FCSTD DOCUMENT  (FreeCAD 0.19R)
Label: CNC
License: All rights reserved
LicenseURL: http://en.wikipedia.org/wiki/All_rights_reserved
objects: App::Link×56, App::DocumentObjectGroup×2, PartDesign::CoordinateSystem×1, App::FeaturePython×1, App::Part×1
note: 1 computed .brp shape members not serialized (recipe doc carries the construction recipe); baked Part::Feature solids carry a one-line shape summary decoded from their .brp
EXTERNAL_REF file=x_tube.FCStd obj=LCS_hole1
EXTERNAL_REF file=y_tube.FCStd obj=LCS_hole1
EXTERNAL_REF file=x_tube.FCStd obj=Body
EXTERNAL_REF file=y_tube.FCStd obj=LCS_hole2
EXTERNAL_REF file=x_rail.FCStd obj=LCS_mount
EXTERNAL_REF file=x_tube.FCStd obj=LCS_rail_mount
EXTERNAL_REF file=x_rail.FCStd obj=Body
EXTERNAL_REF file=TRH15A.FCStd obj=LCS_MOUNT
EXTERNAL_REF file=x_rail.FCStd obj=LCS_CARET_MOUNT
EXTERNAL_REF file=TRH15A.FCStd obj=Body
EXTERNAL_REF file=BF12_SUPPORT.FCStd obj=LCS_TUBE_MOUNT
EXTERNAL_REF file=x_tube.FCStd obj=LCS_BF_MOUNT
EXTERNAL_REF file=BF12_SUPPORT.FCStd obj=Body
EXTERNAL_REF file=BF12.FCStd obj=LCS_mount
EXTERNAL_REF file=BF12_SUPPORT.FCStd obj=LCS_BF_MOUNT
EXTERNAL_REF file=BF12.FCStd obj=Body
EXTERNAL_REF file=portal_tube.FCStd obj=LCS_1
EXTERNAL_REF file=spacer.FCStd obj=LCS_6
EXTERNAL_REF file=portal_tube.FCStd obj=Body
EXTERNAL_REF file=BF12.FCStd obj=LCS_BB1
EXTERNAL_REF file=sfu1605_500.FCStd obj=LCS_SLAVE_SIDE
EXTERNAL_REF file=sfu1605_500.FCStd obj=Body
EXTERNAL_REF file=x_tube.FCStd obj=LCS_hole2
EXTERNAL_REF file=y_tube.FCStd obj=Body
EXTERNAL_REF file=BK12.FCStd obj=LCS_mount
EXTERNAL_REF file=sfu1605_500.FCStd obj=LCS_BK_MOUNT
EXTERNAL_REF file=BK12.FCStd obj=Body
EXTERNAL_REF file=BK12.FCStd obj=LCS_H1
EXTERNAL_REF file=BK12_SUPPORT.FCStd obj=LCS_M1
EXTERNAL_REF file=BK12_SUPPORT.FCStd obj=Body
EXTERNAL_REF file=DSG16.FCStd obj=LCS_M2
EXTERNAL_REF file=portal_support_tube.FCStd obj=LCS_mh2
EXTERNAL_REF file=DSG16.FCStd obj=Body
EXTERNAL_REF file=portal_support_tube_left.FCStd obj=LCS_ch2
EXTERNAL_REF file=DSG16.FCStd obj=LCS_H1
EXTERNAL_REF file=1605.FCStd obj=LCS_N1
EXTERNAL_REF file=1605.FCStd obj=Body
EXTERNAL_REF file=DSG16.FCStd obj=LCS_H2
EXTERNAL_REF file=1605.FCStd obj=LCS_N2
EXTERNAL_REF file=coupling.FCStd obj=LCS_10MM
EXTERNAL_REF file=sfu1605_500.FCStd obj=LCS_COUPLING
EXTERNAL_REF file=coupling.FCStd obj=Body
EXTERNAL_REF file=coupling.FCStd obj=LCS_8MM
EXTERNAL_REF file=nema_23.FCStd obj=LCS_shaft
EXTERNAL_REF file=nema_23.FCStd obj=Body
EXTERNAL_REF file=nema_23.FCStd obj=LCS_m3
EXTERNAL_REF file=stpm_bracket.FCStd obj=LCS_h2
EXTERNAL_REF file=stpm_bracket.FCStd obj=Body
EXTERNAL_REF file=portal_tube.FCStd obj=LCS_top_rail
EXTERNAL_REF file=y_rail.FCStd obj=LCS_mount
EXTERNAL_REF file=y_rail.FCStd obj=Body
EXTERNAL_REF file=portal_tube.FCStd obj=LCS_bottom_RAIL
EXTERNAL_REF file=y_rail.FCStd obj=LCS_caret_mount
EXTERNAL_REF file=TRH15A.FCStd obj=LCS_h4
EXTERNAL_REF file=zbracket.FCStd obj=LCS_h1
EXTERNAL_REF file=zbracket.FCStd obj=Body
EXTERNAL_REF file=LINMOD200.FCStd obj=LCS_m2
EXTERNAL_REF file=zbracket.FCStd obj=LCS_1
EXTERNAL_REF file=LINMOD200.FCStd obj=Body
EXTERNAL_REF file=LINMOD200.FCStd obj=LCS_caret_mount
EXTERNAL_REF file=LINMOD_CARET.FCStd obj=LCS_m1
EXTERNAL_REF file=LINMOD_CARET.FCStd obj=Body
EXTERNAL_REF file=LINMOD_CARET.FCStd obj=LCS_2
EXTERNAL_REF file=adapter_plate.FCStd obj=LCS_7
EXTERNAL_REF file=adapter_plate.FCStd obj=Body
EXTERNAL_REF file=adapter_plate.FCStd obj=LCS_2
EXTERNAL_REF file=spindle_holder.FCStd obj=LCS_h2
EXTERNAL_REF file=spindle_holder.FCStd obj=Body
EXTERNAL_REF file=spindle.FCStd obj=LCS_mount
EXTERNAL_REF file=spindle_holder.FCStd obj=LCS_motor_mount1
EXTERNAL_REF file=spindle.FCStd obj=Body
EXTERNAL_REF file=BF12_PORTAL_SUPPORT.FCStd obj=LCS_TUBE_MOUNT
EXTERNAL_REF file=portal_tube.FCStd obj=LCS_BF
EXTERNAL_REF file=BF12_PORTAL_SUPPORT.FCStd obj=Body
EXTERNAL_REF file=BF12_PORTAL_SUPPORT.FCStd obj=LCS_BF_MOUNT
EXTERNAL_REF file=sfu1605_700.FCStd obj=LCS_m1
EXTERNAL_REF file=sfu1605_700.FCStd obj=Body
EXTERNAL_REF file=sfu1605_700.FCStd obj=LCS_m2
EXTERNAL_REF file=BK12_PORTAL_SUPPORT.FCStd obj=LCS_M1
EXTERNAL_REF file=BK12_PORTAL_SUPPORT.FCStd obj=Body
EXTERNAL_REF file=sfu1605_700.FCStd obj=LCS_m3
EXTERNAL_REF file=DSG16.FCStd obj=LCS_M1
EXTERNAL_REF file=zbracket.FCStd obj=LCS_DSG16_MOUNT4
EXTERNAL_REF file=TRH15A.FCStd obj=LCS_h1
EXTERNAL_REF file=portal_support_tube.FCStd obj=LCS_h1
EXTERNAL_REF file=portal_support_tube.FCStd obj=Body
EXTERNAL_REF file=portal_support_tube.FCStd obj=LCS_h8
EXTERNAL_REF file=portal_support_tube_left.FCStd obj=LCS_h4
EXTERNAL_REF file=portal_support_tube_left.FCStd obj=Body
EXTERNAL_REF file=portal_support_tube_left.FCStd obj=LCS_h5
EXTERNAL_REF file=portal_column_right.FCStd obj=LCS_h1
EXTERNAL_REF file=portal_support_tube.FCStd obj=LCS_ch2
EXTERNAL_REF file=portal_column_right.FCStd obj=Body
EXTERNAL_REF file=portal_column_left.FCStd obj=LCS_h1
EXTERNAL_REF file=portal_support_tube_left.FCStd obj=LCS_4
EXTERNAL_REF file=portal_column_left.FCStd obj=Body
EXTERNAL_REF file=portal_column_right.FCStd obj=LCS_3
EXTERNAL_REF file=spacer.FCStd obj=LCS_2
EXTERNAL_REF file=spacer.FCStd obj=Body
EXTERNAL_REF file=portal_column_left.FCStd obj=LCS_2
EXTERNAL_REF file=spacer.FCStd obj=LCS_1

FEATURE [App::DocumentObjectGroup] Parts
FEATURE [PartDesign::CoordinateSystem] LCS_Origin
  AttacherType = Attacher::AttachEngine3D
  MapMode = 2
  Support = -> [X_Axis]
FEATURE [App::DocumentObjectGroup] Constraints
FEATURE [App::FeaturePython] Variables  # WARN: FeaturePython — macro-defined, semantics opaque (R4)
FEATURE [App::Link] x_tube_Body
  AssemblyType = Asm4EE
  AttachedBy = #LCS_hole1
  AttachedTo = y_tube_Body#LCS_hole1
  AttachmentOffset = pos=(0,0,0) rot=(-0.707107,0.707107,0;3.14159rad)
  LinkPlacement = pos=(-580,-3.739e-13,30) rot=(-0.707107,0.707107,0;3.14159rad)
  LinkedObject = -> <external x_tube.FCStd>#Body
  Placement = pos=(-580,-3.739e-13,30) rot=(-0.707107,0.707107,0;3.14159rad)
  expr: Placement = y_tube_Body.Placement * y_tube#LCS_hole1.Placement * AttachmentOffset * x_tube#LCS_hole1.Placement ^ -1
FEATURE [App::Link] x_tube_Body001
  AssemblyType = Asm4EE
  AttachedBy = #LCS_hole1
  AttachedTo = y_tube_Body#LCS_hole2
  AttachmentOffset = pos=(0,0,0) rot=(0.707107,-0.707107,0;3.14159rad)
  LinkPlacement = pos=(-580,-733,30) rot=(0.707107,-0.707107,0;3.14159rad)
  LinkedObject = -> <external x_tube.FCStd>#Body
  Placement = pos=(-580,-733,30) rot=(0.707107,-0.707107,0;3.14159rad)
  expr: Placement = y_tube_Body.Placement * y_tube#LCS_hole2.Placement * AttachmentOffset * x_tube#LCS_hole1.Placement ^ -1
FEATURE [App::Link] x_rail_Body
  AssemblyType = Asm4EE
  AttachedBy = #LCS_mount
  AttachedTo = x_tube_Body#LCS_rail_mount
  AttachmentOffset = pos=(0,0,0) rot=(0,-1,0;3.14159rad)
  LinkPlacement = pos=(-540,-3.67e-13,60) rot=(0,0,-1;4.71239rad)
  LinkedObject = -> <external x_rail.FCStd>#Body
  Placement = pos=(-540,-3.67e-13,60) rot=(0,0,-1;4.71239rad)
  expr: Placement = x_tube_Body.Placement * x_tube#LCS_rail_mount.Placement * AttachmentOffset * x_rail#LCS_mount.Placement ^ -1
FEATURE [App::Link] x_rail_Body001
  AssemblyType = Asm4EE
  AttachedBy = #LCS_mount
  AttachedTo = x_tube_Body001#LCS_rail_mount
  AttachmentOffset = pos=(0,0,0) rot=(0,1,0;3.14159rad)
  LinkPlacement = pos=(-540,-733,60) rot=(0,0,-1;4.71239rad)
  LinkedObject = -> <external x_rail.FCStd>#Body
  Placement = pos=(-540,-733,60) rot=(0,0,-1;4.71239rad)
  expr: Placement = x_tube_Body001.Placement * x_tube#LCS_rail_mount.Placement * AttachmentOffset * x_rail#LCS_mount.Placement ^ -1
FEATURE [App::Link] TRH15A_Body
  AssemblyType = Asm4EE
  AttachedBy = #LCS_MOUNT
  AttachedTo = x_rail_Body#LCS_CARET_MOUNT
  AttachmentOffset = pos=(0,0,0) rot=(1,0,0;3.14159rad)
  LinkPlacement = pos=(-440,-2.957e-13,64.2) rot=(0,0,-1;1.5708rad)
  LinkedObject = -> <external TRH15A.FCStd>#Body
  Placement = pos=(-440,-2.957e-13,64.2) rot=(0,0,-1;1.5708rad)
  expr: Placement = x_rail_Body.Placement * x_rail#LCS_CARET_MOUNT.Placement * AttachmentOffset * TRH15A#LCS_MOUNT.Placement ^ -1
FEATURE [App::Link] TRH15A_Body001
  AssemblyType = Asm4EE
  AttachedBy = #LCS_MOUNT
  AttachedTo = x_rail_Body001#LCS_CARET_MOUNT
  AttachmentOffset = pos=(0,0,0) rot=(1,0,0;3.14159rad)
  LinkPlacement = pos=(-440,-733,64.2) rot=(0,0,-1;1.5708rad)
  LinkedObject = -> <external TRH15A.FCStd>#Body
  Placement = pos=(-440,-733,64.2) rot=(0,0,-1;1.5708rad)
  expr: Placement = x_rail_Body001.Placement * x_rail#LCS_CARET_MOUNT.Placement * AttachmentOffset * TRH15A#LCS_MOUNT.Placement ^ -1
FEATURE [App::Link] BF12_SUPPORT_Body
  AssemblyType = Asm4EE
  AttachedBy = #LCS_TUBE_MOUNT
  AttachedTo = x_tube_Body#LCS_BF_MOUNT
  AttachmentOffset = pos=(0,0,0) rot=(0,-1,0;3.14159rad)
  LinkPlacement = pos=(-575,-3.77e-13,60) rot=(0,0,-1;4.71239rad)
  LinkedObject = -> <external BF12_SUPPORT.FCStd>#Body
  Placement = pos=(-575,-3.77e-13,60) rot=(0,0,-1;4.71239rad)
  expr: Placement = x_tube_Body.Placement * x_tube#LCS_BF_MOUNT.Placement * AttachmentOffset * BF12_SUPPORT#LCS_TUBE_MOUNT.Placement ^ -1
FEATURE [App::Link] BF12_Body
  AssemblyType = Asm4EE
  AttachedBy = #LCS_mount
  AttachedTo = BF12_SUPPORT_Body#LCS_BF_MOUNT
  AttachmentOffset = pos=(0,0,0) rot=(0,-1,0;3.14159rad)
  LinkPlacement = pos=(-575,-3.884e-13,96) rot=(0,0,-1;4.71239rad)
  LinkedObject = -> <external BF12.FCStd>#Body
  Placement = pos=(-575,-3.884e-13,96) rot=(0,0,-1;4.71239rad)
  expr: Placement = BF12_SUPPORT_Body.Placement * BF12_SUPPORT#LCS_BF_MOUNT.Placement * AttachmentOffset * BF12#LCS_mount.Placement ^ -1
FEATURE [App::Link] BF12_SUPPORT_Body001
  AssemblyType = Asm4EE
  AttachedBy = #LCS_TUBE_MOUNT
  AttachedTo = x_tube_Body001#LCS_BF_MOUNT
  AttachmentOffset = pos=(0,0,0) rot=(0,-1,0;3.14159rad)
  LinkPlacement = pos=(-575,-733,60) rot=(0,0,1;1.5708rad)
  LinkedObject = -> <external BF12_SUPPORT.FCStd>#Body
  Placement = pos=(-575,-733,60) rot=(0,0,1;1.5708rad)
  expr: Placement = x_tube_Body001.Placement * x_tube#LCS_BF_MOUNT.Placement * AttachmentOffset * BF12_SUPPORT#LCS_TUBE_MOUNT.Placement ^ -1
FEATURE [App::Link] BF12_Body001
  AssemblyType = Asm4EE
  AttachedBy = #LCS_mount
  AttachedTo = BF12_SUPPORT_Body001#LCS_BF_MOUNT
  AttachmentOffset = pos=(0,0,0) rot=(0,-1,0;3.14159rad)
  LinkPlacement = pos=(-575,-733,96) rot=(0,0,1;1.5708rad)
  LinkedObject = -> <external BF12.FCStd>#Body
  Placement = pos=(-575,-733,96) rot=(0,0,1;1.5708rad)
  expr: Placement = BF12_SUPPORT_Body001.Placement * BF12_SUPPORT#LCS_BF_MOUNT.Placement * AttachmentOffset * BF12#LCS_mount.Placement ^ -1
FEATURE [App::Link] portal_tube_Body
  AssemblyType = Asm4EE
  AttachedBy = #LCS_1
  AttachedTo = spacer_Body#LCS_6
  AttachmentOffset = pos=(0,0,0) rot=(-0.707107,-0.707107,0;3.14159rad)
  LinkPlacement = pos=(-576.9,-823,254) rot=(1,0,0;3.14159rad)
  LinkedObject = -> <external portal_tube.FCStd>#Body
  Placement = pos=(-576.9,-823,254) rot=(1,0,0;3.14159rad)
  expr: Placement = spacer_Body.Placement * spacer#LCS_6.Placement * AttachmentOffset * portal_tube#LCS_1.Placement ^ -1
FEATURE [App::Link] sfu1605_500_Body
  AssemblyType = Asm4EE
  AttachedBy = #LCS_SLAVE_SIDE
  AttachedTo = BF12_Body#LCS_BB1
  LinkPlacement = pos=(-72,1.847e-13,121) rot=(0,0,1;1.5708rad)
  LinkedObject = -> <external sfu1605_500.FCStd>#Body
  Placement = pos=(-72,1.847e-13,121) rot=(0,0,1;1.5708rad)
  expr: Placement = BF12_Body.Placement * BF12#LCS_BB1.Placement * AttachmentOffset * sfu1605_500#LCS_SLAVE_SIDE.Placement ^ -1
FEATURE [App::Link] sfu1605_500_Body001
  AssemblyType = Asm4EE
  AttachedBy = #LCS_SLAVE_SIDE
  AttachedTo = BF12_Body001#LCS_BB1
  LinkPlacement = pos=(-72,-733,121) rot=(0,0,-1;4.71239rad)
  LinkedObject = -> <external sfu1605_500.FCStd>#Body
  Placement = pos=(-72,-733,121) rot=(0,0,-1;4.71239rad)
  expr: Placement = BF12_Body001.Placement * BF12#LCS_BB1.Placement * AttachmentOffset * sfu1605_500#LCS_SLAVE_SIDE.Placement ^ -1
FEATURE [App::Link] y_tube_Body001
  AssemblyType = Asm4EE
  AttachedBy = #LCS_hole2
  AttachedTo = x_tube_Body001#LCS_hole2
  AttachmentOffset = pos=(0,0,0) rot=(-0.707107,0.707107,0;3.14159rad)
  LinkPlacement = pos=(-550,-763,-30) rot=(0,0,1;3.14159rad)
  LinkedObject = -> <external y_tube.FCStd>#Body
  Placement = pos=(-550,-763,-30) rot=(0,0,1;3.14159rad)
  expr: Placement = x_tube_Body001.Placement * x_tube#LCS_hole2.Placement * AttachmentOffset * y_tube#LCS_hole2.Placement ^ -1
FEATURE [App::Link] y_tube_Body
  AssemblyType = Asm4EE
  AttachedBy = #LCS_hole2
  AttachedTo = Parent Assembly#LCS_Origin
  AttachmentOffset = pos=(0,0,0) rot=(0,0,1;1.5708rad)
  LinkPlacement = pos=(-3.4e-13,-763,-30) rot=(0,0,1;3.14159rad)
  LinkedObject = -> <external y_tube.FCStd>#Body
  Placement = pos=(-3.4e-13,-763,-30) rot=(0,0,1;3.14159rad)
  expr: Placement = LCS_Origin.Placement * AttachmentOffset * y_tube#LCS_hole1.Placement ^ -1
FEATURE [App::Link] BK12_Body
  AssemblyType = Asm4EE
  AttachedBy = #LCS_mount
  AttachedTo = sfu1605_500_Body#LCS_BK_MOUNT
  AttachmentOffset = pos=(0,0,0) rot=(0,-1,0;3.14159rad)
  LinkPlacement = pos=(-126,1.313e-13,96) rot=(0,0,-1;4.71239rad)
  LinkedObject = -> <external BK12.FCStd>#Body
  Placement = pos=(-126,1.313e-13,96) rot=(0,0,-1;4.71239rad)
  expr: Placement = sfu1605_500_Body.Placement * sfu1605_500#LCS_BK_MOUNT.Placement * AttachmentOffset * BK12#LCS_mount.Placement ^ -1
FEATURE [App::Link] BK12_Body001
  AssemblyType = Asm4EE
  AttachedBy = #LCS_mount
  AttachedTo = sfu1605_500_Body001#LCS_BK_MOUNT
  AttachmentOffset = pos=(0,0,0) rot=(0,-1,0;3.14159rad)
  LinkPlacement = pos=(-126,-733,96) rot=(0,0,1;1.5708rad)
  LinkedObject = -> <external BK12.FCStd>#Body
  Placement = pos=(-126,-733,96) rot=(0,0,1;1.5708rad)
  expr: Placement = sfu1605_500_Body001.Placement * sfu1605_500#LCS_BK_MOUNT.Placement * AttachmentOffset * BK12#LCS_mount.Placement ^ -1
FEATURE [App::Link] BK12_SUPPORT_Body
  AssemblyType = Asm4EE
  AttachedBy = #LCS_M1
  AttachedTo = BK12_Body001#LCS_H1
  AttachmentOffset = pos=(0,0,0) rot=(1,0,0;3.14159rad)
  LinkPlacement = pos=(-113.5,-733,60) rot=(0,0,1;4.71239rad)
  LinkedObject = -> <external BK12_SUPPORT.FCStd>#Body
  Placement = pos=(-113.5,-733,60) rot=(0,0,1;4.71239rad)
  expr: Placement = BK12_Body001.Placement * BK12#LCS_H1.Placement * AttachmentOffset * BK12_SUPPORT#LCS_M1.Placement ^ -1
FEATURE [App::Link] BK12_SUPPORT_Body001
  AssemblyType = Asm4EE
  AttachedBy = #LCS_M1
  AttachedTo = BK12_Body#LCS_H1
  AttachmentOffset = pos=(0,0,0) rot=(1,0,0;3.14159rad)
  LinkPlacement = pos=(-113.5,1.457e-13,60) rot=(0,0,-1;1.5708rad)
  LinkedObject = -> <external BK12_SUPPORT.FCStd>#Body
  Placement = pos=(-113.5,1.457e-13,60) rot=(0,0,-1;1.5708rad)
  expr: Placement = BK12_Body.Placement * BK12#LCS_H1.Placement * AttachmentOffset * BK12_SUPPORT#LCS_M1.Placement ^ -1
FEATURE [App::Link] DSG16_Body
  AssemblyType = Asm4EE
  AttachedBy = #LCS_M2
  AttachedTo = portal_support_tube_Body#LCS_mh2
  AttachmentOffset = pos=(0,0,0) rot=(0,0,-1;3.14159rad)
  LinkPlacement = pos=(-380.9,-2.771e-13,121) rot=(-0.57735,0.57735,-0.57735;4.18879rad)
  LinkedObject = -> <external DSG16.FCStd>#Body
  Placement = pos=(-380.9,-2.771e-13,121) rot=(-0.57735,0.57735,-0.57735;4.18879rad)
  expr: Placement = portal_support_tube_Body.Placement * portal_support_tube#LCS_mh2.Placement * AttachmentOffset * DSG16#LCS_M2.Placement ^ -1
FEATURE [App::Link] DSG16_Body001
  AssemblyType = Asm4EE
  AttachedBy = #LCS_M2
  AttachedTo = portal_support_tube_left_Body#LCS_ch2
  AttachmentOffset = pos=(0,0,0) rot=(0,0,-1;3.14159rad)
  LinkPlacement = pos=(-380.9,-733,121) rot=(-0.57735,0.57735,-0.57735;4.18879rad)
  LinkedObject = -> <external DSG16.FCStd>#Body
  Placement = pos=(-380.9,-733,121) rot=(-0.57735,0.57735,-0.57735;4.18879rad)
  expr: Placement = portal_support_tube_left_Body.Placement * portal_support_tube_left#LCS_ch2.Placement * AttachmentOffset * DSG16#LCS_M2.Placement ^ -1
FEATURE [App::Link] _605_Body
  AssemblyType = Asm4EE
  AttachedBy = #LCS_N1
  AttachedTo = DSG16_Body#LCS_H1
  LinkPlacement = pos=(-370.9,1.0711e-12,121) rot=(-0.57735,0.57735,-0.57735;4.18879rad)
  LinkedObject = -> <external 1605.FCStd>#Body
  Placement = pos=(-370.9,1.0711e-12,121) rot=(-0.57735,0.57735,-0.57735;4.18879rad)
  expr: Placement = DSG16_Body.Placement * DSG16#LCS_H1.Placement * AttachmentOffset * _605#LCS_N1.Placement ^ -1
FEATURE [App::Link] _605_Body001
  AssemblyType = Asm4EE
  AttachedBy = #LCS_N2
  AttachedTo = DSG16_Body001#LCS_H2
  LinkPlacement = pos=(-370.9,-733,121) rot=(-0.57735,0.57735,-0.57735;4.18879rad)
  LinkedObject = -> <external 1605.FCStd>#Body
  Placement = pos=(-370.9,-733,121) rot=(-0.57735,0.57735,-0.57735;4.18879rad)
  expr: Placement = DSG16_Body001.Placement * DSG16#LCS_H2.Placement * AttachmentOffset * _605#LCS_N2.Placement ^ -1
FEATURE [App::Link] coupling_Body
  AssemblyType = Asm4EE
  AttachedBy = #LCS_10MM
  AttachedTo = sfu1605_500_Body#LCS_COUPLING
  AttachmentOffset = pos=(0,0,0) rot=(1,0,0;3.14159rad)
  LinkPlacement = pos=(-52,1.98e-13,121) rot=(0,0,1;4.71239rad)
  LinkedObject = -> <external coupling.FCStd>#Body
  Placement = pos=(-52,1.98e-13,121) rot=(0,0,1;4.71239rad)
  expr: Placement = sfu1605_500_Body.Placement * sfu1605_500#LCS_COUPLING.Placement * AttachmentOffset * coupling#LCS_10MM.Placement ^ -1
FEATURE [App::Link] coupling_Body_2
  AssemblyType = Asm4EE
  AttachedBy = #LCS_10MM
  AttachedTo = sfu1605_500_Body001#LCS_COUPLING
  AttachmentOffset = pos=(0,0,0) rot=(1,0,0;3.14159rad)
  LinkPlacement = pos=(-52,-733,121) rot=(0,0,-1;1.5708rad)
  LinkedObject = -> <external coupling.FCStd>#Body
  Placement = pos=(-52,-733,121) rot=(0,0,-1;1.5708rad)
  expr: Placement = sfu1605_500_Body001.Placement * sfu1605_500#LCS_COUPLING.Placement * AttachmentOffset * coupling#LCS_10MM.Placement ^ -1
FEATURE [App::Link] nema_23_Body
  AssemblyType = Asm4EE
  AttachedBy = #LCS_shaft
  AttachedTo = coupling_Body#LCS_8MM
  AttachmentOffset = pos=(0,0,0) rot=(1,0,0;3.14159rad)
  LinkPlacement = pos=(-34.9,2.169e-13,121) rot=(0.707107,0.707107,0;3.14159rad)
  LinkedObject = -> <external nema_23.FCStd>#Body
  Placement = pos=(-34.9,2.169e-13,121) rot=(0.707107,0.707107,0;3.14159rad)
  expr: Placement = coupling_Body.Placement * coupling#LCS_8MM.Placement * AttachmentOffset * nema_23#LCS_shaft.Placement ^ -1
FEATURE [App::Link] nema_23_Body001
  AssemblyType = Asm4EE
  AttachedBy = #LCS_shaft
  AttachedTo = coupling_Body_2#LCS_8MM
  AttachmentOffset = pos=(0,0,0) rot=(1,0,0;3.14159rad)
  LinkPlacement = pos=(-34.9,-733,121) rot=(-0.707107,-0.707107,0;3.14159rad)
  LinkedObject = -> <external nema_23.FCStd>#Body
  Placement = pos=(-34.9,-733,121) rot=(-0.707107,-0.707107,0;3.14159rad)
  expr: Placement = coupling_Body_2.Placement * coupling#LCS_8MM.Placement * AttachmentOffset * nema_23#LCS_shaft.Placement ^ -1
FEATURE [App::Link] stpm_bracket_Body
  AssemblyType = Asm4EE
  AttachedBy = #LCS_h2
  AttachedTo = nema_23_Body#LCS_m3
  AttachmentOffset = pos=(0,0,0) rot=(0,0,1;1.5708rad)
  LinkPlacement = pos=(-42.9,32.45,81.95) rot=(0,0,1;0rad)
  LinkedObject = -> <external stpm_bracket.FCStd>#Body
  Placement = pos=(-42.9,32.45,81.95) rot=(0,0,1;0rad)
  expr: Placement = nema_23_Body.Placement * nema_23#LCS_m3.Placement * AttachmentOffset * stpm_bracket#LCS_h2.Placement ^ -1
FEATURE [App::Link] stpm_bracket_Body001
  AssemblyType = Asm4EE
  AttachedBy = #LCS_h2
  AttachedTo = nema_23_Body001#LCS_m3
  AttachmentOffset = pos=(0,0,0) rot=(0,0,1;1.5708rad)
  LinkPlacement = pos=(-42.9,-700.55,81.95) rot=(0,0,1;0rad)
  LinkedObject = -> <external stpm_bracket.FCStd>#Body
  Placement = pos=(-42.9,-700.55,81.95) rot=(0,0,1;0rad)
  expr: Placement = nema_23_Body001.Placement * nema_23#LCS_m3.Placement * AttachmentOffset * stpm_bracket#LCS_h2.Placement ^ -1
FEATURE [App::Link] y_rail_Body
  AssemblyType = Asm4EE
  AttachedBy = #LCS_mount
  AttachedTo = portal_tube_Body#LCS_top_rail
  AttachmentOffset = pos=(0,0,0) rot=(0,-1,0;3.14159rad)
  LinkPlacement = pos=(-576.9,-663,224) rot=(1,0,0;3.14159rad)
  LinkedObject = -> <external y_rail.FCStd>#Body
  Placement = pos=(-576.9,-663,224) rot=(1,0,0;3.14159rad)
  expr: Placement = portal_tube_Body.Placement * portal_tube#LCS_top_rail.Placement * AttachmentOffset * y_rail#LCS_mount.Placement ^ -1
FEATURE [App::Link] y_rail_Body001
  AssemblyType = Asm4EE
  AttachedBy = #LCS_mount
  AttachedTo = portal_tube_Body#LCS_bottom_RAIL
  AttachmentOffset = pos=(0,0,0) rot=(0,1,0;3.14159rad)
  LinkPlacement = pos=(-576.9,-663,284) rot=(0,0,-1;3.14159rad)
  LinkedObject = -> <external y_rail.FCStd>#Body
  Placement = pos=(-576.9,-663,284) rot=(0,0,-1;3.14159rad)
  expr: Placement = portal_tube_Body.Placement * portal_tube#LCS_bottom_RAIL.Placement * AttachmentOffset * y_rail#LCS_mount.Placement ^ -1
FEATURE [App::Link] TRH15A_Body002
  AssemblyType = Asm4EE
  AttachedBy = #LCS_MOUNT
  AttachedTo = y_rail_Body#LCS_caret_mount
  AttachmentOffset = pos=(0,0,0) rot=(-1,0,0;3.14159rad)
  LinkPlacement = pos=(-576.9,-563,219.8) rot=(0,1,0;3.14159rad)
  LinkedObject = -> <external TRH15A.FCStd>#Body
  Placement = pos=(-576.9,-563,219.8) rot=(0,1,0;3.14159rad)
  expr: Placement = y_rail_Body.Placement * y_rail#LCS_caret_mount.Placement * AttachmentOffset * TRH15A#LCS_MOUNT.Placement ^ -1
FEATURE [App::Link] zbracket_Body_2
  AssemblyType = Asm4EE
  AttachedBy = #LCS_h1
  AttachedTo = TRH15A_Body002#LCS_h4
  AttachmentOffset = pos=(0,0,0) rot=(0,0,1;3.14159rad)
  LinkPlacement = pos=(-530.9,-609.9,197) rot=(-0.57735,0.57735,0.57735;2.0944rad)
  LinkedObject = -> <external zbracket.FCStd>#Body
  Placement = pos=(-530.9,-609.9,197) rot=(-0.57735,0.57735,0.57735;2.0944rad)
  expr: Placement = TRH15A_Body002.Placement * TRH15A#LCS_h4.Placement * AttachmentOffset * zbracket#LCS_h1.Placement ^ -1
FEATURE [App::Link] LINMOD200_Body
  AssemblyType = Asm4EE
  AttachedBy = #LCS_m2
  AttachedTo = zbracket_Body_2#LCS_1
  AttachmentOffset = pos=(0,0,0) rot=(-0.707107,-0.707107,0;3.14159rad)
  LinkPlacement = pos=(-520.9,-549.9,202) rot=(-0.57735,0.57735,-0.57735;2.0944rad)
  LinkedObject = -> <external LINMOD200.FCStd>#Body
  Placement = pos=(-520.9,-549.9,202) rot=(-0.57735,0.57735,-0.57735;2.0944rad)
  expr: Placement = zbracket_Body_2.Placement * zbracket#LCS_1.Placement * AttachmentOffset * LINMOD200#LCS_m2.Placement ^ -1
FEATURE [App::Link] LINMOD_CARET_Body
  AssemblyType = Asm4EE
  AttachedBy = #LCS_m1
  AttachedTo = LINMOD200_Body#LCS_caret_mount
  AttachmentOffset = pos=(0,0,0) rot=(0,1,0;3.14159rad)
  LinkPlacement = pos=(-477.9,-549.9,257) rot=(0.57735,-0.57735,0.57735;4.18879rad)
  LinkedObject = -> <external LINMOD_CARET.FCStd>#Body
  Placement = pos=(-477.9,-549.9,257) rot=(0.57735,-0.57735,0.57735;4.18879rad)
  expr: Placement = LINMOD200_Body.Placement * LINMOD200#LCS_caret_mount.Placement * AttachmentOffset * LINMOD_CARET#LCS_m1.Placement ^ -1
FEATURE [App::Link] adapter_plate_Body
  AssemblyType = Asm4EE
  AttachedBy = #LCS_7
  AttachedTo = LINMOD_CARET_Body#LCS_2
  AttachmentOffset = pos=(0,0,0) rot=(1,0,0;3.14159rad)
  LinkPlacement = pos=(-467.9,-549.9,306.987) rot=(-0.57735,-0.57735,-0.57735;4.18879rad)
  LinkedObject = -> <external adapter_plate.FCStd>#Body
  Placement = pos=(-467.9,-549.9,306.987) rot=(-0.57735,-0.57735,-0.57735;4.18879rad)
  expr: Placement = LINMOD_CARET_Body.Placement * LINMOD_CARET#LCS_2.Placement * AttachmentOffset * adapter_plate#LCS_7.Placement ^ -1
FEATURE [App::Link] spindle_holder_Body
  AssemblyType = Asm4EE
  AttachedBy = #LCS_h2
  AttachedTo = adapter_plate_Body#LCS_2
  AttachmentOffset = pos=(0,0,0) rot=(1,0,0;3.14159rad)
  LinkPlacement = pos=(-442.9,-549.9,156.987) rot=(-0.707107,-0.707107,0;3.14159rad)
  LinkedObject = -> <external spindle_holder.FCStd>#Body
  Placement = pos=(-442.9,-549.9,156.987) rot=(-0.707107,-0.707107,0;3.14159rad)
  expr: Placement = adapter_plate_Body.Placement * adapter_plate#LCS_2.Placement * AttachmentOffset * spindle_holder#LCS_h2.Placement ^ -1
FEATURE [App::Link] spindle_Body
  AssemblyType = Asm4EE
  AttachedBy = #LCS_mount
  AttachedTo = spindle_holder_Body#LCS_motor_mount1
  AttachmentOffset = pos=(0,0,0) rot=(1,0,0;3.14159rad)
  LinkPlacement = pos=(-408.9,-549.9,44.9866) rot=(0,0,-1;1.5708rad)
  LinkedObject = -> <external spindle.FCStd>#Body
  Placement = pos=(-408.9,-549.9,44.9866) rot=(0,0,-1;1.5708rad)
  expr: Placement = spindle_holder_Body.Placement * spindle_holder#LCS_motor_mount1.Placement * AttachmentOffset * spindle#LCS_mount.Placement ^ -1
FEATURE [App::Link] BF12_PORTAL_SUPPORT_Body
  AssemblyType = Asm4EE
  AttachedBy = #LCS_TUBE_MOUNT
  AttachedTo = portal_tube_Body#LCS_BF
  AttachmentOffset = pos=(0,0,0) rot=(1,0,0;3.14159rad)
  LinkPlacement = pos=(-576.9,-683,284) rot=(0,0,1;0rad)
  LinkedObject = -> <external BF12_PORTAL_SUPPORT.FCStd>#Body
  Placement = pos=(-576.9,-683,284) rot=(0,0,1;0rad)
  expr: Placement = portal_tube_Body.Placement * portal_tube#LCS_BF.Placement * AttachmentOffset * BF12_PORTAL_SUPPORT#LCS_TUBE_MOUNT.Placement ^ -1
FEATURE [App::Link] BF12_Body002
  AssemblyType = Asm4EE
  AttachedBy = #LCS_mount
  AttachedTo = BF12_PORTAL_SUPPORT_Body#LCS_BF_MOUNT
  AttachmentOffset = pos=(0,0,0) rot=(1,0,0;3.14159rad)
  LinkPlacement = pos=(-576.9,-703,309.9) rot=(0,0,-1;3.14159rad)
  LinkedObject = -> <external BF12.FCStd>#Body
  Placement = pos=(-576.9,-703,309.9) rot=(0,0,-1;3.14159rad)
  expr: Placement = BF12_PORTAL_SUPPORT_Body.Placement * BF12_PORTAL_SUPPORT#LCS_BF_MOUNT.Placement * AttachmentOffset * BF12#LCS_mount.Placement ^ -1
FEATURE [App::Link] sfu1605_700_Body
  AssemblyType = Asm4EE
  AttachedBy = #LCS_m1
  AttachedTo = BF12_Body002#LCS_BB1
  LinkPlacement = pos=(-576.9,1.59027e-05,334.9) rot=(0,0,1;3.14159rad)
  LinkedObject = -> <external sfu1605_700.FCStd>#Body
  Placement = pos=(-576.9,1.59027e-05,334.9) rot=(0,0,1;3.14159rad)
  expr: Placement = BF12_Body002.Placement * BF12#LCS_BB1.Placement * AttachmentOffset * sfu1605_700#LCS_m1.Placement ^ -1
FEATURE [App::Link] BK12_Body002
  AssemblyType = Asm4EE
  AttachedBy = #LCS_mount
  AttachedTo = sfu1605_700_Body#LCS_m2
  AttachmentOffset = pos=(0,0,0) rot=(0,-1,0;3.14159rad)
  LinkPlacement = pos=(-576.9,-54,309.9) rot=(0,0,-1;3.14159rad)
  LinkedObject = -> <external BK12.FCStd>#Body
  Placement = pos=(-576.9,-54,309.9) rot=(0,0,-1;3.14159rad)
  expr: Placement = sfu1605_700_Body.Placement * sfu1605_700#LCS_m2.Placement * AttachmentOffset * BK12#LCS_mount.Placement ^ -1
FEATURE [App::Link] BK12_PORTAL_SUPPORT_Body
  AssemblyType = Asm4EE
  AttachedBy = #LCS_M1
  AttachedTo = BK12_Body001#LCS_H1
  AttachmentOffset = pos=(0,0,0) rot=(1,0,0;3.14159rad)
  LinkPlacement = pos=(-576.9,-41.5,284) rot=(0,0,1;0rad)
  LinkedObject = -> <external BK12_PORTAL_SUPPORT.FCStd>#Body
  Placement = pos=(-576.9,-41.5,284) rot=(0,0,1;0rad)
  expr: Placement = BK12_Body002.Placement * BK12#LCS_H1.Placement * AttachmentOffset * BK12_PORTAL_SUPPORT#LCS_M1.Placement ^ -1
FEATURE [App::Link] coupling_Body001
  AssemblyType = Asm4EE
  AttachedBy = #LCS_10MM
  AttachedTo = sfu1605_700_Body#LCS_m3
  AttachmentOffset = pos=(0,0,0) rot=(1,0,0;3.14159rad)
  LinkPlacement = pos=(-576.9,20,334.9) rot=(0,0,1;0rad)
  LinkedObject = -> <external coupling.FCStd>#Body
  Placement = pos=(-576.9,20,334.9) rot=(0,0,1;0rad)
  expr: Placement = sfu1605_700_Body.Placement * sfu1605_700#LCS_m3.Placement * AttachmentOffset * coupling#LCS_10MM.Placement ^ -1
FEATURE [App::Link] nema_23_Body002
  AssemblyType = Asm4EE
  AttachedBy = #LCS_shaft
  AttachedTo = coupling_Body001#LCS_8MM
  AttachmentOffset = pos=(0,0,0) rot=(1,0,0;3.14159rad)
  LinkPlacement = pos=(-576.9,37.1,334.9) rot=(0,1,0;3.14159rad)
  LinkedObject = -> <external nema_23.FCStd>#Body
  Placement = pos=(-576.9,37.1,334.9) rot=(0,1,0;3.14159rad)
  expr: Placement = coupling_Body001.Placement * coupling#LCS_8MM.Placement * AttachmentOffset * nema_23#LCS_shaft.Placement ^ -1
FEATURE [App::Link] stpm_bracket_Body002
  AssemblyType = Asm4EE
  AttachedBy = #LCS_h2
  AttachedTo = nema_23_Body002#LCS_m3
  AttachmentOffset = pos=(0,0,0) rot=(0,0,1;1.5708rad)
  LinkPlacement = pos=(-609.35,29.1,295.85) rot=(0,0,1;1.5708rad)
  LinkedObject = -> <external stpm_bracket.FCStd>#Body
  Placement = pos=(-609.35,29.1,295.85) rot=(0,0,1;1.5708rad)
  expr: Placement = nema_23_Body002.Placement * nema_23#LCS_m3.Placement * AttachmentOffset * stpm_bracket#LCS_h2.Placement ^ -1
FEATURE [App::Link] DSG16_Body002
  AssemblyType = Asm4EE
  AttachedBy = #LCS_M1
  AttachedTo = zbracket_Body_2#LCS_DSG16_MOUNT4
  LinkPlacement = pos=(-576.9,-554.9,335) rot=(0.707107,0,0.707107;3.14159rad)
  LinkedObject = -> <external DSG16.FCStd>#Body
  Placement = pos=(-576.9,-554.9,335) rot=(0.707107,0,0.707107;3.14159rad)
  expr: Placement = zbracket_Body_2.Placement * zbracket#LCS_DSG16_MOUNT4.Placement * AttachmentOffset * DSG16#LCS_M1.Placement ^ -1
FEATURE [App::Link] _605_Body002
  AssemblyType = Asm4EE
  AttachedBy = #LCS_N1
  AttachedTo = DSG16_Body002#LCS_H1
  LinkPlacement = pos=(-576.9,-544.9,335) rot=(0.707107,0,0.707107;3.14159rad)
  LinkedObject = -> <external 1605.FCStd>#Body
  Placement = pos=(-576.9,-544.9,335) rot=(0.707107,0,0.707107;3.14159rad)
  expr: Placement = DSG16_Body002.Placement * DSG16#LCS_H1.Placement * AttachmentOffset * _605#LCS_N1.Placement ^ -1
FEATURE [App::Link] portal_support_tube_Body
  AssemblyType = Asm4EE
  AttachedBy = #LCS_h1
  AttachedTo = TRH15A_Body#LCS_h1
  AttachmentOffset = pos=(0,0,0) rot=(1,0,0;3.14159rad)
  LinkPlacement = pos=(-366.9,-2.593e-13,114) rot=(0,0,-1;1.5708rad)
  LinkedObject = -> <external portal_support_tube.FCStd>#Body
  Placement = pos=(-366.9,-2.593e-13,114) rot=(0,0,-1;1.5708rad)
  expr: Placement = TRH15A_Body.Placement * TRH15A#LCS_h1.Placement * AttachmentOffset * portal_support_tube#LCS_h1.Placement ^ -1
FEATURE [App::Link] TRH15A_Body004
  AssemblyType = Asm4EE
  AttachedBy = #LCS_h1
  AttachedTo = portal_support_tube_Body#LCS_h8
  AttachmentOffset = pos=(0,0,0) rot=(0,-1,0;3.14159rad)
  LinkPlacement = pos=(-413.8,-2.7e-13,64.2) rot=(0,0,-1;4.71239rad)
  LinkedObject = -> <external TRH15A.FCStd>#Body
  Placement = pos=(-413.8,-2.7e-13,64.2) rot=(0,0,-1;4.71239rad)
  expr: Placement = portal_support_tube_Body.Placement * portal_support_tube#LCS_h8.Placement * AttachmentOffset * TRH15A#LCS_h1.Placement ^ -1
FEATURE [App::Link] portal_support_tube_left_Body
  AssemblyType = Asm4EE
  AttachedBy = #LCS_h4
  AttachedTo = TRH15A_Body001#LCS_h4
  AttachmentOffset = pos=(0,0,0) rot=(1,0,0;3.14159rad)
  LinkPlacement = pos=(-366.9,-733,114) rot=(0,0,-1;1.5708rad)
  LinkedObject = -> <external portal_support_tube_left.FCStd>#Body
  Placement = pos=(-366.9,-733,114) rot=(0,0,-1;1.5708rad)
  expr: Placement = TRH15A_Body001.Placement * TRH15A#LCS_h4.Placement * AttachmentOffset * portal_support_tube_left#LCS_h4.Placement ^ -1
FEATURE [App::Link] TRH15A_Body005
  AssemblyType = Asm4EE
  AttachedBy = #LCS_h4
  AttachedTo = portal_support_tube_left_Body#LCS_h5
  AttachmentOffset = pos=(0,0,0) rot=(0,-1,0;3.14159rad)
  LinkPlacement = pos=(-413.8,-733,64.2) rot=(0,0,-1;4.71239rad)
  LinkedObject = -> <external TRH15A.FCStd>#Body
  Placement = pos=(-413.8,-733,64.2) rot=(0,0,-1;4.71239rad)
  expr: Placement = portal_support_tube_left_Body.Placement * portal_support_tube_left#LCS_h5.Placement * AttachmentOffset * TRH15A#LCS_h4.Placement ^ -1
FEATURE [App::Link] portal_column_right_Body
  AssemblyType = Asm4EE
  AttachedBy = #LCS_h1
  AttachedTo = portal_support_tube_Body#LCS_ch2
  AttachmentOffset = pos=(0,0,0) rot=(-0.707107,-0.707107,0;3.14159rad)
  LinkPlacement = pos=(-456.9,60,84) rot=(0,0,1;0rad)
  LinkedObject = -> <external portal_column_right.FCStd>#Body
  Placement = pos=(-456.9,60,84) rot=(0,0,1;0rad)
  expr: Placement = portal_support_tube_Body.Placement * portal_support_tube#LCS_ch2.Placement * AttachmentOffset * portal_column_right#LCS_h1.Placement ^ -1
FEATURE [App::Link] portal_column_left_Body
  AssemblyType = Asm4EE
  AttachedBy = #LCS_h1
  AttachedTo = portal_support_tube_left_Body#LCS_4
  AttachmentOffset = pos=(0,0,0) rot=(0.707107,-0.707107,0;3.14159rad)
  LinkPlacement = pos=(-456.9,-793,84) rot=(0,0,1;3.14159rad)
  LinkedObject = -> <external portal_column_left.FCStd>#Body
  Placement = pos=(-456.9,-793,84) rot=(0,0,1;3.14159rad)
  expr: Placement = portal_support_tube_left_Body.Placement * portal_support_tube_left#LCS_4.Placement * AttachmentOffset * portal_column_left#LCS_h1.Placement ^ -1
FEATURE [App::Link] spacer_Body
  AssemblyType = Asm4EE
  AttachedBy = #LCS_2
  AttachedTo = portal_column_right_Body#LCS_3
  AttachmentOffset = pos=(0,0,0) rot=(1,0,0;3.14159rad)
  LinkPlacement = pos=(-516.9,60,144) rot=(0,0,1;0rad)
  LinkedObject = -> <external spacer.FCStd>#Body
  Placement = pos=(-516.9,60,144) rot=(0,0,1;0rad)
  expr: Placement = portal_column_right_Body.Placement * portal_column_right#LCS_3.Placement * AttachmentOffset * spacer#LCS_2.Placement ^ -1
FEATURE [App::Link] spacer_Body001
  AssemblyType = Asm4EE
  AttachedBy = #LCS_1
  AttachedTo = portal_column_left_Body#LCS_2
  AttachmentOffset = pos=(0,0,0) rot=(1,0,0;3.14159rad)
  LinkPlacement = pos=(-516.9,-793,143.989) rot=(0,0,1;0rad)
  LinkedObject = -> <external spacer.FCStd>#Body
  Placement = pos=(-516.9,-793,143.989) rot=(0,0,1;0rad)
  expr: Placement = portal_column_left_Body.Placement * portal_column_left#LCS_2.Placement * AttachmentOffset * spacer#LCS_1.Placement ^ -1
FEATURE [App::Part] Model
  Configuration = 0
  Group = -> [LCS_Origin,Constraints,Variables,y_tube_Body,x_tube_Body,y_tube_Body001,x_tube_Body001,x_rail_Body,x_rail_Body001,TRH15A_Body,TRH15A_Body001,BF12_SUPPORT_Body,BF12_Body,BF12_SUPPORT_Body001,BF12_Body001,portal_tube_Body,sfu1605_500_Body,sfu1605_500_Body001,BK12_Body,BK12_Body001,BK12_SUPPORT_Body,BK12_SUPPORT_Body001,DSG16_Body,DSG16_Body001,_605_Body,_605_Body001,coupling_Body,coupling_Body_2,+31 more]
  Origin = -> Origin
  Type = Assembly4 Model

RESOLVED EXTERNAL PARTS (link-assembly join: the EXTERNAL_REF files above that resolve inside this repo's crawl, each included once):
---- part 1605.FCStd = doc fcstd_c0022f04b5de ----
FCSTD DOCUMENT  (FreeCAD 0.19R)
Label: 1605
License: All rights reserved
LicenseURL: http://en.wikipedia.org/wiki/All_rights_reserved
objects: Sketcher::SketchObject×2, PartDesign::Pad×2, PartDesign::CoordinateSystem×2, PartDesign::Body×1
note: 9 computed .brp shape members not serialized (recipe doc carries the construction recipe); baked Part::Feature solids carry a one-line shape summary decoded from their .brp

FEATURE [Sketcher::SketchObject] Sketch
  FullyConstrained = true
  MapMode = 5
  Placement = pos=(0,0,0) rot=(1,0,0;1.5708rad)
  Support = -> [XZ_Plane]
  sketch-geometry (15):
    g0: LineSegment StartX=-20 StartY=13.2665 StartZ=0 EndX=-20 EndY=-13.2665 EndZ=0
    g1: LineSegment StartX=20 StartY=13.2665 StartZ=0 EndX=20 EndY=-13.2665 EndZ=0
    g2: ArcOfCircle CenterX=0 CenterY=-1.8e-15 CenterZ=0 NormalX=0 NormalY=0 NormalZ=1 AngleXU=0 Radius=24 StartAngle=0.585686 EndAngle=2.55591
    g3: ArcOfCircle CenterX=0 CenterY=-1.8e-15 CenterZ=0 NormalX=0 NormalY=0 NormalZ=1 AngleXU=0 Radius=24 StartAngle=3.72728 EndAngle=5.6975
    g4: Circle CenterX=0 CenterY=-1.8e-15 CenterZ=0 NormalX=0 NormalY=0 NormalZ=1 AngleXU=0 Radius=8
    g5: Circle CenterX=-13.435 CenterY=13.435 CenterZ=0 NormalX=0 NormalY=0 NormalZ=1 AngleXU=0 Radius=2.75
    g6: Circle CenterX=0 CenterY=19 CenterZ=0 NormalX=0 NormalY=0 NormalZ=1 AngleXU=0 Radius=2.75
    g7: Circle CenterX=13.435 CenterY=13.435 CenterZ=0 NormalX=0 NormalY=0 NormalZ=1 AngleXU=0 Radius=2.75
    g8: Circle CenterX=-13.435 CenterY=-13.435 CenterZ=0 NormalX=0 NormalY=0 NormalZ=1 AngleXU=0 Radius=2.75
    g9: Circle CenterX=0 CenterY=-19 CenterZ=0 NormalX=0 NormalY=0 NormalZ=1 AngleXU=0 Radius=2.75
    g10: Circle CenterX=13.435 CenterY=-13.435 CenterZ=0 NormalX=0 NormalY=0 NormalZ=1 AngleXU=0 Radius=2.75
    g11: LineSegment StartX=0 StartY=-1.8e-15 StartZ=0 EndX=-13.435 EndY=-13.435 EndZ=0
    g12: LineSegment StartX=0 StartY=-1.8e-15 StartZ=0 EndX=13.435 EndY=-13.435 EndZ=0
    g13: LineSegment StartX=0 StartY=-1.8e-15 StartZ=0 EndX=13.435 EndY=13.435 EndZ=0
    g14: LineSegment StartX=-13.435 StartY=13.435 StartZ=0 EndX=0 EndY=-1.8e-15 EndZ=0
  constraints (38):
    c: Vertical(g0)
    c: Vertical(g1)
    c: Coincident(g2,g-1)
    c: Coincident(g2,g0)
    c: Coincident(g2,g1)
    c: Coincident(g3,g2)
    c: Coincident(g3,g1)
    c: Coincident(g3,g0)
    c: Equal(g3,g2)
    c: Diameter(g2) = 48
    c: DistanceX(g0,g1) = 40
    c: Equal(g1,g0)
    c: Coincident(g4,g2)
    c: Diameter(g4) = 16
    c: PointOnObject(g6,g-2)
    c: PointOnObject(g9,g-2)
    c: Equal(g5,g6)
    c: Equal(g6,g7)
    c: Equal(g7,g10)
    c: Equal(g10,g9)
    c: Equal(g9,g8)
    c: Diameter(g7) = 5.5
    c: Distance(g10,g2) = 19
    c: Symmetric(g8,g10,g-2)
    c: DistanceY(g9,g2) = 19
    c: DistanceY(g2,g6) = 19
    c: Symmetric(g7,g5,g-2)
    c: Distance(g7,g2) = 19
    c: Coincident(g11,g2)
    c: Coincident(g11,g8)
    c: Coincident(g12,g2)
    c: Coincident(g12,g10)
    c: Angle(g11,g12) = 1.5708
    c: Coincident(g13,g2)
    c: Coincident(g13,g7)
    c: Coincident(g14,g5)
    c: Coincident(g14,g2)
    c: Angle(g13,g14) = 1.5708
FEATURE [PartDesign::Pad] Pad
  Direction = (1,1,1)
  Length = 10
  Length2 = 100
  Placement = pos=(0,0,0) rot=(1,0,0;1.5708rad)
  Profile = -> Sketch
  Reversed = true
  Type = 0
FEATURE [Sketcher::SketchObject] Sketch001
  FullyConstrained = true
  MapMode = 5
  Placement = pos=(0,10,-2.2e-15) rot=(-1,0,0;1.5708rad)
  Support = -> [Pad]
  sketch-geometry (2):
    g0: Circle CenterX=0 CenterY=0 CenterZ=0 NormalX=0 NormalY=0 NormalZ=1 AngleXU=0 Radius=14
    g1: Circle CenterX=0 CenterY=0 CenterZ=0 NormalX=0 NormalY=0 NormalZ=1 AngleXU=0 Radius=8
  constraints (4):
    c: Coincident(g0,g-1)
    c: Diameter(g0) = 28
    c: Coincident(g1,g0)
    c: Diameter(g1) = 16
FEATURE [PartDesign::Pad] Pad001
  BaseFeature = -> Pad
  Direction = (1,1,1)
  Length = 32
  Length2 = 100
  Placement = pos=(0,0,0) rot=(1,0,0;1.5708rad)
  Profile = -> Sketch001
  Type = 0
FEATURE [PartDesign::CoordinateSystem] LCS_N1
  AttacherType = Attacher::AttachEngine3D
  MapMode = 11
  Placement = pos=(13.435,10,13.435) rot=(0.57735,-0.57735,0.57735;2.0944rad)
  Support = -> [Pad001]
FEATURE [PartDesign::CoordinateSystem] LCS_N2
  AttacherType = Attacher::AttachEngine3D
  MapMode = 11
  Placement = pos=(-13.435,10,13.435) rot=(0.57735,-0.57735,0.57735;2.0944rad)
  Support = -> [Pad001]
FEATURE [PartDesign::Body] Body
  Group = -> [Sketch,Pad,Sketch001,Pad001,LCS_N1,LCS_N2]
  Origin = -> Origin
  Tip = -> Pad001
---- part BF12.FCStd = doc fcstd_0371a1ef9a50 ----
FCSTD DOCUMENT  (FreeCAD 0.19R)
Label: BF12
License: All rights reserved
LicenseURL: http://en.wikipedia.org/wiki/All_rights_reserved
objects: Sketcher::SketchObject×5, PartDesign::Pocket×4, PartDesign::CoordinateSystem×3, PartDesign::Pad×1, PartDesign::Body×1
note: 19 computed .brp shape members not serialized (recipe doc carries the construction recipe); baked Part::Feature solids carry a one-line shape summary decoded from their .brp

FEATURE [Sketcher::SketchObject] Sketch
  FullyConstrained = true
  MapMode = 5
  Placement = pos=(0,0,0) rot=(1,0,0;1.5708rad)
  Support = -> [XZ_Plane]
  sketch-geometry (13):
    g0: LineSegment StartX=-30 StartY=0 StartZ=0 EndX=30 EndY=0 EndZ=0
    g1: LineSegment StartX=-30 StartY=0 StartZ=0 EndX=-30 EndY=32.5 EndZ=0
    g2: LineSegment StartX=30 StartY=0 StartZ=0 EndX=30 EndY=32.5 EndZ=0
    g3: LineSegment StartX=-30 StartY=32.5 StartZ=0 EndX=-17 EndY=32.5 EndZ=0
    g4: LineSegment StartX=30 StartY=32.5 StartZ=0 EndX=17 EndY=32.5 EndZ=0
    g5: LineSegment StartX=-17 StartY=32.5 StartZ=0 EndX=-17 EndY=43 EndZ=0
    g6: LineSegment StartX=17 StartY=32.5 StartZ=0 EndX=17 EndY=43 EndZ=0
    g7: LineSegment StartX=-17 StartY=43 StartZ=0 EndX=17 EndY=43 EndZ=0
    g8: Circle CenterX=0 CenterY=25 CenterZ=0 NormalX=0 NormalY=0 NormalZ=1 AngleXU=0 Radius=5
    g9: Circle CenterX=-23 CenterY=25 CenterZ=0 NormalX=0 NormalY=0 NormalZ=1 AngleXU=0 Radius=2.75
    g10: Circle CenterX=-23 CenterY=7 CenterZ=0 NormalX=0 NormalY=0 NormalZ=1 AngleXU=0 Radius=2.75
    g11: Circle CenterX=23 CenterY=7 CenterZ=0 NormalX=0 NormalY=0 NormalZ=1 AngleXU=0 Radius=2.75
    g12: Circle CenterX=23 CenterY=25 CenterZ=0 NormalX=0 NormalY=0 NormalZ=1 AngleXU=0 Radius=2.75
  constraints (36):
    c: PointOnObject(g0,g-1)
    c: Coincident(g1,g0)
    c: Vertical(g1)
    c: Coincident(g2,g0)
    c: Vertical(g2)
    c: Coincident(g3,g1)
    c: Horizontal(g3)
    c: Coincident(g4,g2)
    c: Horizontal(g4)
    c: Coincident(g5,g3)
    c: Vertical(g5)
    c: Coincident(g6,g4)
    c: Vertical(g6)
    c: Coincident(g7,g5)
    c: Coincident(g7,g6)
    c: Horizontal(g7)
    c: PointOnObject(g8,g-2)
    c: Symmetric(g9,g12,g-2)
    c: Symmetric(g10,g11,g-2)
    c: Symmetric(g0,g0,g-2)
    c: DistanceX(g0,g0) = 60
    c: DistanceX(g10,g11) = 46
    c: DistanceX(g9,g12) = 46
    c: Equal(g10,g9)
    c: Equal(g9,g12)
    c: Equal(g12,g11)
    c: Diameter(g12) = 5.5
    c: Diameter(g8) = 10
    c: DistanceX(g7,g7) = 34
    c: DistanceY(g2,g2) = 32.5
    c: Equal(g2,g1)
    c: Equal(g4,g3)
    c: DistanceY(g0,g5) = 43
    c: DistanceY(g0,g9) = 25
    c: DistanceY(g10,g9) = 18
    c: DistanceY(g-1,g8) = 25
FEATURE [PartDesign::Pad] Pad
  Direction = (1,1,1)
  Length = 20
  Length2 = 100
  Placement = pos=(0,0,0) rot=(1,0,0;1.5708rad)
  Profile = -> Sketch
  Type = 0
FEATURE [Sketcher::SketchObject] Sketch001
  FullyConstrained = true
  MapMode = 5
  Placement = pos=(0,0,0) rot=(1,0,0;3.14159rad)
  Support = -> [Pad]
  sketch-geometry (2):
    g0: Circle CenterX=-23 CenterY=10 CenterZ=0 NormalX=0 NormalY=0 NormalZ=1 AngleXU=0 Radius=3.3
    g1: Circle CenterX=23 CenterY=10 CenterZ=0 NormalX=0 NormalY=0 NormalZ=1 AngleXU=0 Radius=3.3
  constraints (5):
    c: Symmetric(g0,g1,g-2)
    c: DistanceX(g0,g1) = 46
    c: DistanceY(g-1,g0) = 10
    c: Diameter(g1) = 6.6
    c: Equal(g1,g0)
FEATURE [PartDesign::Pocket] Pocket
  BaseFeature = -> Pad
  Length = 5
  Length2 = 100
  Placement = pos=(0,0,0) rot=(1,0,0;1.5708rad)
  Profile = -> Sketch001
  Type = 1
FEATURE [Sketcher::SketchObject] Sketch002
  ExternalGeometry = -> [Pocket]
  FullyConstrained = true
  MapMode = 5
  Placement = pos=(0,1.43e-14,32.5) rot=(0,0,1;3.14159rad)
  Support = -> [Pocket]
  sketch-geometry (2):
    g0: Circle CenterX=-23 CenterY=10 CenterZ=0 NormalX=0 NormalY=0 NormalZ=1 AngleXU=0 Radius=5.4
    g1: Circle CenterX=23 CenterY=10 CenterZ=0 NormalX=0 NormalY=0 NormalZ=1 AngleXU=0 Radius=5.4
  constraints (4):
    c: Coincident(g0,g-3)
    c: Coincident(g1,g-4)
    c: Equal(g1,g0)
    c: Diameter(g1) = 10.8
FEATURE [PartDesign::Pocket] Pocket001
  BaseFeature = -> Pocket
  Length = 1.5
  Length2 = 100
  Placement = pos=(0,0,0) rot=(1,0,0;1.5708rad)
  Profile = -> Sketch002
  Type = 0
FEATURE [Sketcher::SketchObject] Sketch003
  ExternalGeometry = -> [Pocket001]
  FullyConstrained = true
  MapMode = 5
  Placement = pos=(0,-20,4.4e-15) rot=(1,0,0;1.5708rad)
  Support = -> [Pocket001]
  sketch-geometry (1):
    g0: Circle CenterX=0 CenterY=25 CenterZ=0 NormalX=0 NormalY=0 NormalZ=1 AngleXU=0 Radius=13
  constraints (2):
    c: Coincident(g0,g-3)
    c: Diameter(g0) = 26
FEATURE [PartDesign::Pocket] Pocket002
  BaseFeature = -> Pocket001
  Length = 6
  Length2 = 100
  Placement = pos=(0,0,0) rot=(1,0,0;1.5708rad)
  Profile = -> Sketch003
  Type = 0
FEATURE [Sketcher::SketchObject] Sketch004
  ExternalGeometry = -> [Pocket002]
  FullyConstrained = true
  MapMode = 5
  Placement = pos=(0,0,0) rot=(-1,0,0;1.5708rad)
  Support = -> [Pocket002]
  sketch-geometry (1):
    g0: Circle CenterX=0 CenterY=-25 CenterZ=0 NormalX=0 NormalY=0 NormalZ=1 AngleXU=0 Radius=13
  constraints (2):
    c: Coincident(g0,g-3)
    c: Diameter(g0) = 26
FEATURE [PartDesign::Pocket] Pocket003
  BaseFeature = -> Pocket002
  Length = 6
  Length2 = 100
  Placement = pos=(0,0,0) rot=(1,0,0;1.5708rad)
  Profile = -> Sketch004
  Type = 0
FEATURE [PartDesign::CoordinateSystem] LCS_mount
  AttacherType = Attacher::AttachEngine3D
  AttachmentOffset = pos=(0,10,0) rot=(0,0,1;0rad)
  MapMode = 5
  Placement = pos=(0,-10,4.4e-15) rot=(1,0,0;3.14159rad)
  Support = -> [Pocket003]
FEATURE [PartDesign::CoordinateSystem] LCS_BB1
  AttacherType = Attacher::AttachEngine3D
  MapMode = 11
  Placement = pos=(0,-14,25) rot=(0.57735,-0.57735,-0.57735;4.18879rad)
  Support = -> [Pocket003]
FEATURE [PartDesign::CoordinateSystem] LCS_BB2
  AttacherType = Attacher::AttachEngine3D
  MapMode = 11
  Placement = pos=(0,-6,25) rot=(0.57735,-0.57735,-0.57735;4.18879rad)
  Support = -> [Pocket003]
FEATURE [PartDesign::Body] Body
  Group = -> [Sketch,Pad,Sketch001,Pocket,Sketch002,Pocket001,Sketch003,Pocket002,Sketch004,Pocket003,LCS_mount,LCS_BB1,LCS_BB2]
  Origin = -> Origin
  Tip = -> Pocket003
---- part BF12_PORTAL_SUPPORT.FCStd = doc fcstd_0ad096305de4 ----
FCSTD DOCUMENT  (FreeCAD 0.19R)
Label: BF12_PORTAL_SUPPORT
License: All rights reserved
LicenseURL: http://en.wikipedia.org/wiki/All_rights_reserved
objects: Sketcher::SketchObject×6, PartDesign::Pad×5, PartDesign::CoordinateSystem×2, PartDesign::Pocket×1, PartDesign::Body×1
note: 21 computed .brp shape members not serialized (recipe doc carries the construction recipe); baked Part::Feature solids carry a one-line shape summary decoded from their .brp

FEATURE [Sketcher::SketchObject] Sketch
  FullyConstrained = true
  MapMode = 5
  Placement = pos=(0,0,0) rot=(1,0,0;1.5708rad)
  Support = -> [XZ_Plane]
  sketch-geometry (4):
    g0: LineSegment StartX=-30 StartY=0 StartZ=0 EndX=30 EndY=0 EndZ=0
    g1: LineSegment StartX=30 StartY=0 StartZ=0 EndX=30 EndY=25.9 EndZ=0
    g2: LineSegment StartX=30 StartY=25.9 StartZ=0 EndX=-30 EndY=25.9 EndZ=0
    g3: LineSegment StartX=-30 StartY=25.9 StartZ=0 EndX=-30 EndY=0 EndZ=0
  constraints (11):
    c: Coincident(g0,g1)
    c: Coincident(g1,g2)
    c: Coincident(g2,g3)
    c: Coincident(g3,g0)
    c: Horizontal(g2)
    c: Vertical(g1)
    c: Vertical(g3)
    c: PointOnObject(g0,g-1)
    c: DistanceX(g0,g0) = 60
    c: Symmetric(g0,g0,g-2)
    c: DistanceY(g1,g1) = 25.9
FEATURE [PartDesign::Pad] Pad
  Direction = (1,1,1)
  Length = 20
  Length2 = 100
  Placement = pos=(0,0,0) rot=(1,0,0;1.5708rad)
  Profile = -> Sketch
  Type = 0
FEATURE [Sketcher::SketchObject] Sketch001
  FullyConstrained = true
  MapMode = 5
  Placement = pos=(0,0,25.9) rot=(0,0,1;3.14159rad)
  Support = -> [Pad]
  sketch-geometry (2):
    g0: Circle CenterX=-23 CenterY=10 CenterZ=0 NormalX=0 NormalY=0 NormalZ=1 AngleXU=0 Radius=3.5
    g1: Circle CenterX=23 CenterY=10 CenterZ=0 NormalX=0 NormalY=0 NormalZ=1 AngleXU=0 Radius=3.5
  constraints (5):
    c: Equal(g1,g0)
    c: Symmetric(g0,g1,g-2)
    c: DistanceY(g-1,g0) = 10
    c: Diameter(g1) = 7
    c: DistanceX(g0,g1) = 46
FEATURE [PartDesign::Pocket] Pocket
  BaseFeature = -> Pad
  Length = 5
  Length2 = 100
  Placement = pos=(0,0,0) rot=(1,0,0;1.5708rad)
  Profile = -> Sketch001
  Type = 1
FEATURE [PartDesign::CoordinateSystem] LCS_TUBE_MOUNT
  AttacherType = Attacher::AttachEngine3D
  AttachmentOffset = pos=(0,10,0) rot=(0,0,1;0rad)
  MapMode = 5
  Placement = pos=(0,-10,0) rot=(1,0,0;3.14159rad)
  Support = -> [Pocket]
FEATURE [PartDesign::CoordinateSystem] LCS_BF_MOUNT
  AttacherType = Attacher::AttachEngine3D
  AttachmentOffset = pos=(0,10,0) rot=(0,0,1;0rad)
  MapMode = 5
  Placement = pos=(0,-10,25.9) rot=(0,0,1;3.14159rad)
  Support = -> [Pocket]
FEATURE [Sketcher::SketchObject] Sketch002
  ExternalGeometry = -> [Pocket]
  FullyConstrained = true
  MapMode = 5
  Placement = pos=(30,0,0) rot=(0.707107,0,0.707107;3.14159rad)
  Support = -> [Pocket]
  sketch-geometry (4):
    g0: LineSegment StartX=-19.1 StartY=20 StartZ=0 EndX=25.9 EndY=20 EndZ=0
    g1: LineSegment StartX=25.9 StartY=20 StartZ=0 EndX=25.9 EndY=7.1e-15 EndZ=0
    g2: LineSegment StartX=25.9 StartY=7.1e-15 StartZ=0 EndX=-19.1 EndY=7.1e-15 EndZ=0
    g3: LineSegment StartX=-19.1 StartY=7.1e-15 StartZ=0 EndX=-19.1 EndY=20 EndZ=0
  constraints (10):
    c: Coincident(g0,g1)
    c: Coincident(g1,g2)
    c: Coincident(g2,g3)
    c: Coincident(g3,g0)
    c: Horizontal(g0)
    c: Horizontal(g2)
    c: Vertical(g3)
    c: Coincident(g1,g-4)
    c: Coincident(g0,g-3)
    c: DistanceX(g0,g0) = 45
FEATURE [PartDesign::Pad] Pad001
  BaseFeature = -> Pocket
  Direction = (1,1,1)
  Length = 10
  Length2 = 100
  Placement = pos=(0,0,0) rot=(1,0,0;1.5708rad)
  Profile = -> Sketch002
  Type = 0
FEATURE [Sketcher::SketchObject] Sketch003
  ExternalGeometry = -> [Pad001]
  FullyConstrained = true
  MapMode = 5
  Placement = pos=(-30,0,0) rot=(0.707107,0,-0.707107;3.14159rad)
  Support = -> [Pad001]
  sketch-geometry (4):
    g0: LineSegment StartX=19.1 StartY=0 StartZ=0 EndX=-25.9 EndY=0 EndZ=0
    g1: LineSegment StartX=-25.9 StartY=0 StartZ=0 EndX=-25.9 EndY=20 EndZ=0
    g2: LineSegment StartX=-25.9 StartY=20 StartZ=0 EndX=19.1 EndY=20 EndZ=0
    g3: LineSegment StartX=19.1 StartY=20 StartZ=0 EndX=19.1 EndY=0 EndZ=0
  constraints (11):
    c: Coincident(g0,g1)
    c: Coincident(g1,g2)
    c: Coincident(g2,g3)
    c: Coincident(g3,g0)
    c: Horizontal(g0)
    c: Horizontal(g2)
    c: Vertical(g1)
    c: Vertical(g3)
    c: PointOnObject(g0,g-1)
    c: Coincident(g1,g-4)
    c: DistanceX(g2,g2) = 45
FEATURE [PartDesign::Pad] Pad002
  BaseFeature = -> Pad001
  Direction = (1,1,1)
  Length = 10
  Length2 = 100
  Placement = pos=(0,0,0) rot=(1,0,0;1.5708rad)
  Profile = -> Sketch003
  Type = 0
FEATURE [Sketcher::SketchObject] Sketch004
  FullyConstrained = true
  MapMode = 5
  Placement = pos=(0,0,0) rot=(-1,0,0;1.5708rad)
  Support = -> [Pad002]
  sketch-geometry (4):
    g0: LineSegment StartX=-30 StartY=0 StartZ=0 EndX=30 EndY=0 EndZ=0
    g1: LineSegment StartX=30 StartY=0 StartZ=0 EndX=30 EndY=-15 EndZ=0
    g2: LineSegment StartX=30 StartY=-15 StartZ=0 EndX=-30 EndY=-15 EndZ=0
    g3: LineSegment StartX=-30 StartY=-15 StartZ=0 EndX=-30 EndY=0 EndZ=0
  constraints (11):
    c: Coincident(g0,g1)
    c: Coincident(g1,g2)
    c: Coincident(g2,g3)
    c: Coincident(g3,g0)
    c: Horizontal(g2)
    c: Vertical(g1)
    c: Vertical(g3)
    c: PointOnObject(g0,g-1)
    c: DistanceY(g1,g1) = 15
    c: DistanceX(g0,g0) = 60
    c: Symmetric(g0,g0,g-2)
FEATURE [PartDesign::Pad] Pad003
  BaseFeature = -> Pad002
  Direction = (1,1,1)
  Length = 18
  Length2 = 100
  Placement = pos=(0,0,0) rot=(1,0,0;1.5708rad)
  Profile = -> Sketch004
  Type = 0
FEATURE [Sketcher::SketchObject] Sketch005
  ExternalGeometry = -> [Pad003]
  FullyConstrained = true
  MapMode = 5
  Placement = pos=(-30,0,0) rot=(0.707107,0,-0.707107;3.14159rad)
  Support = -> [Pad003]
  sketch-geometry (3):
    g0: LineSegment StartX=-25.9 StartY=-9.4502e-12 StartZ=0 EndX=-15 EndY=3.6e-15 EndZ=0
    g1: LineSegment StartX=-15 StartY=-18 StartZ=0 EndX=-15 EndY=3.6e-15 EndZ=0
    g2: ArcOfCircle CenterX=-32.9427 CenterY=-16.565 CenterZ=0 NormalX=0 NormalY=0 NormalZ=1 AngleXU=0 Radius=18 StartAngle=6.20338 EndAngle=7.45198
  constraints (7):
    c: Coincident(g0,g-4)
    c: Coincident(g0,g-3)
    c: Coincident(g1,g-3)
    c: Coincident(g1,g0)
    c: Coincident(g2,g1)
    c: Coincident(g2,g0)
    c: Radius(g2) = 18
FEATURE [PartDesign::Pad] Pad004
  BaseFeature = -> Pad003
  Direction = (1,1,1)
  Length = 60
  Length2 = 100
  Placement = pos=(0,0,0) rot=(1,0,0;1.5708rad)
  Profile = -> Sketch005
  Reversed = true
  Type = 0
FEATURE [PartDesign::Body] Body
  Group = -> [Sketch,Pad,Sketch001,Pocket,LCS_TUBE_MOUNT,LCS_BF_MOUNT,Sketch002,Pad001,Sketch003,Pad002,Sketch004,Pad003,Sketch005,Pad004]
  Origin = -> Origin
  Tip = -> Pad004
---- part BF12_SUPPORT.FCStd = doc fcstd_6789d39b52a2 ----
FCSTD DOCUMENT  (FreeCAD 0.19R)
Label: BF12_SUPPORT
License: All rights reserved
LicenseURL: http://en.wikipedia.org/wiki/All_rights_reserved
objects: Sketcher::SketchObject×4, PartDesign::Pad×3, PartDesign::CoordinateSystem×2, PartDesign::Pocket×1, PartDesign::Body×1
note: 15 computed .brp shape members not serialized (recipe doc carries the construction recipe); baked Part::Feature solids carry a one-line shape summary decoded from their .brp

FEATURE [Sketcher::SketchObject] Sketch
  FullyConstrained = true
  MapMode = 5
  Placement = pos=(0,0,0) rot=(1,0,0;1.5708rad)
  Support = -> [XZ_Plane]
  sketch-geometry (4):
    g0: LineSegment StartX=-30 StartY=0 StartZ=0 EndX=30 EndY=0 EndZ=0
    g1: LineSegment StartX=30 StartY=0 StartZ=0 EndX=30 EndY=36 EndZ=0
    g2: LineSegment StartX=30 StartY=36 StartZ=0 EndX=-30 EndY=36 EndZ=0
    g3: LineSegment StartX=-30 StartY=36 StartZ=0 EndX=-30 EndY=0 EndZ=0
  constraints (11):
    c: Coincident(g0,g1)
    c: Coincident(g1,g2)
    c: Coincident(g2,g3)
    c: Coincident(g3,g0)
    c: Horizontal(g2)
    c: Vertical(g1)
    c: Vertical(g3)
    c: PointOnObject(g0,g-1)
    c: DistanceX(g0,g0) = 60
    c: Symmetric(g0,g0,g-2)
    c: DistanceY(g1,g1) = 36
FEATURE [PartDesign::Pad] Pad
  Direction = (1,1,1)
  Length = 20
  Length2 = 100
  Placement = pos=(0,0,0) rot=(1,0,0;1.5708rad)
  Profile = -> Sketch
  Type = 0
FEATURE [Sketcher::SketchObject] Sketch001
  FullyConstrained = true
  MapMode = 5
  Placement = pos=(0,0,36) rot=(0,0,1;3.14159rad)
  Support = -> [Pad]
  sketch-geometry (2):
    g0: Circle CenterX=-23 CenterY=10 CenterZ=0 NormalX=0 NormalY=0 NormalZ=1 AngleXU=0 Radius=3.5
    g1: Circle CenterX=23 CenterY=10 CenterZ=0 NormalX=0 NormalY=0 NormalZ=1 AngleXU=0 Radius=3.5
  constraints (5):
    c: Equal(g1,g0)
    c: Symmetric(g0,g1,g-2)
    c: DistanceY(g-1,g0) = 10
    c: Diameter(g1) = 7
    c: DistanceX(g0,g1) = 46
FEATURE [PartDesign::Pocket] Pocket
  BaseFeature = -> Pad
  Length = 5
  Length2 = 100
  Placement = pos=(0,0,0) rot=(1,0,0;1.5708rad)
  Profile = -> Sketch001
  Type = 1
FEATURE [PartDesign::CoordinateSystem] LCS_TUBE_MOUNT
  AttacherType = Attacher::AttachEngine3D
  AttachmentOffset = pos=(0,10,0) rot=(0,0,1;0rad)
  MapMode = 5
  Placement = pos=(0,-10,0) rot=(1,0,0;3.14159rad)
  Support = -> [Pocket]
FEATURE [PartDesign::CoordinateSystem] LCS_BF_MOUNT
  AttacherType = Attacher::AttachEngine3D
  AttachmentOffset = pos=(0,10,0) rot=(0,0,1;0rad)
  MapMode = 5
  Placement = pos=(0,-10,36) rot=(0,0,1;3.14159rad)
  Support = -> [Pocket]
FEATURE [Sketcher::SketchObject] Sketch004
  FullyConstrained = true
  MapMode = 5
  Placement = pos=(0,-20,-4e-15) rot=(1,0,0;1.5708rad)
  sketch-geometry (4):
    g0: LineSegment StartX=-30 StartY=0 StartZ=0 EndX=30 EndY=0 EndZ=0
    g1: LineSegment StartX=30 StartY=0 StartZ=0 EndX=30 EndY=15 EndZ=0
    g2: LineSegment StartX=30 StartY=15 StartZ=0 EndX=-30 EndY=15 EndZ=0
    g3: LineSegment StartX=-30 StartY=15 StartZ=0 EndX=-30 EndY=0 EndZ=0
  constraints (11):
    c: Coincident(g0,g1)
    c: Coincident(g1,g2)
    c: Coincident(g2,g3)
    c: Coincident(g3,g0)
    c: Horizontal(g2)
    c: Vertical(g1)
    c: Vertical(g3)
    c: PointOnObject(g0,g-1)
    c: DistanceY(g1,g1) = 15
    c: DistanceX(g2,g2) = 60
    c: Symmetric(g0,g0,g-2)
FEATURE [PartDesign::Pad] Pad003
  BaseFeature = -> Pocket
  Direction = (1,1,1)
  Length = 13
  Length2 = 100
  Placement = pos=(0,0,0) rot=(1,0,0;1.5708rad)
  Profile = -> Sketch004
  Type = 0
FEATURE [Sketcher::SketchObject] Sketch005
  ExternalGeometry = -> [Pad003]
  FullyConstrained = true
  MapMode = 5
  Placement = pos=(-30,0,0) rot=(0.707107,0,-0.707107;3.14159rad)
  Support = -> [Pad003]
  sketch-geometry (3):
    g0: LineSegment StartX=-25 StartY=20 StartZ=0 EndX=-15 EndY=20 EndZ=0
    g1: LineSegment StartX=-15 StartY=20 StartZ=0 EndX=-15 EndY=32 EndZ=0
    g2: ArcOfCircle CenterX=-28.9259 CenterY=33.4383 CenterZ=0 NormalX=0 NormalY=0 NormalZ=1 AngleXU=0 Radius=14 StartAngle=4.99662 EndAngle=6.18027
  constraints (9):
    c: Coincident(g0,g-4)
    c: Coincident(g0,g1)
    c: PointOnObject(g0,g-4)
    c: PointOnObject(g1,g-3)
    c: Coincident(g2,g0)
    c: Coincident(g2,g1)
    c: DistanceX(g0,g0) = 10
    c: DistanceY(g1,g1) = 12
    c: Radius(g2) = 14
FEATURE [PartDesign::Pad] Pad004
  BaseFeature = -> Pad003
  Direction = (1,1,1)
  Length = 60
  Length2 = 100
  Placement = pos=(0,0,0) rot=(1,0,0;1.5708rad)
  Profile = -> Sketch005
  Reversed = true
  Type = 0
FEATURE [PartDesign::Body] Body
  Group = -> [Sketch,Pad,Sketch001,Pocket,LCS_TUBE_MOUNT,LCS_BF_MOUNT,Sketch004,Pad003,Sketch005,Pad004]
  Origin = -> Origin
  Tip = -> Pad004
---- part BK12.FCStd = doc fcstd_9a65693fc990 ----
FCSTD DOCUMENT  (FreeCAD 0.19R)
Label: BK12
License: All rights reserved
LicenseURL: http://en.wikipedia.org/wiki/All_rights_reserved
objects: Sketcher::SketchObject×5, PartDesign::Pocket×3, PartDesign::Pad×2, PartDesign::CoordinateSystem×2, PartDesign::Body×1
note: 18 computed .brp shape members not serialized (recipe doc carries the construction recipe); baked Part::Feature solids carry a one-line shape summary decoded from their .brp

FEATURE [Sketcher::SketchObject] Sketch
  FullyConstrained = true
  MapMode = 5
  Placement = pos=(0,0,0) rot=(1,0,0;1.5708rad)
  Support = -> [XZ_Plane]
  sketch-geometry (12):
    g0: LineSegment StartX=-30 StartY=32.5 StartZ=0 EndX=-30 EndY=0 EndZ=0
    g1: LineSegment StartX=-30 StartY=0 StartZ=0 EndX=30 EndY=0 EndZ=0
    g2: LineSegment StartX=30 StartY=0 StartZ=0 EndX=30 EndY=32.5 EndZ=0
    g3: LineSegment StartX=-30 StartY=32.5 StartZ=0 EndX=-17 EndY=32.5 EndZ=0
    g4: LineSegment StartX=-17 StartY=32.5 StartZ=0 EndX=-17 EndY=43 EndZ=0
    g5: LineSegment StartX=-17 StartY=43 StartZ=0 EndX=17 EndY=43 EndZ=0
    g6: LineSegment StartX=17 StartY=43 StartZ=0 EndX=17 EndY=32.5 EndZ=0
    g7: LineSegment StartX=17 StartY=32.5 StartZ=0 EndX=30 EndY=32.5 EndZ=0
    g8: Circle CenterX=-23 CenterY=25 CenterZ=0 NormalX=0 NormalY=0 NormalZ=1 AngleXU=0 Radius=2.75
    g9: Circle CenterX=-23 CenterY=7 CenterZ=0 NormalX=0 NormalY=0 NormalZ=1 AngleXU=0 Radius=2.75
    g10: Circle CenterX=23 CenterY=7 CenterZ=0 NormalX=0 NormalY=0 NormalZ=1 AngleXU=0 Radius=2.75
    g11: Circle CenterX=23 CenterY=25 CenterZ=0 NormalX=0 NormalY=0 NormalZ=1 AngleXU=0 Radius=2.75
  constraints (33):
    c: PointOnObject(g0,g-1)
    c: Vertical(g0)
    c: Coincident(g1,g0)
    c: Coincident(g2,g1)
    c: Vertical(g2)
    c: Coincident(g3,g0)
    c: Horizontal(g3)
    c: Coincident(g4,g3)
    c: Vertical(g4)
    c: Coincident(g5,g4)
    c: Horizontal(g5)
    c: Coincident(g6,g5)
    c: Vertical(g6)
    c: Coincident(g7,g6)
    c: Coincident(g7,g2)
    c: Horizontal(g7)
    c: Equal(g3,g7)
    c: Equal(g6,g4)
    c: DistanceY(g2,g2) = 32.5
    c: Symmetric(g0,g1,g-2)
    c: DistanceY(g-1,g4) = 43
    c: DistanceX(g0,g1) = 60
    c: DistanceX(g5,g5) = 34
    c: Equal(g11,g10)
    c: Equal(g10,g9)
    c: Equal(g9,g8)
    c: Symmetric(g9,g10,g-2)
    c: Symmetric(g8,g11,g-2)
    c: Diameter(g9) = 5.5
    c: DistanceX(g9,g10) = 46
    c: DistanceX(g8,g11) = 46
    c: DistanceY(g9,g8) = 18
    c: DistanceY(g1,g11) = 25
FEATURE [PartDesign::Pad] Pad
  Direction = (1,1,1)
  Length = 25
  Length2 = 100
  Placement = pos=(0,0,0) rot=(1,0,0;1.5708rad)
  Profile = -> Sketch
  Type = 0
FEATURE [Sketcher::SketchObject] Sketch001
  ExternalGeometry = -> [Pad]
  FullyConstrained = true
  MapMode = 5
  Placement = pos=(0,-25,5.5e-15) rot=(1,0,0;1.5708rad)
  Support = -> [Pad]
  sketch-geometry (4):
    g0: LineSegment StartX=-17 StartY=43 StartZ=0 EndX=17 EndY=43 EndZ=0
    g1: LineSegment StartX=17 StartY=43 StartZ=0 EndX=17 EndY=9 EndZ=0
    g2: LineSegment StartX=17 StartY=9 StartZ=0 EndX=-17 EndY=9 EndZ=0
    g3: LineSegment StartX=-17 StartY=9 StartZ=0 EndX=-17 EndY=43 EndZ=0
  constraints (10):
    c: Coincident(g0,g1)
    c: Coincident(g1,g2)
    c: Coincident(g2,g3)
    c: Coincident(g3,g0)
    c: Horizontal(g2)
    c: Vertical(g1)
    c: Vertical(g3)
    c: Coincident(g0,g-3)
    c: Coincident(g0,g-3)
    c: DistanceY(g1,g1) = 34
FEATURE [PartDesign::Pad] Pad001
  BaseFeature = -> Pad
  Direction = (1,1,1)
  Length = 5
  Length2 = 100
  Placement = pos=(0,0,0) rot=(1,0,0;1.5708rad)
  Profile = -> Sketch001
  Type = 0
FEATURE [Sketcher::SketchObject] Sketch002
  FullyConstrained = true
  MapMode = 5
  Placement = pos=(0,-30,2.19e-14) rot=(1,0,0;1.5708rad)
  Support = -> [Pad001]
  sketch-geometry (1):
    g0: Circle CenterX=0 CenterY=25 CenterZ=0 NormalX=0 NormalY=0 NormalZ=1 AngleXU=0 Radius=6
  constraints (3):
    c: PointOnObject(g0,g-2)
    c: Diameter(g0) = 12
    c: DistanceY(g-1,g0) = 25
FEATURE [PartDesign::Pocket] Pocket
  BaseFeature = -> Pad001
  Length = 5
  Length2 = 100
  Placement = pos=(0,0,0) rot=(1,0,0;1.5708rad)
  Profile = -> Sketch002
  Type = 1
FEATURE [Sketcher::SketchObject] Sketch003
  FullyConstrained = true
  MapMode = 5
  Placement = pos=(0,0,0) rot=(1,0,0;3.14159rad)
  Support = -> [Pocket]
  sketch-geometry (4):
    g0: Circle CenterX=-23 CenterY=19 CenterZ=0 NormalX=0 NormalY=0 NormalZ=1 AngleXU=0 Radius=3.3
    g1: Circle CenterX=-23 CenterY=6 CenterZ=0 NormalX=0 NormalY=0 NormalZ=1 AngleXU=0 Radius=3.3
    g2: Circle CenterX=23 CenterY=6 CenterZ=0 NormalX=0 NormalY=0 NormalZ=1 AngleXU=0 Radius=3.3
    g3: Circle CenterX=23 CenterY=19 CenterZ=0 NormalX=0 NormalY=0 NormalZ=1 AngleXU=0 Radius=3.3
  constraints (10):
    c: Symmetric(g0,g3,g-2)
    c: Symmetric(g1,g2,g-2)
    c: Equal(g1,g0)
    c: Equal(g0,g3)
    c: Equal(g3,g2)
    c: Diameter(g3) = 6.6
    c: DistanceX(g1,g2) = 46
    c: DistanceX(g0,g3) = 46
    c: DistanceY(g-1,g2) = 6
    c: DistanceY(g2,g3) = 13
FEATURE [PartDesign::Pocket] Pocket001
  BaseFeature = -> Pocket
  Length = 5
  Length2 = 100
  Placement = pos=(0,0,0) rot=(1,0,0;1.5708rad)
  Profile = -> Sketch003
  Type = 1
FEATURE [Sketcher::SketchObject] Sketch004
  ExternalGeometry = -> [Pocket001]
  FullyConstrained = true
  MapMode = 5
  Placement = pos=(0,1.43e-14,32.5) rot=(0,0,1;3.14159rad)
  Support = -> [Pocket001]
  sketch-geometry (4):
    g0: Circle CenterX=-23 CenterY=19 CenterZ=0 NormalX=0 NormalY=0 NormalZ=1 AngleXU=0 Radius=5.4
    g1: Circle CenterX=-23 CenterY=6 CenterZ=0 NormalX=0 NormalY=0 NormalZ=1 AngleXU=0 Radius=5.4
    g2: Circle CenterX=23 CenterY=6 CenterZ=0 NormalX=0 NormalY=0 NormalZ=1 AngleXU=0 Radius=5.4
    g3: Circle CenterX=23 CenterY=19 CenterZ=0 NormalX=0 NormalY=0 NormalZ=1 AngleXU=0 Radius=5.4
  constraints (8):
    c: Coincident(g0,g-4)
    c: Coincident(g1,g-3)
    c: Coincident(g2,g-6)
    c: Coincident(g3,g-5)
    c: Equal(g3,g0)
    c: Equal(g0,g1)
    c: Equal(g1,g2)
    c: Diameter(g3) = 10.8
FEATURE [PartDesign::Pocket] Pocket002
  BaseFeature = -> Pocket001
  Length = 1.5
  Length2 = 100
  Placement = pos=(0,0,0) rot=(1,0,0;1.5708rad)
  Profile = -> Sketch004
  Type = 0
FEATURE [PartDesign::CoordinateSystem] LCS_mount
  AttacherType = Attacher::AttachEngine3D
  MapMode = 11
  Placement = pos=(0,3.2e-14,25) rot=(0.57735,-0.57735,0.57735;2.0944rad)
  Support = -> [Pocket002]
FEATURE [PartDesign::CoordinateSystem] LCS_H1
  AttacherType = Attacher::AttachEngine3D
  MapMode = 11
  Placement = pos=(23,-19,3.8e-14) rot=(0.707107,-0.707107,0;3.14159rad)
  Support = -> [Pocket002]
FEATURE [PartDesign::Body] Body
  Group = -> [Sketch,Pad,Sketch001,Pad001,Sketch002,Pocket,Sketch003,Pocket001,Sketch004,Pocket002,LCS_mount,LCS_H1]
  Origin = -> Origin
  Tip = -> Pocket002
---- part BK12_PORTAL_SUPPORT.FCStd = doc fcstd_e831557240d2 ----
FCSTD DOCUMENT  (FreeCAD 0.19R)
Label: BK12_PORTAL_SUPPORT
License: All rights reserved
LicenseURL: http://en.wikipedia.org/wiki/All_rights_reserved
objects: Sketcher::SketchObject×11, PartDesign::Pad×8, PartDesign::Pocket×3, PartDesign::CoordinateSystem×1, PartDesign::Body×1
note: 35 computed .brp shape members not serialized (recipe doc carries the construction recipe); baked Part::Feature solids carry a one-line shape summary decoded from their .brp

FEATURE [Sketcher::SketchObject] Sketch
  FullyConstrained = true
  MapMode = 5
  Support = -> [XY_Plane]
  sketch-geometry (8):
    g0: LineSegment StartX=-30 StartY=12.5 StartZ=0 EndX=30 EndY=12.5 EndZ=0
    g1: LineSegment StartX=30 StartY=12.5 StartZ=0 EndX=30 EndY=-12.5 EndZ=0
    g2: LineSegment StartX=30 StartY=-12.5 StartZ=0 EndX=-30 EndY=-12.5 EndZ=0
    g3: LineSegment StartX=-30 StartY=-12.5 StartZ=0 EndX=-30 EndY=12.5 EndZ=0
    g4: Circle CenterX=-23 CenterY=6.5 CenterZ=0 NormalX=0 NormalY=0 NormalZ=1 AngleXU=0 Radius=3.3
    g5: Circle CenterX=-23 CenterY=-6.5 CenterZ=0 NormalX=0 NormalY=0 NormalZ=1 AngleXU=0 Radius=3.3
    g6: Circle CenterX=23 CenterY=-6.5 CenterZ=0 NormalX=0 NormalY=0 NormalZ=1 AngleXU=0 Radius=3.3
    g7: Circle CenterX=23 CenterY=6.5 CenterZ=0 NormalX=0 NormalY=0 NormalZ=1 AngleXU=0 Radius=3.3
  constraints (20):
    c: Coincident(g0,g1)
    c: Coincident(g1,g2)
    c: Coincident(g2,g3)
    c: Coincident(g3,g0)
    c: Horizontal(g0)
    c: Vertical(g1)
    c: DistanceX(g2,g2) = 60
    c: DistanceY(g3,g3) = 25
    c: Symmetric(g2,g0,g-1)
    c: Symmetric(g2,g1,g-2)
    c: Symmetric(g4,g7,g-2)
    c: Symmetric(g5,g6,g-2)
    c: DistanceX(g4,g7) = 46
    c: DistanceX(g5,g6) = 46
    c: Equal(g6,g7)
    c: Equal(g7,g4)
    c: Equal(g4,g5)
    c: Diameter(g7) = 6.6
    c: DistanceY(g7,g0) = 6
    c: DistanceY(g6,g7) = 13
FEATURE [PartDesign::Pad] Pad
  Direction = (1,1,1)
  Length = 25.9
  Length2 = 100
  Profile = -> Sketch
  Type = 0
FEATURE [PartDesign::CoordinateSystem] LCS_M1
  AttacherType = Attacher::AttachEngine3D
  MapMode = 11
  Placement = pos=(-23,6.5,25.9) rot=(0,0,1;1.5708rad)
  Support = -> [Pad]
FEATURE [Sketcher::SketchObject] Sketch001
  ExternalGeometry = -> [Pad]
  FullyConstrained = true
  MapMode = 5
  Placement = pos=(0,12.5,0) rot=(0,0.707107,0.707107;3.14159rad)
  Support = -> [Pad]
  sketch-geometry (4):
    g0: LineSegment StartX=-30 StartY=11.1 StartZ=0 EndX=30 EndY=11.1 EndZ=0
    g1: LineSegment StartX=30 StartY=11.1 StartZ=0 EndX=30 EndY=0 EndZ=0
    g2: LineSegment StartX=30 StartY=0 StartZ=0 EndX=-30 EndY=0 EndZ=0
    g3: LineSegment StartX=-30 StartY=0 StartZ=0 EndX=-30 EndY=11.1 EndZ=0
  constraints (10):
    c: Coincident(g0,g1)
    c: Coincident(g1,g2)
    c: Coincident(g2,g3)
    c: Coincident(g3,g0)
    c: Horizontal(g0)
    c: Vertical(g1)
    c: Vertical(g3)
    c: Coincident(g1,g-3)
    c: Coincident(g2,g-3)
    c: DistanceY(g3,g3) = 11.1
FEATURE [PartDesign::Pad] Pad001
  BaseFeature = -> Pad
  Direction = (1,1,1)
  Length = 127
  Length2 = 100
  Profile = -> Sketch001
  Type = 0
FEATURE [Sketcher::SketchObject] Sketch002
  ExternalGeometry = -> [Pad001]
  FullyConstrained = true
  MapMode = 5
  Placement = pos=(0,2.4e-15,11.1) rot=(0,0,1;0rad)
  Support = -> [Pad001]
  sketch-geometry (4):
    g0: Circle CenterX=-20 CenterY=124.5 CenterZ=0 NormalX=0 NormalY=0 NormalZ=1 AngleXU=0 Radius=2.5
    g1: Circle CenterX=20 CenterY=124.5 CenterZ=0 NormalX=0 NormalY=0 NormalZ=1 AngleXU=0 Radius=2.5
    g2: Circle CenterX=-20 CenterY=90.5 CenterZ=0 NormalX=0 NormalY=0 NormalZ=1 AngleXU=0 Radius=2.5
    g3: Circle CenterX=20 CenterY=90.5 CenterZ=0 NormalX=0 NormalY=0 NormalZ=1 AngleXU=0 Radius=2.5
  constraints (10):
    c: Equal(g1,g0)
    c: Equal(g0,g2)
    c: Equal(g2,g3)
    c: Diameter(g3) = 5
    c: Symmetric(g3,g2,g-2)
    c: Symmetric(g1,g0,g-2)
    c: DistanceX(g2,g3) = 40
    c: DistanceX(g0,g1) = 40
    c: DistanceY(g1,g-3) = 15
    c: DistanceY(g2,g0) = 34
FEATURE [PartDesign::Pocket] Pocket
  BaseFeature = -> Pad001
  Length = 5
  Length2 = 100
  Profile = -> Sketch002
  Type = 1
FEATURE [Sketcher::SketchObject] Sketch003
  ExternalGeometry = -> [Pocket]
  FullyConstrained = true
  MapMode = 5
  Placement = pos=(30,0,0) rot=(0.57735,0.57735,0.57735;2.0944rad)
  Support = -> [Pocket]
  sketch-geometry (3):
    g0: LineSegment StartX=12.5 StartY=25.9 StartZ=0 EndX=32.5 EndY=11.1 EndZ=0
    g1: LineSegment StartX=12.5 StartY=25.9 StartZ=0 EndX=12.5 EndY=0 EndZ=0
    g2: LineSegment StartX=12.5 StartY=0 StartZ=0 EndX=32.5 EndY=11.1 EndZ=0
  constraints (7):
    c: Coincident(g0,g-3)
    c: DistanceX(g-3,g0) = 20
    c: Coincident(g1,g0)
    c: Coincident(g1,g-4)
    c: Coincident(g2,g1)
    c: Coincident(g2,g0)
    c: PointOnObject(g0,g-5)
FEATURE [PartDesign::Pad] Pad002
  BaseFeature = -> Pocket
  Direction = (1,1,1)
  Length = 60
  Length2 = 100
  Profile = -> Sketch003
  Reversed = true
  Type = 0
FEATURE [Sketcher::SketchObject] Sketch004
  ExternalGeometry = -> [Pad002]
  FullyConstrained = true
  MapMode = 5
  Placement = pos=(30,0,0) rot=(0.57735,0.57735,0.57735;2.0944rad)
  Support = -> [Pad002]
  sketch-geometry (4):
    g0: LineSegment StartX=-12.5 StartY=-21 StartZ=0 EndX=139.5 EndY=-21 EndZ=0
    g1: LineSegment StartX=139.5 StartY=-21 StartZ=0 EndX=139.5 EndY=11.1 EndZ=0
    g2: LineSegment StartX=139.5 StartY=11.1 StartZ=0 EndX=-12.5 EndY=11.1 EndZ=0
    g3: LineSegment StartX=-12.5 StartY=11.1 StartZ=0 EndX=-12.5 EndY=-21 EndZ=0
  constraints (11):
    c: Coincident(g0,g1)
    c: Coincident(g1,g2)
    c: Coincident(g2,g3)
    c: Coincident(g3,g0)
    c: Horizontal(g2)
    c: Vertical(g1)
    c: Vertical(g3)
    c: DistanceY(g1,g1) = 32.1
    c: Coincident(g1,g-5)
    c: Horizontal(g0)
    c: PointOnObject(g-3,g3)
FEATURE [PartDesign::Pad] Pad003
  BaseFeature = -> Pad002
  Direction = (1,1,1)
  Length = 10
  Length2 = 100
  Profile = -> Sketch004
  Type = 0
FEATURE [Sketcher::SketchObject] Sketch005
  ExternalGeometry = -> [Pad003]
  FullyConstrained = true
  MapMode = 5
  Placement = pos=(-30,0,0) rot=(0.57735,-0.57735,-0.57735;2.0944rad)
  Support = -> [Pad003]
  sketch-geometry (4):
    g0: LineSegment StartX=-139.5 StartY=11.1 StartZ=0 EndX=12.5 EndY=11.1 EndZ=0
    g1: LineSegment StartX=12.5 StartY=11.1 StartZ=0 EndX=12.5 EndY=-21 EndZ=0
    g2: LineSegment StartX=12.5 StartY=-21 StartZ=0 EndX=-139.5 EndY=-21 EndZ=0
    g3: LineSegment StartX=-139.5 StartY=-21 StartZ=0 EndX=-139.5 EndY=11.1 EndZ=0
  constraints (11):
    c: Coincident(g0,g1)
    c: Coincident(g1,g2)
    c: Coincident(g2,g3)
    c: Coincident(g3,g0)
    c: Horizontal(g0)
    c: Horizontal(g2)
    c: Vertical(g1)
    c: Vertical(g3)
    c: Coincident(g0,g-3)
    c: PointOnObject(g-4,g1)
    c: DistanceY(g1,g1) = 32.1
FEATURE [PartDesign::Pad] Pad004
  BaseFeature = -> Pad003
  Direction = (1,1,1)
  Length = 10
  Length2 = 100
  Profile = -> Sketch005
  Type = 0
FEATURE [Sketcher::SketchObject] Sketch006
  ExternalGeometry = -> [Pad004]
  FullyConstrained = true
  MapMode = 5
  Placement = pos=(0,-12.5,0) rot=(1,0,0;1.5708rad)
  Support = -> [Pad004]
  sketch-geometry (6):
    g0: LineSegment StartX=40 StartY=11.1 StartZ=0 EndX=30 EndY=11.1 EndZ=0
    g1: LineSegment StartX=30 StartY=25.9 StartZ=0 EndX=40 EndY=11.1 EndZ=0
    g2: LineSegment StartX=30 StartY=25.9 StartZ=0 EndX=30 EndY=11.1 EndZ=0
    g3: LineSegment StartX=-30 StartY=25.9 StartZ=0 EndX=-30 EndY=11.1 EndZ=0
    g4: LineSegment StartX=-30 StartY=11.1 StartZ=0 EndX=-40 EndY=11.1 EndZ=0
    g5: LineSegment StartX=-40 StartY=11.1 StartZ=0 EndX=-30 EndY=25.9 EndZ=0
  constraints (12):
    c: Coincident(g0,g-6)
    c: Coincident(g0,g-6)
    c: Coincident(g1,g-5)
    c: Coincident(g1,g0)
    c: Coincident(g2,g1)
    c: Coincident(g2,g0)
    c: Coincident(g3,g-4)
    c: Coincident(g3,g-4)
    c: Coincident(g4,g3)
    c: Coincident(g4,g-3)
    c: Coincident(g5,g4)
    c: Coincident(g5,g3)
FEATURE [PartDesign::Pad] Pad005
  BaseFeature = -> Pad004
  Direction = (1,1,1)
  Length = 25
  Length2 = 100
  Profile = -> Sketch006
  Reversed = true
  Type = 0
FEATURE [Sketcher::SketchObject] Sketch007
  ExternalGeometry = -> [Pad005]
  FullyConstrained = true
  MapMode = 5
  Placement = pos=(40,0,0) rot=(0.57735,0.57735,0.57735;2.0944rad)
  Support = -> [Pad005]
  sketch-geometry (4):
    g0: LineSegment StartX=16.5 StartY=-21 StartZ=0 EndX=66.5 EndY=-21 EndZ=0
    g1: LineSegment StartX=66.5 StartY=-21 StartZ=0 EndX=66.5 EndY=-3 EndZ=0
    g2: LineSegment StartX=66.5 StartY=-3 StartZ=0 EndX=16.5 EndY=-3 EndZ=0
    g3: LineSegment StartX=16.5 StartY=-3 StartZ=0 EndX=16.5 EndY=-21 EndZ=0
  constraints (12):
    c: Coincident(g0,g1)
    c: Coincident(g1,g2)
    c: Coincident(g2,g3)
    c: Coincident(g3,g0)
    c: Horizontal(g0)
    c: Horizontal(g2)
    c: Vertical(g1)
    c: Vertical(g3)
    c: PointOnObject(g0,g-4)
    c: DistanceX(g2,g2) = 50
    c: DistanceY(g1,g1) = 18
    c: DistanceX(g-4,g0) = 29
FEATURE [PartDesign::Pocket] Pocket001
  BaseFeature = -> Pad005
  Length = 10
  Length2 = 100
  Profile = -> Sketch007
  Type = 0
FEATURE [Sketcher::SketchObject] Sketch008
  ExternalGeometry = -> [Pocket001]
  FullyConstrained = true
  MapMode = 5
  Placement = pos=(-40,0,0) rot=(0.57735,-0.57735,-0.57735;2.0944rad)
  Support = -> [Pocket001]
  sketch-geometry (2):
    g0: ArcOfCircle CenterX=-41.298 CenterY=-23 CenterZ=0 NormalX=0 NormalY=0 NormalZ=1 AngleXU=0 Radius=10 StartAngle=0.201358 EndAngle=2.94023
    g1: LineSegment StartX=-51.0959 StartY=-21 StartZ=0 EndX=-31.5 EndY=-21 EndZ=0
  constraints (7):
    c: PointOnObject(g0,g-4)
    c: PointOnObject(g0,g-4)
    c: Diameter(g0) = 20
    c: DistanceX(g0,g-4) = 44
    c: Coincident(g1,g0)
    c: Coincident(g1,g0)
    c: DistanceY(g0,g0) = 2
FEATURE [PartDesign::Pocket] Pocket002
  BaseFeature = -> Pocket001
  Length = 10
  Length2 = 100
  Profile = -> Sketch008
  Type = 0
FEATURE [Sketcher::SketchObject] Sketch009
  FullyConstrained = true
  MapMode = 5
  Placement = pos=(0,-12.5,0) rot=(1,0,0;1.5708rad)
  Support = -> [Pocket002]
  sketch-geometry (4):
    g0: LineSegment StartX=-30 StartY=0 StartZ=0 EndX=30 EndY=0 EndZ=0
    g1: LineSegment StartX=30 StartY=0 StartZ=0 EndX=30 EndY=15 EndZ=0
    g2: LineSegment StartX=30 StartY=15 StartZ=0 EndX=-30 EndY=15 EndZ=0
    g3: LineSegment StartX=-30 StartY=15 StartZ=0 EndX=-30 EndY=0 EndZ=0
  constraints (11):
    c: Coincident(g0,g1)
    c: Coincident(g1,g2)
    c: Coincident(g2,g3)
    c: Coincident(g3,g0)
    c: Horizontal(g2)
    c: Vertical(g1)
    c: Vertical(g3)
    c: PointOnObject(g0,g-1)
    c: DistanceX(g0,g0) = 60
    c: Symmetric(g0,g0,g-2)
    c: DistanceY(g1,g1) = 15
FEATURE [PartDesign::Pad] Pad006
  BaseFeature = -> Pocket002
  Direction = (1,1,1)
  Length = 27
  Length2 = 100
  Profile = -> Sketch009
  Type = 0
FEATURE [Sketcher::SketchObject] Sketch010
  ExternalGeometry = -> [Pad006]
  FullyConstrained = true
  MapMode = 5
  Placement = pos=(30,0,0) rot=(0.57735,0.57735,0.57735;2.0944rad)
  Support = -> [Pad006]
  sketch-geometry (3):
    g0: LineSegment StartX=-32.5 StartY=15 StartZ=0 EndX=-12.5 EndY=15 EndZ=0
    g1: LineSegment StartX=-12.5 StartY=15 StartZ=0 EndX=-12.5 EndY=25.9 EndZ=0
    g2: LineSegment StartX=-32.5 StartY=15 StartZ=0 EndX=-12.5 EndY=25.9 EndZ=0
  constraints (7):
    c: PointOnObject(g0,g-3)
    c: Coincident(g0,g-3)
    c: Coincident(g1,g0)
    c: Coincident(g1,g-4)
    c: Coincident(g2,g0)
    c: Coincident(g2,g1)
    c: DistanceX(g0,g0) = 20
FEATURE [PartDesign::Pad] Pad007
  BaseFeature = -> Pad006
  Direction = (1,1,1)
  Length = 60
  Length2 = 100
  Profile = -> Sketch010
  Reversed = true
  Type = 0
FEATURE [PartDesign::Body] Body
  Group = -> [Sketch,Pad,LCS_M1,Sketch001,Pad001,Sketch002,Pocket,Sketch003,Pad002,Sketch004,Pad003,Sketch005,Pad004,Sketch006,Pad005,Sketch007,Pocket001,Sketch008,Pocket002,Sketch009,Pad006,Sketch010,Pad007]
  Origin = -> Origin
  Tip = -> Pad007
---- part BK12_SUPPORT.FCStd = doc fcstd_1376fcdf5ffd ----
FCSTD DOCUMENT  (FreeCAD 0.19R)
Label: BK12_SUPPORT
License: All rights reserved
LicenseURL: http://en.wikipedia.org/wiki/All_rights_reserved
objects: Sketcher::SketchObject×9, PartDesign::Pad×8, PartDesign::CoordinateSystem×1, PartDesign::Pocket×1, PartDesign::Body×1
note: 29 computed .brp shape members not serialized (recipe doc carries the construction recipe); baked Part::Feature solids carry a one-line shape summary decoded from their .brp

FEATURE [Sketcher::SketchObject] Sketch
  FullyConstrained = true
  MapMode = 5
  Support = -> [XY_Plane]
  sketch-geometry (8):
    g0: LineSegment StartX=-30 StartY=12.5 StartZ=0 EndX=30 EndY=12.5 EndZ=0
    g1: LineSegment StartX=30 StartY=12.5 StartZ=0 EndX=30 EndY=-12.5 EndZ=0
    g2: LineSegment StartX=30 StartY=-12.5 StartZ=0 EndX=-30 EndY=-12.5 EndZ=0
    g3: LineSegment StartX=-30 StartY=-12.5 StartZ=0 EndX=-30 EndY=12.5 EndZ=0
    g4: Circle CenterX=-23 CenterY=6.5 CenterZ=0 NormalX=0 NormalY=0 NormalZ=1 AngleXU=0 Radius=3.3
    g5: Circle CenterX=-23 CenterY=-6.5 CenterZ=0 NormalX=0 NormalY=0 NormalZ=1 AngleXU=0 Radius=3.3
    g6: Circle CenterX=23 CenterY=-6.5 CenterZ=0 NormalX=0 NormalY=0 NormalZ=1 AngleXU=0 Radius=3.3
    g7: Circle CenterX=23 CenterY=6.5 CenterZ=0 NormalX=0 NormalY=0 NormalZ=1 AngleXU=0 Radius=3.3
  constraints (20):
    c: Coincident(g0,g1)
    c: Coincident(g1,g2)
    c: Coincident(g2,g3)
    c: Coincident(g3,g0)
    c: Horizontal(g0)
    c: Vertical(g1)
    c: DistanceX(g2,g2) = 60
    c: DistanceY(g3,g3) = 25
    c: Symmetric(g2,g0,g-1)
    c: Symmetric(g2,g1,g-2)
    c: Symmetric(g4,g7,g-2)
    c: Symmetric(g5,g6,g-2)
    c: DistanceX(g4,g7) = 46
    c: DistanceX(g5,g6) = 46
    c: Equal(g6,g7)
    c: Equal(g7,g4)
    c: Equal(g4,g5)
    c: Diameter(g7) = 6.6
    c: DistanceY(g7,g0) = 6
    c: DistanceY(g6,g7) = 13
FEATURE [PartDesign::Pad] Pad
  Direction = (1,1,1)
  Length = 36
  Length2 = 100
  Profile = -> Sketch
  Type = 0
FEATURE [PartDesign::CoordinateSystem] LCS_M1
  AttacherType = Attacher::AttachEngine3D
  MapMode = 11
  Placement = pos=(-23,6.5,36) rot=(0,0,1;1.5708rad)
  Support = -> [Pad]
FEATURE [Sketcher::SketchObject] Sketch001
  ExternalGeometry = -> [Pad]
  FullyConstrained = true
  MapMode = 5
  Placement = pos=(0,12.5,0) rot=(0,0.707107,0.707107;3.14159rad)
  Support = -> [Pad]
  sketch-geometry (4):
    g0: LineSegment StartX=-30 StartY=22.1 StartZ=0 EndX=30 EndY=22.1 EndZ=0
    g1: LineSegment StartX=30 StartY=22.1 StartZ=0 EndX=30 EndY=0 EndZ=0
    g2: LineSegment StartX=30 StartY=0 StartZ=0 EndX=-30 EndY=0 EndZ=0
    g3: LineSegment StartX=-30 StartY=0 StartZ=0 EndX=-30 EndY=22.1 EndZ=0
  constraints (10):
    c: Coincident(g0,g1)
    c: Coincident(g1,g2)
    c: Coincident(g2,g3)
    c: Coincident(g3,g0)
    c: Horizontal(g0)
    c: Vertical(g1)
    c: Vertical(g3)
    c: Coincident(g1,g-3)
    c: Coincident(g2,g-3)
    c: DistanceY(g3,g3) = 22.1
FEATURE [PartDesign::Pad] Pad001
  BaseFeature = -> Pad
  Direction = (1,1,1)
  Length = 127
  Length2 = 100
  Profile = -> Sketch001
  Type = 0
FEATURE [Sketcher::SketchObject] Sketch002
  ExternalGeometry = -> [Pad001]
  FullyConstrained = true
  MapMode = 5
  Placement = pos=(0,4.9e-15,22.1) rot=(0,0,1;0rad)
  Support = -> [Pad001]
  sketch-geometry (4):
    g0: Circle CenterX=-20 CenterY=124.5 CenterZ=0 NormalX=0 NormalY=0 NormalZ=1 AngleXU=0 Radius=2.5
    g1: Circle CenterX=20 CenterY=124.5 CenterZ=0 NormalX=0 NormalY=0 NormalZ=1 AngleXU=0 Radius=2.5
    g2: Circle CenterX=-20 CenterY=90.5 CenterZ=0 NormalX=0 NormalY=0 NormalZ=1 AngleXU=0 Radius=2.5
    g3: Circle CenterX=20 CenterY=90.5 CenterZ=0 NormalX=0 NormalY=0 NormalZ=1 AngleXU=0 Radius=2.5
  constraints (10):
    c: Equal(g1,g0)
    c: Equal(g0,g2)
    c: Equal(g2,g3)
    c: Diameter(g3) = 5
    c: Symmetric(g3,g2,g-2)
    c: Symmetric(g1,g0,g-2)
    c: DistanceX(g2,g3) = 40
    c: DistanceX(g0,g1) = 40
    c: DistanceY(g1,g-3) = 15
    c: DistanceY(g2,g0) = 34
FEATURE [PartDesign::Pocket] Pocket
  BaseFeature = -> Pad001
  Length = 5
  Length2 = 100
  Profile = -> Sketch002
  Type = 1
FEATURE [Sketcher::SketchObject] Sketch003
  ExternalGeometry = -> [Pocket]
  FullyConstrained = true
  MapMode = 5
  Placement = pos=(30,0,0) rot=(0.57735,0.57735,0.57735;2.0944rad)
  Support = -> [Pocket]
  sketch-geometry (3):
    g0: LineSegment StartX=12.5 StartY=36 StartZ=0 EndX=32.5 EndY=22.1 EndZ=0
    g1: LineSegment StartX=12.5 StartY=36 StartZ=0 EndX=12.5 EndY=0 EndZ=0
    g2: LineSegment StartX=12.5 StartY=0 StartZ=0 EndX=32.5 EndY=22.1 EndZ=0
  constraints (7):
    c: Coincident(g0,g-3)
    c: DistanceX(g-3,g0) = 20
    c: Coincident(g1,g0)
    c: Coincident(g1,g-4)
    c: Coincident(g2,g1)
    c: Coincident(g2,g0)
    c: PointOnObject(g0,g-5)
FEATURE [PartDesign::Pad] Pad002
  BaseFeature = -> Pocket
  Direction = (1,1,1)
  Length = 60
  Length2 = 100
  Profile = -> Sketch003
  Reversed = true
  Type = 0
FEATURE [Sketcher::SketchObject] Sketch004
  ExternalGeometry = -> [Pad002]
  FullyConstrained = true
  MapMode = 5
  Placement = pos=(30,0,0) rot=(0.57735,0.57735,0.57735;2.0944rad)
  Support = -> [Pad002]
  sketch-geometry (4):
    g0: LineSegment StartX=-12.5 StartY=-10 StartZ=0 EndX=139.5 EndY=-10 EndZ=0
    g1: LineSegment StartX=139.5 StartY=-10 StartZ=0 EndX=139.5 EndY=22.1 EndZ=0
    g2: LineSegment StartX=139.5 StartY=22.1 StartZ=0 EndX=-12.5 EndY=22.1 EndZ=0
    g3: LineSegment StartX=-12.5 StartY=22.1 StartZ=0 EndX=-12.5 EndY=-10 EndZ=0
  constraints (11):
    c: Coincident(g0,g1)
    c: Coincident(g1,g2)
    c: Coincident(g2,g3)
    c: Coincident(g3,g0)
    c: Horizontal(g2)
    c: Vertical(g1)
    c: Vertical(g3)
    c: DistanceY(g1,g1) = 32.1
    c: Coincident(g1,g-5)
    c: Horizontal(g0)
    c: PointOnObject(g-3,g3)
FEATURE [PartDesign::Pad] Pad003
  BaseFeature = -> Pad002
  Direction = (1,1,1)
  Length = 10
  Length2 = 100
  Profile = -> Sketch004
  Type = 0
FEATURE [Sketcher::SketchObject] Sketch005
  ExternalGeometry = -> [Pad003]
  FullyConstrained = true
  MapMode = 5
  Placement = pos=(-30,0,0) rot=(0.57735,-0.57735,-0.57735;2.0944rad)
  Support = -> [Pad003]
  sketch-geometry (4):
    g0: LineSegment StartX=-139.5 StartY=22.1 StartZ=0 EndX=12.5 EndY=22.1 EndZ=0
    g1: LineSegment StartX=12.5 StartY=22.1 StartZ=0 EndX=12.5 EndY=-10 EndZ=0
    g2: LineSegment StartX=12.5 StartY=-10 StartZ=0 EndX=-139.5 EndY=-10 EndZ=0
    g3: LineSegment StartX=-139.5 StartY=-10 StartZ=0 EndX=-139.5 EndY=22.1 EndZ=0
  constraints (11):
    c: Coincident(g0,g1)
    c: Coincident(g1,g2)
    c: Coincident(g2,g3)
    c: Coincident(g3,g0)
    c: Horizontal(g0)
    c: Horizontal(g2)
    c: Vertical(g1)
    c: Vertical(g3)
    c: Coincident(g0,g-3)
    c: PointOnObject(g-4,g1)
    c: DistanceY(g1,g1) = 32.1
FEATURE [PartDesign::Pad] Pad004
  BaseFeature = -> Pad003
  Direction = (1,1,1)
  Length = 10
  Length2 = 100
  Profile = -> Sketch005
  Type = 0
FEATURE [Sketcher::SketchObject] Sketch006
  ExternalGeometry = -> [Pad004]
  FullyConstrained = true
  MapMode = 5
  Placement = pos=(0,-12.5,0) rot=(1,0,0;1.5708rad)
  Support = -> [Pad004]
  sketch-geometry (6):
    g0: LineSegment StartX=40 StartY=22.1 StartZ=0 EndX=30 EndY=22.1 EndZ=0
    g1: LineSegment StartX=30 StartY=36 StartZ=0 EndX=40 EndY=22.1 EndZ=0
    g2: LineSegment StartX=30 StartY=36 StartZ=0 EndX=30 EndY=22.1 EndZ=0
    g3: LineSegment StartX=-30 StartY=36 StartZ=0 EndX=-30 EndY=22.1 EndZ=0
    g4: LineSegment StartX=-30 StartY=22.1 StartZ=0 EndX=-40 EndY=22.1 EndZ=0
    g5: LineSegment StartX=-40 StartY=22.1 StartZ=0 EndX=-30 EndY=36 EndZ=0
  constraints (12):
    c: Coincident(g0,g-6)
    c: Coincident(g0,g-6)
    c: Coincident(g1,g-5)
    c: Coincident(g1,g0)
    c: Coincident(g2,g1)
    c: Coincident(g2,g0)
    c: Coincident(g3,g-4)
    c: Coincident(g3,g-4)
    c: Coincident(g4,g3)
    c: Coincident(g4,g-3)
    c: Coincident(g5,g4)
    c: Coincident(g5,g3)
FEATURE [PartDesign::Pad] Pad005
  BaseFeature = -> Pad004
  Direction = (1,1,1)
  Length = 25
  Length2 = 100
  Profile = -> Sketch006
  Reversed = true
  Type = 0
FEATURE [Sketcher::SketchObject] Sketch007
  FullyConstrained = true
  MapMode = 5
  Placement = pos=(0,-12.5,0) rot=(1,0,0;1.5708rad)
  Support = -> [Pad005]
  sketch-geometry (4):
    g0: LineSegment StartX=-30 StartY=0 StartZ=0 EndX=30 EndY=0 EndZ=0
    g1: LineSegment StartX=30 StartY=0 StartZ=0 EndX=30 EndY=15 EndZ=0
    g2: LineSegment StartX=30 StartY=15 StartZ=0 EndX=-30 EndY=15 EndZ=0
    g3: LineSegment StartX=-30 StartY=15 StartZ=0 EndX=-30 EndY=0 EndZ=0
  constraints (11):
    c: Coincident(g0,g1)
    c: Coincident(g1,g2)
    c: Coincident(g2,g3)
    c: Coincident(g3,g0)
    c: Horizontal(g2)
    c: Vertical(g1)
    c: Vertical(g3)
    c: PointOnObject(g0,g-1)
    c: DistanceY(g1,g1) = 15
    c: DistanceX(g2,g2) = 60
    c: Symmetric(g0,g0,g-2)
FEATURE [PartDesign::Pad] Pad006
  BaseFeature = -> Pad005
  Direction = (1,1,1)
  Length = 12
  Length2 = 100
  Profile = -> Sketch007
  Type = 0
FEATURE [Sketcher::SketchObject] Sketch008
  ExternalGeometry = -> [Pad006]
  FullyConstrained = true
  MapMode = 5
  Placement = pos=(-30,0,0) rot=(0.57735,-0.57735,-0.57735;2.0944rad)
  Support = -> [Pad006]
  sketch-geometry (3):
    g0: LineSegment StartX=24.5 StartY=15 StartZ=0 EndX=12.5 EndY=15 EndZ=0
    g1: LineSegment StartX=12.5 StartY=15 StartZ=0 EndX=12.5 EndY=22.1 EndZ=0
    g2: LineSegment StartX=12.5 StartY=22.1 StartZ=0 EndX=24.5 EndY=15 EndZ=0
  constraints (6):
    c: Coincident(g0,g-3)
    c: Coincident(g0,g-3)
    c: Coincident(g1,g0)
    c: Coincident(g1,g-4)
    c: Coincident(g2,g0)
    c: Coincident(g1,g2)
FEATURE [PartDesign::Pad] Pad007
  BaseFeature = -> Pad006
  Direction = (1,1,1)
  Length = 60
  Length2 = 100
  Profile = -> Sketch008
  Reversed = true
  Type = 0
FEATURE [PartDesign::Body] Body
  Group = -> [Sketch,Pad,LCS_M1,Sketch001,Pad001,Sketch002,Pocket,Sketch003,Pad002,Sketch004,Pad003,Sketch005,Pad004,Sketch006,Pad005,Sketch007,Pad006,Sketch008,Pad007]
  Origin = -> Origin
  Tip = -> Pad007
---- part DSG16.FCStd = doc fcstd_b79a07b29058 ----
FCSTD DOCUMENT  (FreeCAD 0.19R)
Label: DSG16
License: All rights reserved
LicenseURL: http://en.wikipedia.org/wiki/All_rights_reserved
objects: PartDesign::CoordinateSystem×6, Sketcher::SketchObject×3, PartDesign::Pocket×2, PartDesign::Pad×1, PartDesign::Body×1
note: 16 computed .brp shape members not serialized (recipe doc carries the construction recipe); baked Part::Feature solids carry a one-line shape summary decoded from their .brp

FEATURE [Sketcher::SketchObject] Sketch
  FullyConstrained = true
  MapMode = 5
  Placement = pos=(0,0,0) rot=(1,0,0;1.5708rad)
  Support = -> [XZ_Plane]
  sketch-geometry (7):
    g0: LineSegment StartX=20 StartY=-26 StartZ=0 EndX=20 EndY=26 EndZ=0
    g1: LineSegment StartX=20 StartY=26 StartZ=0 EndX=-8 EndY=26 EndZ=0
    g2: LineSegment StartX=-8 StartY=26 StartZ=0 EndX=-20 EndY=14 EndZ=0
    g3: LineSegment StartX=-20 StartY=14 StartZ=0 EndX=-20 EndY=-14 EndZ=0
    g4: LineSegment StartX=-20 StartY=-14 StartZ=0 EndX=-8 EndY=-26 EndZ=0
    g5: LineSegment StartX=-8 StartY=-26 StartZ=0 EndX=20 EndY=-26 EndZ=0
    g6: Circle CenterX=0 CenterY=0 CenterZ=0 NormalX=0 NormalY=0 NormalZ=1 AngleXU=0 Radius=14
  constraints (19):
    c: Coincident(g1,g0)
    c: Horizontal(g1)
    c: Coincident(g2,g1)
    c: Coincident(g3,g2)
    c: Vertical(g3)
    c: Coincident(g4,g3)
    c: Coincident(g5,g4)
    c: Coincident(g5,g0)
    c: Horizontal(g5)
    c: Coincident(g6,g-1)
    c: Diameter(g6) = 28
    c: DistanceY(g0,g0) = 52
    c: DistanceX(g3,g0) = 40
    c: DistanceX(g3,g4) = 12
    c: DistanceY(g4,g3) = 12
    c: DistanceY(g2,g1) = 12
    c: DistanceX(g2,g1) = 12
    c: Symmetric(g0,g0,g-1)
    c: DistanceX(g-1,g0) = 20
FEATURE [PartDesign::Pad] Pad
  Direction = (1,1,1)
  Length = 40
  Length2 = 100
  Placement = pos=(0,0,0) rot=(1,0,0;1.5708rad)
  Profile = -> Sketch
  Reversed = true
  Type = 0
FEATURE [Sketcher::SketchObject] Sketch001
  FullyConstrained = true
  MapMode = 5
  Placement = pos=(0,0,0) rot=(1,0,0;1.5708rad)
  Support = -> [Pad]
  sketch-geometry (11):
    g0: Circle CenterX=0 CenterY=0 CenterZ=0 NormalX=0 NormalY=0 NormalZ=1 AngleXU=0 Radius=19
    g1: Circle CenterX=-13.435 CenterY=13.435 CenterZ=0 NormalX=0 NormalY=0 NormalZ=1 AngleXU=0 Radius=2.5
    g2: Circle CenterX=0 CenterY=19 CenterZ=0 NormalX=0 NormalY=0 NormalZ=1 AngleXU=0 Radius=2.5
    g3: Circle CenterX=0 CenterY=-19 CenterZ=0 NormalX=0 NormalY=0 NormalZ=1 AngleXU=0 Radius=2.5
    g4: Circle CenterX=13.435 CenterY=-13.435 CenterZ=0 NormalX=0 NormalY=0 NormalZ=1 AngleXU=0 Radius=2.5
    g5: Circle CenterX=-13.435 CenterY=-13.435 CenterZ=0 NormalX=0 NormalY=0 NormalZ=1 AngleXU=0 Radius=2.5
    g6: Circle CenterX=13.435 CenterY=13.435 CenterZ=0 NormalX=0 NormalY=0 NormalZ=1 AngleXU=0 Radius=2.5
    g7: LineSegment StartX=13.435 StartY=-13.435 StartZ=0 EndX=0 EndY=0 EndZ=0
    g8: LineSegment StartX=-13.435 StartY=-13.435 StartZ=0 EndX=0 EndY=0 EndZ=0
    g9: LineSegment StartX=0 StartY=0 StartZ=0 EndX=-13.435 EndY=13.435 EndZ=0
    g10: LineSegment StartX=0 StartY=0 StartZ=0 EndX=13.435 EndY=13.435 EndZ=0
  constraints (28):
    c: Coincident(g0,g-1)
    c: PointOnObject(g1,g0)
    c: PointOnObject(g2,g-2)
    c: PointOnObject(g3,g-2)
    c: PointOnObject(g4,g0)
    c: PointOnObject(g5,g0)
    c: PointOnObject(g6,g0)
    c: PointOnObject(g2,g0)
    c: PointOnObject(g3,g0)
    c: Equal(g4,g3)
    c: Equal(g3,g5)
    c: Equal(g5,g1)
    c: Equal(g1,g2)
    c: Equal(g2,g6)
    c: Diameter(g6) = 5
    c: Coincident(g7,g4)
    c: Coincident(g7,g-1)
    c: Coincident(g8,g5)
    c: Coincident(g8,g-1)
    c: Coincident(g9,g-1)
    c: Coincident(g9,g1)
    c: Coincident(g10,g-1)
    c: Coincident(g10,g6)
    c: Angle(g10,g9) = 1.5708
    c: Angle(g8,g7) = 1.5708
    c: Diameter(g0) = 38
    c: Angle(g7,g-1) = 0.785398
    c: Angle(g-1,g10) = 0.785398
FEATURE [PartDesign::Pocket] Pocket
  BaseFeature = -> Pad
  Length = 10
  Length2 = 100
  Placement = pos=(0,0,0) rot=(1,0,0;1.5708rad)
  Profile = -> Sketch001
  Type = 0
FEATURE [Sketcher::SketchObject] Sketch002
  FullyConstrained = true
  MapMode = 5
  Placement = pos=(20,0,0) rot=(0.707107,0,0.707107;3.14159rad)
  Support = -> [Pocket]
  sketch-geometry (4):
    g0: Circle CenterX=20 CenterY=-8 CenterZ=0 NormalX=0 NormalY=0 NormalZ=1 AngleXU=0 Radius=2.5
    g1: Circle CenterX=20 CenterY=-32 CenterZ=0 NormalX=0 NormalY=0 NormalZ=1 AngleXU=0 Radius=2.5
    g2: Circle CenterX=-20 CenterY=-8 CenterZ=0 NormalX=0 NormalY=0 NormalZ=1 AngleXU=0 Radius=2.5
    g3: Circle CenterX=-20 CenterY=-32 CenterZ=0 NormalX=0 NormalY=0 NormalZ=1 AngleXU=0 Radius=2.5
  constraints (10):
    c: Equal(g3,g2)
    c: Equal(g2,g1)
    c: Equal(g1,g0)
    c: Diameter(g1) = 5
    c: DistanceY(g3,g2) = 24
    c: Symmetric(g2,g0,g-2)
    c: Symmetric(g3,g1,g-2)
    c: DistanceX(g3,g1) = 40
    c: DistanceX(g2,g0) = 40
    c: DistanceY(g2,g-1) = 8
FEATURE [PartDesign::Pocket] Pocket001
  BaseFeature = -> Pocket
  Length = 10
  Length2 = 100
  Placement = pos=(0,0,0) rot=(1,0,0;1.5708rad)
  Profile = -> Sketch002
  Type = 0
FEATURE [PartDesign::CoordinateSystem] LCS_H1
  AttacherType = Attacher::AttachEngine3D
  MapMode = 11
  Placement = pos=(13.435,1.34e-14,13.435) rot=(0.57735,-0.57735,0.57735;2.0944rad)
  Support = -> [Pocket001]
FEATURE [PartDesign::CoordinateSystem] LCS_H2
  AttacherType = Attacher::AttachEngine3D
  MapMode = 11
  Placement = pos=(-13.435,1.34e-14,13.435) rot=(0.57735,-0.57735,0.57735;2.0944rad)
  Support = -> [Pocket001]
FEATURE [PartDesign::CoordinateSystem] LCS_H3
  AttacherType = Attacher::AttachEngine3D
  MapMode = 11
  Placement = pos=(13.435,-1.34e-14,-13.435) rot=(0.57735,-0.57735,0.57735;2.0944rad)
  Support = -> [Pocket001]
FEATURE [PartDesign::CoordinateSystem] LCS_H4
  AttacherType = Attacher::AttachEngine3D
  MapMode = 11
  Placement = pos=(-13.435,-1.34e-14,-13.435) rot=(0.57735,-0.57735,0.57735;2.0944rad)
  Support = -> [Pocket001]
FEATURE [PartDesign::CoordinateSystem] LCS_M1
  AttacherType = Attacher::AttachEngine3D
  MapMode = 11
  Placement = pos=(20,8,20) rot=(0.57735,-0.57735,0.57735;4.18879rad)
  Support = -> [Pocket001]
FEATURE [PartDesign::CoordinateSystem] LCS_M2
  AttacherType = Attacher::AttachEngine3D
  MapMode = 11
  Placement = pos=(20,8,-20) rot=(0.57735,-0.57735,0.57735;4.18879rad)
  Support = -> [Pocket001]
FEATURE [PartDesign::Body] Body
  Group = -> [Sketch,Pad,Sketch001,Pocket,Sketch002,Pocket001,LCS_H1,LCS_H2,LCS_H3,LCS_H4,LCS_M1,LCS_M2]
  Origin = -> Origin
  Tip = -> Pocket001
---- part LINMOD200.FCStd = doc fcstd_20a77ae43a17 ----
FCSTD DOCUMENT  (FreeCAD 0.19R)
Label: LINMOD200
License: All rights reserved
LicenseURL: http://en.wikipedia.org/wiki/All_rights_reserved
objects: Sketcher::SketchObject×8, PartDesign::Pad×5, PartDesign::Pocket×3, PartDesign::CoordinateSystem×3, PartDesign::Body×1
note: 28 computed .brp shape members not serialized (recipe doc carries the construction recipe); baked Part::Feature solids carry a one-line shape summary decoded from their .brp

FEATURE [Sketcher::SketchObject] Sketch
  FullyConstrained = true
  MapMode = 5
  Placement = pos=(0,0,0) rot=(1,0,0;1.5708rad)
  Support = -> [XZ_Plane]
  sketch-geometry (4):
    g0: LineSegment StartX=-50 StartY=10 StartZ=0 EndX=50 EndY=10 EndZ=0
    g1: LineSegment StartX=50 StartY=10 StartZ=0 EndX=50 EndY=-10 EndZ=0
    g2: LineSegment StartX=50 StartY=-10 StartZ=0 EndX=-50 EndY=-10 EndZ=0
    g3: LineSegment StartX=-50 StartY=-10 StartZ=0 EndX=-50 EndY=10 EndZ=0
  constraints (10):
    c: Coincident(g0,g1)
    c: Coincident(g1,g2)
    c: Coincident(g2,g3)
    c: Coincident(g3,g0)
    c: Horizontal(g2)
    c: Vertical(g1)
    c: DistanceY(g2,g0) = 20
    c: DistanceX(g0,g0) = 100
    c: Symmetric(g2,g0,g-1)
    c: Symmetric(g0,g0,g-2)
FEATURE [PartDesign::Pad] Pad
  Direction = (1,1,1)
  Length = 370
  Length2 = 100
  Placement = pos=(0,0,0) rot=(1,0,0;1.5708rad)
  Profile = -> Sketch
  Type = 0
FEATURE [Sketcher::SketchObject] Sketch001
  ExternalGeometry = -> [Pad]
  FullyConstrained = true
  MapMode = 5
  Placement = pos=(0,-370,8.14e-14) rot=(1,0,0;1.5708rad)
  Support = -> [Pad]
  sketch-geometry (4):
    g0: LineSegment StartX=-50 StartY=60 StartZ=0 EndX=50 EndY=60 EndZ=0
    g1: LineSegment StartX=50 StartY=60 StartZ=0 EndX=50 EndY=-10 EndZ=0
    g2: LineSegment StartX=50 StartY=-10 StartZ=0 EndX=-50 EndY=-10 EndZ=0
    g3: LineSegment StartX=-50 StartY=-10 StartZ=0 EndX=-50 EndY=60 EndZ=0
  constraints (10):
    c: Coincident(g0,g1)
    c: Coincident(g1,g2)
    c: Coincident(g2,g3)
    c: Coincident(g3,g0)
    c: Horizontal(g0)
    c: Vertical(g1)
    c: Vertical(g3)
    c: Coincident(g1,g-3)
    c: Coincident(g-3,g2)
    c: DistanceY(g1,g1) = 70
FEATURE [PartDesign::Pad] Pad001
  BaseFeature = -> Pad
  Direction = (1,1,1)
  Length = 10
  Length2 = 100
  Placement = pos=(0,0,0) rot=(1,0,0;1.5708rad)
  Profile = -> Sketch001
  Type = 0
FEATURE [Sketcher::SketchObject] Sketch002
  ExternalGeometry = -> [Pad001]
  FullyConstrained = true
  MapMode = 5
  Placement = pos=(0,-380,3.078e-13) rot=(1,0,0;1.5708rad)
  Support = -> [Pad001]
  sketch-geometry (4):
    g0: LineSegment StartX=-28.5 StartY=57 StartZ=0 EndX=28.5 EndY=57 EndZ=0
    g1: LineSegment StartX=28.5 StartY=57 StartZ=0 EndX=28.5 EndY=0 EndZ=0
    g2: LineSegment StartX=28.5 StartY=0 StartZ=0 EndX=-28.5 EndY=0 EndZ=0
    g3: LineSegment StartX=-28.5 StartY=0 StartZ=0 EndX=-28.5 EndY=57 EndZ=0
  constraints (11):
    c: Coincident(g0,g1)
    c: Coincident(g1,g2)
    c: Coincident(g2,g3)
    c: Coincident(g3,g0)
    c: Horizontal(g0)
    c: Vertical(g1)
    c: Vertical(g3)
    c: DistanceY(g1,g1) = 57
    c: DistanceX(g0,g0) = 57
    c: Symmetric(g1,g2,g-2)
    c: PointOnObject(g1,g-1)
FEATURE [PartDesign::Pad] Pad002
  BaseFeature = -> Pad001
  Direction = (1,1,1)
  Length = 56
  Length2 = 100
  Placement = pos=(0,0,0) rot=(1,0,0;1.5708rad)
  Profile = -> Sketch002
  Type = 0
FEATURE [Sketcher::SketchObject] Sketch003
  ExternalGeometry = -> [Pad002]
  FullyConstrained = true
  MapMode = 5
  Placement = pos=(0,4.4e-15,10) rot=(0,0,1;3.14159rad)
  Support = -> [Pad002]
  sketch-geometry (8):
    g0: LineSegment StartX=-37.5 StartY=330 StartZ=0 EndX=-22.5 EndY=330 EndZ=0
    g1: LineSegment StartX=-22.5 StartY=330 StartZ=0 EndX=-22.5 EndY=20 EndZ=0
    g2: LineSegment StartX=-22.5 StartY=20 StartZ=0 EndX=-37.5 EndY=20 EndZ=0
    g3: LineSegment StartX=-37.5 StartY=20 StartZ=0 EndX=-37.5 EndY=330 EndZ=0
    g4: LineSegment StartX=22.5 StartY=330 StartZ=0 EndX=37.5 EndY=330 EndZ=0
    g5: LineSegment StartX=37.5 StartY=330 StartZ=0 EndX=37.5 EndY=20 EndZ=0
    g6: LineSegment StartX=37.5 StartY=20 StartZ=0 EndX=22.5 EndY=20 EndZ=0
    g7: LineSegment StartX=22.5 StartY=20 StartZ=0 EndX=22.5 EndY=330 EndZ=0
  constraints (23):
    c: Coincident(g0,g1)
    c: Coincident(g1,g2)
    c: Coincident(g2,g3)
    c: Coincident(g3,g0)
    c: Horizontal(g0)
    c: Horizontal(g2)
    c: Vertical(g1)
    c: Vertical(g3)
    c: Coincident(g4,g5)
    c: Coincident(g5,g6)
    c: Coincident(g6,g7)
    c: Coincident(g7,g4)
    c: Horizontal(g4)
    c: Horizontal(g6)
    c: Vertical(g5)
    c: Vertical(g7)
    c: Symmetric(g6,g1,g-2)
    c: DistanceX(g2,g2) = 15
    c: DistanceX(g6,g6) = 15
    c: DistanceY(g-1,g1) = 20
    c: DistanceY(g0,g-3) = 40
    c: DistanceY(g4,g-3) = 40
    c: DistanceX(g1,g6) = 45
FEATURE [PartDesign::Pad] Pad003
  BaseFeature = -> Pad002
  Direction = (1,1,1)
  Length = 15
  Length2 = 100
  Placement = pos=(0,0,0) rot=(1,0,0;1.5708rad)
  Profile = -> Sketch003
  Type = 0
FEATURE [Sketcher::SketchObject] Sketch004
  ExternalGeometry = -> [Pad003]
  FullyConstrained = true
  MapMode = 5
  Placement = pos=(0,-370,2.997e-13) rot=(-1,0,0;1.5708rad)
  Support = -> [Pad003]
  sketch-geometry (1):
    g0: Circle CenterX=0 CenterY=-28.5 CenterZ=0 NormalX=0 NormalY=0 NormalZ=1 AngleXU=0 Radius=6
  constraints (3):
    c: PointOnObject(g0,g-2)
    c: Diameter(g0) = 12
    c: DistanceY(g-3,g0) = 28.5
FEATURE [PartDesign::Pad] Pad004
  BaseFeature = -> Pad003
  Direction = (1,1,1)
  Length = 370
  Length2 = 100
  Placement = pos=(0,0,0) rot=(1,0,0;1.5708rad)
  Profile = -> Sketch004
  Type = 0
FEATURE [Sketcher::SketchObject] Sketch005
  FullyConstrained = true
  MapMode = 5
  Placement = pos=(0,-4.4e-15,-10) rot=(1,0,0;3.14159rad)
  Support = -> [Pad004]
  sketch-geometry (8):
    g0: Circle CenterX=-25 CenterY=10 CenterZ=0 NormalX=0 NormalY=0 NormalZ=1 AngleXU=0 Radius=4
    g1: Circle CenterX=25 CenterY=10 CenterZ=0 NormalX=0 NormalY=0 NormalZ=1 AngleXU=0 Radius=4
    g2: Circle CenterX=25 CenterY=35 CenterZ=0 NormalX=0 NormalY=0 NormalZ=1 AngleXU=0 Radius=4
    g3: Circle CenterX=-25 CenterY=35 CenterZ=0 NormalX=0 NormalY=0 NormalZ=1 AngleXU=0 Radius=4
    g4: Circle CenterX=-25 CenterY=93 CenterZ=0 NormalX=0 NormalY=0 NormalZ=1 AngleXU=0 Radius=4
    g5: Circle CenterX=-25 CenterY=68 CenterZ=0 NormalX=0 NormalY=0 NormalZ=1 AngleXU=0 Radius=4
    g6: Circle CenterX=25 CenterY=93 CenterZ=0 NormalX=0 NormalY=0 NormalZ=1 AngleXU=0 Radius=4
    g7: Circle CenterX=25 CenterY=68 CenterZ=0 NormalX=0 NormalY=0 NormalZ=1 AngleXU=0 Radius=4
  constraints (20):
    c: Equal(g1,g2)
    c: Equal(g2,g7)
    c: Equal(g7,g6)
    c: Equal(g6,g4)
    c: Equal(g4,g5)
    c: Equal(g5,g3)
    c: Equal(g3,g0)
    c: Diameter(g6) = 8
    c: Symmetric(g4,g6,g-2)
    c: Symmetric(g5,g7,g-2)
    c: Symmetric(g3,g2,g-2)
    c: Symmetric(g0,g1,g-2)
    c: DistanceX(g4,g6) = 50
    c: DistanceX(g5,g7) = 50
    c: DistanceX(g3,g2) = 50
    c: DistanceX(g0,g1) = 50
    c: DistanceY(g5,g4) = 25
    c: DistanceY(g0,g3) = 25
    c: DistanceY(g3,g5) = 33
    c: DistanceY(g-1,g0) = 10
FEATURE [PartDesign::Pocket] Pocket
  BaseFeature = -> Pad004
  Length = 15
  Length2 = 100
  Placement = pos=(0,0,0) rot=(1,0,0;1.5708rad)
  Profile = -> Sketch005
  Type = 0
FEATURE [PartDesign::CoordinateSystem] LCS_m1
  AttacherType = Attacher::AttachEngine3D
  MapMode = 11
  Placement = pos=(25,-10,-10) rot=(0.707107,-0.707107,0;3.14159rad)
  Support = -> [Pocket]
FEATURE [PartDesign::CoordinateSystem] LCS_m2
  AttacherType = Attacher::AttachEngine3D
  MapMode = 11
  Placement = pos=(-25,-10,-10) rot=(0.707107,-0.707107,0;3.14159rad)
  Support = -> [Pocket]
FEATURE [PartDesign::CoordinateSystem] LCS_caret_mount
  AttacherType = Attacher::AttachEngine3D
  AttachmentOffset = pos=(-30,30,0) rot=(0,0,1;0rad)
  MapMode = 5
  Placement = pos=(30,-30,25) rot=(0,0,1;3.14159rad)
  Support = -> [Pocket]
FEATURE [Sketcher::SketchObject] Sketch006
  ExternalGeometry = -> [Pocket]
  FullyConstrained = true
  MapMode = 5
  Placement = pos=(0,-436,4.36e-13) rot=(1,0,0;1.5708rad)
  Support = -> [Pocket]
  sketch-geometry (12):
    g0: ArcOfCircle CenterX=-28.5 CenterY=57 CenterZ=0 NormalX=0 NormalY=0 NormalZ=1 AngleXU=0 Radius=9 StartAngle=4.71239 EndAngle=6.28319
    g1: ArcOfCircle CenterX=28.5 CenterY=57 CenterZ=0 NormalX=0 NormalY=0 NormalZ=1 AngleXU=0 Radius=9 StartAngle=3.14159 EndAngle=4.71239
    g2: ArcOfCircle CenterX=28.5 CenterY=1.279e-13 CenterZ=0 NormalX=0 NormalY=0 NormalZ=1 AngleXU=0 Radius=9 StartAngle=1.5708 EndAngle=3.14159
    g3: ArcOfCircle CenterX=-28.5 CenterY=1.315e-13 CenterZ=0 NormalX=0 NormalY=0 NormalZ=1 AngleXU=0 Radius=9 StartAngle=-1.42e-14 EndAngle=1.5708
    g4: LineSegment StartX=-19.5 StartY=3.1e-15 StartZ=0 EndX=-28.5 EndY=1.315e-13 EndZ=0
    g5: LineSegment StartX=-28.5 StartY=9 StartZ=0 EndX=-28.5 EndY=1.315e-13 EndZ=0
    g6: LineSegment StartX=28.5 StartY=1.279e-13 StartZ=0 EndX=19.5 EndY=-2.9e-15 EndZ=0
    g7: LineSegment StartX=28.5 StartY=1.279e-13 StartZ=0 EndX=28.5 EndY=9 EndZ=0
    g8: LineSegment StartX=-19.5 StartY=57 StartZ=0 EndX=-28.5 EndY=57 EndZ=0
    g9: LineSegment StartX=-28.5 StartY=57 StartZ=0 EndX=-28.5 EndY=48 EndZ=0
    g10: LineSegment StartX=28.5 StartY=48 StartZ=0 EndX=28.5 EndY=57 EndZ=0
    g11: LineSegment StartX=28.5 StartY=57 StartZ=0 EndX=19.5 EndY=57 EndZ=0
  constraints (32):
    c: Coincident(g0,g-5)
    c: PointOnObject(g0,g-3)
    c: PointOnObject(g0,g-5)
    c: Coincident(g1,g-5)
    c: PointOnObject(g1,g-5)
    c: PointOnObject(g1,g-4)
    c: Coincident(g2,g-4)
    c: PointOnObject(g2,g-4)
    c: PointOnObject(g2,g-1)
    c: Coincident(g3,g-3)
    c: PointOnObject(g3,g-1)
    c: PointOnObject(g3,g-3)
    c: Coincident(g4,g3)
    c: Coincident(g4,g3)
    c: Coincident(g5,g3)
    c: Coincident(g5,g3)
    c: Coincident(g6,g2)
    c: Coincident(g7,g2)
    c: Coincident(g7,g2)
    c: Coincident(g6,g2)
    c: Coincident(g8,g0)
    c: Coincident(g8,g0)
    c: Coincident(g9,g0)
    c: Coincident(g9,g0)
    c: Coincident(g10,g1)
    c: Coincident(g10,g1)
    c: Coincident(g11,g1)
    c: Coincident(g11,g1)
    c: Equal(g0,g3)
    c: Equal(g3,g2)
    c: Equal(g2,g1)
    c: Radius(g1) = 9
FEATURE [PartDesign::Pocket] Pocket001
  BaseFeature = -> Pocket
  Length = 50
  Length2 = 100
  Placement = pos=(0,0,0) rot=(1,0,0;1.5708rad)
  Profile = -> Sketch006
  Type = 0
FEATURE [Sketcher::SketchObject] Sketch007
  ExternalGeometry = -> [Pocket001]
  FullyConstrained = true
  MapMode = 5
  Placement = pos=(0,-20,6.6e-15) rot=(-1,0,0;1.5708rad)
  Support = -> [Pocket001]
  sketch-geometry (29):
    g0: LineSegment StartX=-37.5 StartY=-22.5 StartZ=0 EndX=-35 EndY=-25 EndZ=0
    g1: LineSegment StartX=-37.5 StartY=-25 StartZ=0 EndX=-35 EndY=-25 EndZ=0
    g2: LineSegment StartX=-37.5 StartY=-19.7 StartZ=0 EndX=-35 EndY=-17.2 EndZ=0
    g3: LineSegment StartX=-35 StartY=-17.2 StartZ=0 EndX=-35 EndY=-15.2 EndZ=0
    g4: LineSegment StartX=-35 StartY=-15.2 StartZ=0 EndX=-37.5 EndY=-12.7 EndZ=0
    g5: LineSegment StartX=-37.5 StartY=-12.7 StartZ=0 EndX=-37.5 EndY=-19.7 EndZ=0
    g6: LineSegment StartX=-37.5 StartY=-22.5 StartZ=0 EndX=-37.5 EndY=-25 EndZ=0
    g7: LineSegment StartX=22.5 StartY=-22.5 StartZ=0 EndX=25 EndY=-25 EndZ=0
    g8: LineSegment StartX=22.5 StartY=-25 StartZ=0 EndX=25 EndY=-25 EndZ=0
    g9: LineSegment StartX=22.5 StartY=-19.7 StartZ=0 EndX=25 EndY=-17.2 EndZ=0
    g10: LineSegment StartX=25 StartY=-17.2 StartZ=0 EndX=25 EndY=-15.2 EndZ=0
    g11: LineSegment StartX=25 StartY=-15.2 StartZ=0 EndX=22.5 EndY=-12.7 EndZ=0
    g12: LineSegment StartX=22.5 StartY=-12.7 StartZ=0 EndX=22.5 EndY=-19.7 EndZ=0
    g13: LineSegment StartX=22.5 StartY=-22.5 StartZ=0 EndX=22.5 EndY=-25 EndZ=0
    g14: LineSegment StartX=-30 StartY=-25 StartZ=0 EndX=-30 EndY=-10 EndZ=0
    g15: LineSegment StartX=-22.5 StartY=-22.5 StartZ=0 EndX=-25 EndY=-25 EndZ=0
    g16: LineSegment StartX=-22.5 StartY=-25 StartZ=0 EndX=-25 EndY=-25 EndZ=0
    g17: LineSegment StartX=-22.5 StartY=-19.7 StartZ=0 EndX=-25 EndY=-17.2 EndZ=0
    g18: LineSegment StartX=-25 StartY=-17.2 StartZ=0 EndX=-25 EndY=-15.2 EndZ=0
    g19: LineSegment StartX=-25 StartY=-15.2 StartZ=0 EndX=-22.5 EndY=-12.7 EndZ=0
    g20: LineSegment StartX=-22.5 StartY=-12.7 StartZ=0 EndX=-22.5 EndY=-19.7 EndZ=0
    g21: LineSegment StartX=-22.5 StartY=-22.5 StartZ=0 EndX=-22.5 EndY=-25 EndZ=0
    g22: LineSegment StartX=37.5 StartY=-22.5 StartZ=0 EndX=35 EndY=-25 EndZ=0
    g23: LineSegment StartX=37.5 StartY=-25 StartZ=0 EndX=35 EndY=-25 EndZ=0
    g24: LineSegment StartX=37.5 StartY=-19.7 StartZ=0 EndX=35 EndY=-17.2 EndZ=0
    g25: LineSegment StartX=35 StartY=-17.2 StartZ=0 EndX=35 EndY=-15.2 EndZ=0
    g26: LineSegment StartX=35 StartY=-15.2 StartZ=0 EndX=37.5 EndY=-12.7 EndZ=0
    g27: LineSegment StartX=37.5 StartY=-12.7 StartZ=0 EndX=37.5 EndY=-19.7 EndZ=0
    g28: LineSegment StartX=37.5 StartY=-22.5 StartZ=0 EndX=37.5 EndY=-25 EndZ=0
  constraints (84):
    c: PointOnObject(g0,g-3)
    c: Coincident(g1,g-3)
    c: Coincident(g1,g0)
    c: Horizontal(g1)
    c: PointOnObject(g2,g-3)
    c: Coincident(g3,g2)
    c: Vertical(g3)
    c: Coincident(g4,g3)
    c: PointOnObject(g4,g-3)
    c: Coincident(g5,g4)
    c: Coincident(g5,g2)
    c: Coincident(g6,g0)
    c: Coincident(g6,g1)
    c: DistanceX(g1,g1) = 2.5
    c: DistanceY(g6,g6) = 2.5
    c: DistanceX(g2,g2) = 2.5
    c: DistanceY(g5,g5) = 7
    c: DistanceY(g2,g2) = 2.5
    c: DistanceY(g3,g3) = 2
    c: DistanceY(g0,g2) = 2.8
    c: Coincident(g8,g7)
    c: Horizontal(g8)
    c: Coincident(g10,g9)
    c: Vertical(g10)
    c: Coincident(g11,g10)
    c: Coincident(g12,g11)
    c: Coincident(g12,g9)
    c: Coincident(g13,g7)
    c: Coincident(g13,g8)
    c: DistanceX(g8,g8) = 2.5
    c: DistanceY(g13,g13) = 2.5
    c: DistanceX(g9,g9) = 2.5
    c: DistanceY(g12,g12) = 7
    c: DistanceY(g9,g9) = 2.5
    c: DistanceY(g10,g10) = 2
    c: DistanceY(g7,g9) = 2.8
    c: Coincident(g13,g-5)
    c: PointOnObject(g7,g-5)
    c: PointOnObject(g9,g-5)
    c: PointOnObject(g11,g-5)
    c: PointOnObject(g14,g-7)
    c: PointOnObject(g14,g-8)
    c: Symmetric(g1,g-7,g14)
    c: Coincident(g16,g15)
    c: Coincident(g18,g17)
    c: Coincident(g19,g18)
    c: Coincident(g20,g19)
    c: Coincident(g20,g17)
    c: Coincident(g21,g15)
    c: Coincident(g21,g16)
    c: DistanceX(g16,g16) = 2.5
    c: DistanceX(g21,g21) = 0
    c: PointOnObject(g15,g-4)
    c: PointOnObject(g15,g-7)
    c: Horizontal(g16)
    c: DistanceY(g21,g21) = 2.5
    c: DistanceY(g20,g20) = 7
    c: DistanceY(g18,g18) = 2
    c: DistanceX(g17,g17) = 2.5
    c: DistanceX(g19,g19) = 2.5
    c: DistanceY(g17,g17) = 2.5
    c: PointOnObject(g19,g-4)
    c: Vertical(g20)
    c: DistanceY(g15,g17) = 2.8
    c: Coincident(g23,g22)
    c: Coincident(g25,g24)
    c: Coincident(g26,g25)
    c: Coincident(g27,g26)
    c: Coincident(g27,g24)
    c: Coincident(g28,g22)
    c: Coincident(g28,g23)
    c: DistanceX(g23,g23) = 2.5
    c: DistanceX(g28,g28) = 0
    c: Horizontal(g23)
    c: DistanceY(g28,g28) = 2.5
    c: DistanceY(g27,g27) = 7
    c: DistanceY(g25,g25) = 2
    c: DistanceX(g24,g24) = 2.5
    c: DistanceX(g26,g26) = 2.5
    c: DistanceY(g24,g24) = 2.5
    c: Vertical(g27)
    c: DistanceY(g22,g24) = 2.8
    c: Coincident(g23,g-6)
    c: PointOnObject(g24,g-6)
FEATURE [PartDesign::Pocket] Pocket002
  BaseFeature = -> Pocket001
  Length = 310
  Length2 = 100
  Placement = pos=(0,0,0) rot=(1,0,0;1.5708rad)
  Profile = -> Sketch007
  Type = 0
FEATURE [PartDesign::Body] Body
  Group = -> [Sketch,Pad,Sketch001,Pad001,Sketch002,Pad002,Sketch003,Pad003,Sketch004,Pad004,Sketch005,Pocket,LCS_m1,LCS_m2,LCS_caret_mount,Sketch006,Pocket001,Sketch007,Pocket002]
  Origin = -> Origin
  Tip = -> Pocket002
---- part LINMOD_CARET.FCStd = doc fcstd_8017de0ba3a2 ----
FCSTD DOCUMENT  (FreeCAD 0.19R)
Label: LINMOD_CARET
License: All rights reserved
LicenseURL: http://en.wikipedia.org/wiki/All_rights_reserved
objects: PartDesign::CoordinateSystem×5, Sketcher::SketchObject×3, PartDesign::Pad×3, PartDesign::Body×1
note: 15 computed .brp shape members not serialized (recipe doc carries the construction recipe); baked Part::Feature solids carry a one-line shape summary decoded from their .brp

FEATURE [Sketcher::SketchObject] Sketch
  FullyConstrained = true
  MapMode = 5
  Support = -> [XY_Plane]
  sketch-geometry (12):
    g0: LineSegment StartX=-60 StartY=50 StartZ=0 EndX=60 EndY=50 EndZ=0
    g1: LineSegment StartX=60 StartY=50 StartZ=0 EndX=60 EndY=-50 EndZ=0
    g2: LineSegment StartX=60 StartY=-50 StartZ=0 EndX=-60 EndY=-50 EndZ=0
    g3: LineSegment StartX=-60 StartY=-50 StartZ=0 EndX=-60 EndY=50 EndZ=0
    g4: Circle CenterX=-50 CenterY=40 CenterZ=0 NormalX=0 NormalY=0 NormalZ=1 AngleXU=0 Radius=2.5
    g5: Circle CenterX=-30 CenterY=40 CenterZ=0 NormalX=0 NormalY=0 NormalZ=1 AngleXU=0 Radius=2.5
    g6: Circle CenterX=30 CenterY=40 CenterZ=0 NormalX=0 NormalY=0 NormalZ=1 AngleXU=0 Radius=2.5
    g7: Circle CenterX=50 CenterY=40 CenterZ=0 NormalX=0 NormalY=0 NormalZ=1 AngleXU=0 Radius=2.5
    g8: Circle CenterX=-50 CenterY=-40 CenterZ=0 NormalX=0 NormalY=0 NormalZ=1 AngleXU=0 Radius=2.5
    g9: Circle CenterX=-30 CenterY=-40 CenterZ=0 NormalX=0 NormalY=0 NormalZ=1 AngleXU=0 Radius=2.5
    g10: Circle CenterX=30 CenterY=-40 CenterZ=0 NormalX=0 NormalY=0 NormalZ=1 AngleXU=0 Radius=2.5
    g11: Circle CenterX=50 CenterY=-40 CenterZ=0 NormalX=0 NormalY=0 NormalZ=1 AngleXU=0 Radius=2.5
  constraints (28):
    c: Coincident(g0,g1)
    c: Coincident(g1,g2)
    c: Coincident(g2,g3)
    c: Coincident(g3,g0)
    c: Horizontal(g0)
    c: Vertical(g1)
    c: DistanceX(g0,g0) = 120
    c: DistanceY(g1,g1) = 100
    c: Symmetric(g2,g1,g-2)
    c: Symmetric(g2,g0,g-1)
    c: Equal(g11,g10)
    c: Equal(g10,g9)
    c: Equal(g9,g8)
    c: Equal(g8,g5)
    c: Equal(g5,g4)
    c: Equal(g4,g6)
    c: Equal(g6,g7)
    c: Diameter(g7) = 5
    c: Symmetric(g5,g6,g-2)
    c: Symmetric(g7,g4,g-2)
    c: Symmetric(g9,g10,g-2)
    c: Symmetric(g11,g8,g-2)
    c: Symmetric(g10,g6,g-1)
    c: Symmetric(g11,g7,g-1)
    c: DistanceY(g11,g7) = 80
    c: DistanceY(g10,g6) = 80
    c: DistanceX(g5,g6) = 60
    c: DistanceX(g8,g11) = 100
FEATURE [PartDesign::Pad] Pad
  Direction = (1,1,1)
  Length = 10
  Length2 = 100
  Profile = -> Sketch
  Type = 0
FEATURE [Sketcher::SketchObject] Sketch001
  FullyConstrained = true
  MapMode = 5
  Placement = pos=(0,0,0) rot=(1,0,0;3.14159rad)
  Support = -> [Pad]
  sketch-geometry (8):
    g0: LineSegment StartX=-47.5 StartY=25 StartZ=0 EndX=-12.5 EndY=25 EndZ=0
    g1: LineSegment StartX=-12.5 StartY=25 StartZ=0 EndX=-12.5 EndY=-25 EndZ=0
    g2: LineSegment StartX=-12.5 StartY=-25 StartZ=0 EndX=-47.5 EndY=-25 EndZ=0
    g3: LineSegment StartX=-47.5 StartY=-25 StartZ=0 EndX=-47.5 EndY=25 EndZ=0
    g4: LineSegment StartX=12.5 StartY=25 StartZ=0 EndX=47.5 EndY=25 EndZ=0
    g5: LineSegment StartX=47.5 StartY=25 StartZ=0 EndX=47.5 EndY=-25 EndZ=0
    g6: LineSegment StartX=47.5 StartY=-25 StartZ=0 EndX=12.5 EndY=-25 EndZ=0
    g7: LineSegment StartX=12.5 StartY=-25 StartZ=0 EndX=12.5 EndY=25 EndZ=0
  constraints (21):
    c: Coincident(g0,g1)
    c: Coincident(g1,g2)
    c: Coincident(g2,g3)
    c: Coincident(g3,g0)
    c: Horizontal(g0)
    c: Horizontal(g2)
    c: Vertical(g1)
    c: Vertical(g3)
    c: Coincident(g4,g5)
    c: Coincident(g5,g6)
    c: Coincident(g6,g7)
    c: Coincident(g7,g4)
    c: Horizontal(g6)
    c: Vertical(g5)
    c: Symmetric(g0,g4,g-2)
    c: Symmetric(g4,g0,g-2)
    c: Equal(g7,g1)
    c: DistanceX(g4,g4) = 35
    c: Symmetric(g6,g4,g-1)
    c: DistanceY(g5,g5) = 50
    c: DistanceX(g2,g5) = 95
FEATURE [PartDesign::Pad] Pad001
  BaseFeature = -> Pad
  Direction = (1,1,1)
  Length = 18
  Length2 = 100
  Profile = -> Sketch001
  Type = 0
FEATURE [Sketcher::SketchObject] Sketch002
  ExternalGeometry = -> [Pad001]
  FullyConstrained = true
  MapMode = 5
  Placement = pos=(0,0,-18) rot=(1,0,0;3.14159rad)
  Support = -> [Pad001]
  sketch-geometry (16):
    g0: LineSegment StartX=-47.5 StartY=25 StartZ=0 EndX=-37.5 EndY=25 EndZ=0
    g1: LineSegment StartX=-37.5 StartY=25 StartZ=0 EndX=-37.5 EndY=-25 EndZ=0
    g2: LineSegment StartX=-37.5 StartY=-25 StartZ=0 EndX=-47.5 EndY=-25 EndZ=0
    g3: LineSegment StartX=-47.5 StartY=-25 StartZ=0 EndX=-47.5 EndY=25 EndZ=0
    g4: LineSegment StartX=-22.5 StartY=25 StartZ=0 EndX=-12.5 EndY=25 EndZ=0
    g5: LineSegment StartX=-12.5 StartY=25 StartZ=0 EndX=-12.5 EndY=-25 EndZ=0
    g6: LineSegment StartX=-12.5 StartY=-25 StartZ=0 EndX=-22.5 EndY=-25 EndZ=0
    g7: LineSegment StartX=-22.5 StartY=-25 StartZ=0 EndX=-22.5 EndY=25 EndZ=0
    g8: LineSegment StartX=12.5 StartY=25 StartZ=0 EndX=22.5 EndY=25 EndZ=0
    g9: LineSegment StartX=22.5 StartY=25 StartZ=0 EndX=22.5 EndY=-25 EndZ=0
    g10: LineSegment StartX=22.5 StartY=-25 StartZ=0 EndX=12.5 EndY=-25 EndZ=0
    g11: LineSegment StartX=12.5 StartY=-25 StartZ=0 EndX=12.5 EndY=25 EndZ=0
    g12: LineSegment StartX=37.5 StartY=25 StartZ=0 EndX=47.5 EndY=25 EndZ=0
    g13: LineSegment StartX=47.5 StartY=25 StartZ=0 EndX=47.5 EndY=-25 EndZ=0
    g14: LineSegment StartX=47.5 StartY=-25 StartZ=0 EndX=37.5 EndY=-25 EndZ=0
    g15: LineSegment StartX=37.5 StartY=-25 StartZ=0 EndX=37.5 EndY=25 EndZ=0
  constraints (40):
    c: Coincident(g0,g1)
    c: Coincident(g1,g2)
    c: Coincident(g2,g3)
    c: Coincident(g3,g0)
    c: Horizontal(g0)
    c: Horizontal(g2)
    c: Vertical(g1)
    c: Coincident(g4,g5)
    c: Coincident(g5,g6)
    c: Coincident(g6,g7)
    c: Coincident(g7,g4)
    c: Horizontal(g4)
    c: Horizontal(g6)
    c: Vertical(g7)
    c: Coincident(g8,g9)
    c: Coincident(g9,g10)
    c: Coincident(g10,g11)
    c: Coincident(g11,g8)
    c: Horizontal(g8)
    c: Horizontal(g10)
    c: Vertical(g9)
    c: Coincident(g12,g13)
    c: Coincident(g13,g14)
    c: Coincident(g14,g15)
    c: Coincident(g15,g12)
    c: Horizontal(g12)
    c: Horizontal(g14)
    c: Vertical(g15)
    c: Coincident(g12,g-4)
    c: Coincident(g13,g-4)
    c: Coincident(g8,g-5)
    c: Coincident(g10,g-5)
    c: Equal(g8,g12)
    c: Equal(g12,g4)
    c: Equal(g4,g0)
    c: DistanceX(g8,g8) = 10
    c: Coincident(g4,g-6)
    c: Coincident(g5,g-6)
    c: Coincident(g0,g-3)
    c: Coincident(g2,g-3)
FEATURE [PartDesign::Pad] Pad002
  BaseFeature = -> Pad001
  Direction = (1,1,1)
  Length = 14
  Length2 = 100
  Profile = -> Sketch002
  Type = 0
FEATURE [PartDesign::CoordinateSystem] LCS_m1
  AttacherType = Attacher::AttachEngine3D
  AttachmentOffset = pos=(30,-25,0) rot=(0,0,1;0rad)
  MapMode = 5
  Placement = pos=(30,25,-18) rot=(1,0,0;3.14159rad)
  Support = -> [Pad002]
FEATURE [PartDesign::CoordinateSystem] LCS_h1
  AttacherType = Attacher::AttachEngine3D
  MapMode = 11
  Placement = pos=(50,-40,10) rot=(0,0,1;1.5708rad)
  Support = -> [Pad002]
FEATURE [PartDesign::CoordinateSystem] LCS_h2
  AttacherType = Attacher::AttachEngine3D
  MapMode = 11
  Placement = pos=(-50,-40,10) rot=(0,0,1;1.5708rad)
  Support = -> [Pad002]
FEATURE [PartDesign::CoordinateSystem] LCS_1
  AttacherType = Attacher::AttachEngine3D
  MapMode = 11
  Placement = pos=(30,-40,10) rot=(0,0,1;1.5708rad)
  Support = -> [Pad002]
FEATURE [PartDesign::CoordinateSystem] LCS_2
  AttacherType = Attacher::AttachEngine3D
  MapMode = 11
  Placement = pos=(-30,-40,10) rot=(0,0,1;1.5708rad)
  Support = -> [Pad002]
FEATURE [PartDesign::Body] Body
  Group = -> [Sketch,Pad,Sketch001,Pad001,Sketch002,Pad002,LCS_m1,LCS_h1,LCS_h2,LCS_1,LCS_2]
  Origin = -> Origin
  Tip = -> Pad002
---- part TRH15A.FCStd = doc fcstd_0c09d0aef553 ----
FCSTD DOCUMENT  (FreeCAD 0.19R)
Label: TRH15A
License: All rights reserved
LicenseURL: http://en.wikipedia.org/wiki/All_rights_reserved
objects: PartDesign::CoordinateSystem×6, Sketcher::SketchObject×5, PartDesign::Pad×4, PartDesign::Pocket×1, PartDesign::Body×1
note: 22 computed .brp shape members not serialized (recipe doc carries the construction recipe); baked Part::Feature solids carry a one-line shape summary decoded from their .brp

FEATURE [Sketcher::SketchObject] Sketch
  FullyConstrained = true
  MapMode = 5
  Placement = pos=(0,0,0) rot=(1,0,0;1.5708rad)
  Support = -> [XZ_Plane]
  sketch-geometry (12):
    g0: LineSegment StartX=-23.5 StartY=19.8 StartZ=0 EndX=23.5 EndY=19.8 EndZ=0
    g1: LineSegment StartX=-23.5 StartY=19.8 StartZ=0 EndX=-23.5 EndY=11.3 EndZ=0
    g2: LineSegment StartX=23.5 StartY=19.8 StartZ=0 EndX=23.5 EndY=11.3 EndZ=0
    g3: LineSegment StartX=-23.5 StartY=11.3 StartZ=0 EndX=-16.5 EndY=11.3 EndZ=0
    g4: LineSegment StartX=-15.5 StartY=0 StartZ=0 EndX=-16.5 EndY=11.3 EndZ=0
    g5: LineSegment StartX=-15.5 StartY=0 StartZ=0 EndX=-7.5 EndY=0 EndZ=0
    g6: LineSegment StartX=-7.5 StartY=0 StartZ=0 EndX=-7.5 EndY=10.8 EndZ=0
    g7: LineSegment StartX=-7.5 StartY=10.8 StartZ=0 EndX=7.5 EndY=10.8 EndZ=0
    g8: LineSegment StartX=7.5 StartY=10.8 StartZ=0 EndX=7.5 EndY=0 EndZ=0
    g9: LineSegment StartX=7.5 StartY=0 StartZ=0 EndX=15.5 EndY=0 EndZ=0
    g10: LineSegment StartX=15.5 StartY=0 StartZ=0 EndX=16.5 EndY=11.3 EndZ=0
    g11: LineSegment StartX=16.5 StartY=11.3 StartZ=0 EndX=23.5 EndY=11.3 EndZ=0
  constraints (34):
    c: Coincident(g1,g0)
    c: Vertical(g1)
    c: Coincident(g2,g0)
    c: Vertical(g2)
    c: Coincident(g3,g1)
    c: Horizontal(g3)
    c: Coincident(g4,g3)
    c: Coincident(g5,g4)
    c: Horizontal(g5)
    c: Coincident(g6,g5)
    c: Vertical(g6)
    c: Coincident(g7,g6)
    c: Horizontal(g7)
    c: Coincident(g8,g7)
    c: Vertical(g8)
    c: Coincident(g9,g8)
    c: Horizontal(g9)
    c: Coincident(g10,g9)
    c: Coincident(g11,g10)
    c: Coincident(g11,g2)
    c: Horizontal(g11)
    c: Symmetric(g0,g0,g-2)
    c: Equal(g3,g11)
    c: Equal(g1,g2)
    c: Equal(g9,g5)
    c: DistanceX(g7,g7) = 15
    c: DistanceX(g0,g0) = 47
    c: DistanceX(g4,g9) = 31
    c: PointOnObject(g9,g-1)
    c: DistanceY(g9,g0) = 19.8
    c: DistanceY(g1,g0) = 8.5
    c: DistanceX(g3,g10) = 33
    c: Symmetric(g4,g9,g-2)
    c: DistanceY(g6,g0) = 9
FEATURE [PartDesign::Pad] Pad
  Direction = (1,1,1)
  Length = 39.8
  Length2 = 100
  Placement = pos=(0,0,0) rot=(1,0,0;1.5708rad)
  Profile = -> Sketch
  Type = 0
FEATURE [Sketcher::SketchObject] Sketch001
  ExternalGeometry = -> [Pad]
  FullyConstrained = true
  MapMode = 5
  Placement = pos=(0,-39.8,8.8e-15) rot=(1,0,0;1.5708rad)
  Support = -> [Pad]
  sketch-geometry (8):
    g0: LineSegment StartX=-15.5 StartY=0 StartZ=0 EndX=-7.5 EndY=0 EndZ=0
    g1: LineSegment StartX=-7.5 StartY=0 StartZ=0 EndX=-7.5 EndY=10.8 EndZ=0
    g2: LineSegment StartX=-7.5 StartY=10.8 StartZ=0 EndX=7.5 EndY=10.8 EndZ=0
    g3: LineSegment StartX=7.5 StartY=10.8 StartZ=0 EndX=7.5 EndY=0 EndZ=0
    g4: LineSegment StartX=7.5 StartY=0 StartZ=0 EndX=15.5 EndY=0 EndZ=0
    g5: LineSegment StartX=-15.5 StartY=0 StartZ=0 EndX=-15.5 EndY=19.8 EndZ=0
    g6: LineSegment StartX=15.5 StartY=0 StartZ=0 EndX=15.5 EndY=19.8 EndZ=0
    g7: LineSegment StartX=-15.5 StartY=19.8 StartZ=0 EndX=15.5 EndY=19.8 EndZ=0
  constraints (18):
    c: Coincident(g0,g-7)
    c: Coincident(g0,g-7)
    c: Coincident(g1,g0)
    c: Coincident(g1,g-4)
    c: Coincident(g2,g1)
    c: Coincident(g2,g-5)
    c: Coincident(g3,g2)
    c: Coincident(g3,g-6)
    c: Coincident(g4,g3)
    c: Coincident(g4,g-6)
    c: Coincident(g5,g0)
    c: PointOnObject(g5,g-8)
    c: Vertical(g5)
    c: Coincident(g6,g4)
    c: PointOnObject(g6,g-8)
    c: Vertical(g6)
    c: Coincident(g7,g5)
    c: Coincident(g7,g6)
FEATURE [PartDesign::Pad] Pad001
  BaseFeature = -> Pad
  Direction = (1,1,1)
  Length = 11
  Length2 = 100
  Placement = pos=(0,0,0) rot=(1,0,0;1.5708rad)
  Profile = -> Sketch001
  Type = 0
FEATURE [Sketcher::SketchObject] Sketch002
  ExternalGeometry = -> [Pad001]
  FullyConstrained = true
  MapMode = 5
  Placement = pos=(0,0,0) rot=(-1,0,0;1.5708rad)
  Support = -> [Pad001]
  sketch-geometry (8):
    g0: LineSegment StartX=-15.5 StartY=0 StartZ=0 EndX=-7.5 EndY=0 EndZ=0
    g1: LineSegment StartX=-7.5 StartY=0 StartZ=0 EndX=-7.5 EndY=-10.8 EndZ=0
    g2: LineSegment StartX=-7.5 StartY=-10.8 StartZ=0 EndX=7.5 EndY=-10.8 EndZ=0
    g3: LineSegment StartX=7.5 StartY=-10.8 StartZ=0 EndX=7.5 EndY=0 EndZ=0
    g4: LineSegment StartX=7.5 StartY=0 StartZ=0 EndX=15.5 EndY=0 EndZ=0
    g5: LineSegment StartX=15.5 StartY=0 StartZ=0 EndX=15.5 EndY=-19.8 EndZ=0
    g6: LineSegment StartX=15.5 StartY=-19.8 StartZ=0 EndX=-15.5 EndY=-19.8 EndZ=0
    g7: LineSegment StartX=-15.5 StartY=-19.8 StartZ=0 EndX=-15.5 EndY=0 EndZ=0
  constraints (19):
    c: Coincident(g-3,g0)
    c: PointOnObject(g0,g-3)
    c: Coincident(g0,g1)
    c: Coincident(g1,g-5)
    c: Vertical(g1)
    c: Coincident(g1,g2)
    c: Coincident(g2,g-6)
    c: Coincident(g2,g3)
    c: Coincident(g3,g-7)
    c: Coincident(g3,g4)
    c: Coincident(g4,g5)
    c: Vertical(g5)
    c: Coincident(g5,g6)
    c: PointOnObject(g6,g-8)
    c: Horizontal(g6)
    c: Coincident(g6,g7)
    c: Coincident(g7,g0)
    c: Vertical(g7)
    c: Coincident(g-7,g4)
FEATURE [PartDesign::Pad] Pad002
  BaseFeature = -> Pad001
  Direction = (1,1,1)
  Length = 11
  Length2 = 100
  Placement = pos=(0,0,0) rot=(1,0,0;1.5708rad)
  Profile = -> Sketch002
  Type = 0
FEATURE [Sketcher::SketchObject] Sketch003
  ExternalGeometry = -> [Pad002]
  FullyConstrained = true
  MapMode = 5
  Placement = pos=(0,-50.8,3.66e-14) rot=(1,0,0;1.5708rad)
  Support = -> [Pad002]
  sketch-geometry (7):
    g0: LineSegment StartX=0 StartY=12.4132 StartZ=0 EndX=2.5 EndY=13.8566 EndZ=0
    g1: LineSegment StartX=2.5 StartY=13.8566 StartZ=0 EndX=2.5 EndY=16.7434 EndZ=0
    g2: LineSegment StartX=2.5 StartY=16.7434 StartZ=0 EndX=-4e-16 EndY=18.1868 EndZ=0
    g3: LineSegment StartX=-4e-16 StartY=18.1868 StartZ=0 EndX=-2.5 EndY=16.7434 EndZ=0
    g4: LineSegment StartX=-2.5 StartY=16.7434 StartZ=0 EndX=-2.5 EndY=13.8566 EndZ=0
    g5: LineSegment StartX=-2.5 StartY=13.8566 StartZ=0 EndX=0 EndY=12.4132 EndZ=0
    g6: Circle CenterX=0 CenterY=15.3 CenterZ=0 NormalX=0 NormalY=0 NormalZ=1 AngleXU=0 Radius=2.88675
  constraints (17):
    c: Coincident(g0,g1)
    c: Coincident(g1,g2)
    c: Coincident(g2,g3)
    c: Coincident(g3,g4)
    c: Coincident(g4,g5)
    c: Coincident(g5,g0)
    c: Equal(g0, g1-g5) x5
    c: PointOnObject(g0,g6)
    c: PointOnObject(g1,g6)
    c: PointOnObject(g2,g6)
    c: PointOnObject(g3,g6)
    c: PointOnObject(g4,g6)
    c: PointOnObject(g5,g6)
    c: PointOnObject(g6,g-2)
    c: PointOnObject(g0,g-2)
    c: DistanceX(g3,g1) = 5
    c: DistanceY(g6,g-3) = 4.5
FEATURE [PartDesign::Pad] Pad003
  BaseFeature = -> Pad002
  Direction = (1,1,1)
  Length = 6
  Length2 = 100
  Placement = pos=(0,0,0) rot=(1,0,0;1.5708rad)
  Profile = -> Sketch003
  Type = 0
FEATURE [Sketcher::SketchObject] Sketch004
  FullyConstrained = true
  MapMode = 5
  Placement = pos=(0,8.7e-15,19.8) rot=(0,0,1;3.14159rad)
  Support = -> [Pad003]
  sketch-geometry (4):
    g0: Circle CenterX=-19 CenterY=34.9 CenterZ=0 NormalX=0 NormalY=0 NormalZ=1 AngleXU=0 Radius=2.5
    g1: Circle CenterX=-19 CenterY=4.9 CenterZ=0 NormalX=0 NormalY=0 NormalZ=1 AngleXU=0 Radius=2.5
    g2: Circle CenterX=19 CenterY=4.9 CenterZ=0 NormalX=0 NormalY=0 NormalZ=1 AngleXU=0 Radius=2.5
    g3: Circle CenterX=19 CenterY=34.9 CenterZ=0 NormalX=0 NormalY=0 NormalZ=1 AngleXU=0 Radius=2.5
  constraints (10):
    c: Equal(g0,g3)
    c: Equal(g3,g2)
    c: Equal(g2,g1)
    c: Diameter(g3) = 5
    c: Symmetric(g1,g2,g-2)
    c: Symmetric(g3,g0,g-2)
    c: DistanceX(g0,g3) = 38
    c: DistanceX(g1,g2) = 38
    c: DistanceY(g2,g3) = 30
    c: DistanceY(g-1,g2) = 4.9
FEATURE [PartDesign::Pocket] Pocket
  BaseFeature = -> Pad003
  Length = 5
  Length2 = 100
  Placement = pos=(0,0,0) rot=(1,0,0;1.5708rad)
  Profile = -> Sketch004
  Type = 1
FEATURE [PartDesign::CoordinateSystem] LCS_MOUNT
  AttacherType = Attacher::AttachEngine3D
  MapMode = 5
  Placement = pos=(0,4.8e-15,10.8) rot=(1,0,0;3.14159rad)
  Support = -> [Pocket]
FEATURE [PartDesign::CoordinateSystem] LCS_TOP_MOUNT
  AttacherType = Attacher::AttachEngine3D
  AttachmentOffset = pos=(0,19.9,0) rot=(0,0,1;0rad)
  MapMode = 5
  Placement = pos=(0,-19.9,19.8) rot=(0,0,1;3.14159rad)
  Support = -> [Pocket]
FEATURE [PartDesign::CoordinateSystem] LCS_h1
  AttacherType = Attacher::AttachEngine3D
  MapMode = 11
  Placement = pos=(-19,-34.9,19.8) rot=(0,0,-1;1.5708rad)
  Support = -> [Pocket]
FEATURE [PartDesign::CoordinateSystem] LCS_h2
  AttacherType = Attacher::AttachEngine3D
  MapMode = 11
  Placement = pos=(-19,-4.9,19.8) rot=(0,0,-1;1.5708rad)
  Support = -> [Pocket]
FEATURE [PartDesign::CoordinateSystem] LCS_h3
  AttacherType = Attacher::AttachEngine3D
  MapMode = 11
  Placement = pos=(19,-34.9,19.8) rot=(0,0,-1;1.5708rad)
  Support = -> [Pocket]
FEATURE [PartDesign::CoordinateSystem] LCS_h4
  AttacherType = Attacher::AttachEngine3D
  MapMode = 11
  Placement = pos=(19,-4.9,19.8) rot=(0,0,-1;1.5708rad)
  Support = -> [Pocket]
FEATURE [PartDesign::Body] Body
  Group = -> [Sketch,Pad,Sketch001,Pad001,Sketch002,Pad002,Sketch003,Pad003,Sketch004,Pocket,LCS_MOUNT,LCS_TOP_MOUNT,LCS_h1,LCS_h2,LCS_h3,LCS_h4]
  Origin = -> Origin
  Tip = -> Pocket
---- part adapter_plate.FCStd = doc fcstd_5abff2c283b5 ----
FCSTD DOCUMENT  (FreeCAD 0.19R)
Label: adapter_plate
License: All rights reserved
LicenseURL: http://en.wikipedia.org/wiki/All_rights_reserved
objects: PartDesign::CoordinateSystem×8, Sketcher::SketchObject×3, PartDesign::Pocket×2, PartDesign::Pad×1, PartDesign::Body×1
note: 18 computed .brp shape members not serialized (recipe doc carries the construction recipe); baked Part::Feature solids carry a one-line shape summary decoded from their .brp

FEATURE [Sketcher::SketchObject] Sketch
  FullyConstrained = true
  MapMode = 5
  Placement = pos=(0,0,0) rot=(1,0,0;1.5708rad)
  Support = -> [XZ_Plane]
  sketch-geometry (12):
    g0: LineSegment StartX=-50 StartY=25 StartZ=0 EndX=50 EndY=25 EndZ=0
    g1: LineSegment StartX=50 StartY=0 StartZ=0 EndX=-50 EndY=0 EndZ=0
    g2: LineSegment StartX=-50 StartY=0 StartZ=0 EndX=-50 EndY=25 EndZ=0
    g3: LineSegment StartX=50 StartY=25 StartZ=0 EndX=50 EndY=0 EndZ=0
    g4: LineSegment StartX=-48 StartY=23 StartZ=0 EndX=-2 EndY=23 EndZ=0
    g5: LineSegment StartX=-2 StartY=23 StartZ=0 EndX=-2 EndY=2 EndZ=0
    g6: LineSegment StartX=-2 StartY=2 StartZ=0 EndX=-48 EndY=2 EndZ=0
    g7: LineSegment StartX=-48 StartY=2 StartZ=0 EndX=-48 EndY=23 EndZ=0
    g8: LineSegment StartX=2 StartY=23 StartZ=0 EndX=48 EndY=23 EndZ=0
    g9: LineSegment StartX=48 StartY=23 StartZ=0 EndX=48 EndY=2 EndZ=0
    g10: LineSegment StartX=48 StartY=2 StartZ=0 EndX=2 EndY=2 EndZ=0
    g11: LineSegment StartX=2 StartY=2 StartZ=0 EndX=2 EndY=23 EndZ=0
  constraints (34):
    c: Coincident(g1,g2)
    c: Coincident(g2,g0)
    c: Horizontal(g0)
    c: Vertical(g2)
    c: Vertical(g3)
    c: Coincident(g1,g3)
    c: Coincident(g0,g3)
    c: Symmetric(g1,g1,g-2)
    c: PointOnObject(g1,g-1)
    c: DistanceY(g3,g3) = 25
    c: DistanceX(g0,g0) = 100
    c: Coincident(g4,g5)
    c: Coincident(g5,g6)
    c: Coincident(g6,g7)
    c: Coincident(g7,g4)
    c: Horizontal(g4)
    c: Horizontal(g6)
    c: Vertical(g5)
    c: Vertical(g7)
    c: Coincident(g8,g9)
    c: Coincident(g9,g10)
    c: Coincident(g10,g11)
    c: Coincident(g11,g8)
    c: Horizontal(g8)
    c: Horizontal(g10)
    c: Vertical(g9)
    c: Vertical(g11)
    c: DistanceY(g8,g0) = 2
    c: DistanceX(g9,g1) = 2
    c: DistanceY(g1,g9) = 2
    c: DistanceX(g5,g10) = 4
    c: DistanceX(g1,g6) = 2
    c: DistanceY(g1,g6) = 2
    c: Symmetric(g8,g4,g-2)
FEATURE [PartDesign::Pad] Pad
  Direction = (1,1,1)
  Length = 190
  Length2 = 100
  Placement = pos=(0,0,0) rot=(1,0,0;1.5708rad)
  Profile = -> Sketch
  Type = 0
FEATURE [Sketcher::SketchObject] Sketch001
  FullyConstrained = true
  MapMode = 5
  Placement = pos=(0,0,0) rot=(1,0,0;3.14159rad)
  Support = -> [Pad]
  sketch-geometry (7):
    g0: Circle CenterX=-29.9821 CenterY=90 CenterZ=0 NormalX=0 NormalY=0 NormalZ=1 AngleXU=0 Radius=2.75
    g1: Circle CenterX=30.0179 CenterY=89.9866 CenterZ=0 NormalX=0 NormalY=0 NormalZ=1 AngleXU=0 Radius=2.75
    g2: LineSegment StartX=-29.9821 StartY=90 StartZ=0 EndX=30.0179 EndY=89.9866 EndZ=0
    g3: Circle CenterX=-30 CenterY=10 CenterZ=0 NormalX=0 NormalY=0 NormalZ=1 AngleXU=0 Radius=2.75
    g4: LineSegment StartX=-29.9821 StartY=90 StartZ=0 EndX=-30 EndY=10 EndZ=0
    g5: Circle CenterX=30 CenterY=9.98658 CenterZ=0 NormalX=0 NormalY=0 NormalZ=1 AngleXU=0 Radius=2.75
    g6: LineSegment StartX=-30 StartY=10 StartZ=0 EndX=30 EndY=9.98658 EndZ=0
  constraints (18):
    c: Diameter(g0) = 5.5
    c: Diameter(g1) = 5.5
    c: Coincident(g0,g2)
    c: Coincident(g1,g2)
    c: Distance(g2) = 60
    c: Angle(g2) = -0.000223728
    c: Diameter(g3) = 5.5
    c: Coincident(g0,g4)
    c: Coincident(g3,g4)
    c: Distance(g4) = 80
    c: Perpendicular(g4,g2)
    c: Diameter(g5) = 5.5
    c: Coincident(g3,g6)
    c: Coincident(g5,g6)
    c: Equal(g2,g6)
    c: Parallel(g6,g2)
    c: DistanceX(g3,g-1) = 30
    c: DistanceY(g-1,g3) = 10
FEATURE [PartDesign::Pocket] Pocket
  BaseFeature = -> Pad
  Length = 2
  Length2 = 100
  Placement = pos=(0,0,0) rot=(1,0,0;1.5708rad)
  Profile = -> Sketch001
  Type = 0
FEATURE [Sketcher::SketchObject] Sketch002
  ExternalGeometry = -> [Pocket]
  FullyConstrained = true
  MapMode = 5
  Placement = pos=(0,0,25) rot=(0,0,1;3.14159rad)
  Support = -> [Pocket]
  sketch-geometry (7):
    g0: Circle CenterX=-35 CenterY=180 CenterZ=0 NormalX=0 NormalY=0 NormalZ=1 AngleXU=0 Radius=3.25
    g1: Circle CenterX=35 CenterY=180 CenterZ=0 NormalX=0 NormalY=0 NormalZ=1 AngleXU=0 Radius=3.25
    g2: LineSegment StartX=-35 StartY=180 StartZ=0 EndX=35 EndY=180 EndZ=0
    g3: Circle CenterX=-35 CenterY=160 CenterZ=0 NormalX=0 NormalY=0 NormalZ=1 AngleXU=0 Radius=3.25
    g4: LineSegment StartX=-35 StartY=180 StartZ=0 EndX=-35 EndY=160 EndZ=0
    g5: Circle CenterX=35 CenterY=160 CenterZ=0 NormalX=0 NormalY=0 NormalZ=1 AngleXU=0 Radius=3.25
    g6: LineSegment StartX=-35 StartY=160 StartZ=0 EndX=35 EndY=160 EndZ=0
  constraints (18):
    c: Diameter(g0) = 6.5
    c: Diameter(g1) = 6.5
    c: Coincident(g0,g2)
    c: Coincident(g1,g2)
    c: Distance(g2) = 70
    c: Angle(g2) = 0
    c: Diameter(g3) = 6.5
    c: Coincident(g0,g4)
    c: Coincident(g3,g4)
    c: Distance(g4) = 20
    c: Perpendicular(g4,g2)
    c: Diameter(g5) = 6.5
    c: Coincident(g3,g6)
    c: Coincident(g5,g6)
    c: Equal(g2,g6)
    c: Parallel(g6,g2)
    c: DistanceY(g1,g-3) = 10
    c: Symmetric(g0,g1,g-2)
FEATURE [PartDesign::Pocket] Pocket001
  BaseFeature = -> Pocket
  Length = 2
  Length2 = 100
  Placement = pos=(0,0,0) rot=(1,0,0;1.5708rad)
  Profile = -> Sketch002
  Type = 0
FEATURE [PartDesign::CoordinateSystem] LCS_1
  AttacherType = Attacher::AttachEngine3D
  MapMode = 11
  Placement = pos=(-35,-180,25) rot=(0,0,-1;1.5708rad)
  Support = -> [Pocket001]
FEATURE [PartDesign::CoordinateSystem] LCS_2
  AttacherType = Attacher::AttachEngine3D
  MapMode = 11
  Placement = pos=(35,-180,25) rot=(0,0,-1;1.5708rad)
  Support = -> [Pocket001]
FEATURE [PartDesign::CoordinateSystem] LCS_3
  AttacherType = Attacher::AttachEngine3D
  MapMode = 11
  Placement = pos=(-35,-160,25) rot=(0,0,-1;1.5708rad)
  Support = -> [Pocket001]
FEATURE [PartDesign::CoordinateSystem] LCS_4
  AttacherType = Attacher::AttachEngine3D
  MapMode = 11
  Placement = pos=(35,-160,25) rot=(0,0,-1;1.5708rad)
  Support = -> [Pocket001]
FEATURE [PartDesign::CoordinateSystem] LCS_5
  AttacherType = Attacher::AttachEngine3D
  MapMode = 11
  Placement = pos=(30.0179,-89.9866,0) rot=(0.707107,-0.707107,0;3.14159rad)
  Support = -> [Pocket001]
FEATURE [PartDesign::CoordinateSystem] LCS_6
  AttacherType = Attacher::AttachEngine3D
  MapMode = 11
  Placement = pos=(-29.9821,-90,0) rot=(0.707107,-0.707107,0;3.14159rad)
  Support = -> [Pocket001]
FEATURE [PartDesign::CoordinateSystem] LCS_7
  AttacherType = Attacher::AttachEngine3D
  MapMode = 11
  Placement = pos=(30,-9.98658,0) rot=(0.707107,-0.707107,0;3.14159rad)
  Support = -> [Pocket001]
FEATURE [PartDesign::CoordinateSystem] LCS_8
  AttacherType = Attacher::AttachEngine3D
  MapMode = 11
  Placement = pos=(-30,-10,0) rot=(0.707107,-0.707107,0;3.14159rad)
  Support = -> [Pocket001]
FEATURE [PartDesign::Body] Body
  Group = -> [Sketch,Pad,Sketch001,Pocket,Sketch002,Pocket001,LCS_1,LCS_2,LCS_3,LCS_4,LCS_5,LCS_6,LCS_7,LCS_8]
  Origin = -> Origin
  Tip = -> Pocket001
---- part coupling.FCStd = doc fcstd_a23eb6f13819 ----
FCSTD DOCUMENT  (FreeCAD 0.19R)
Label: coupling
License: All rights reserved
LicenseURL: http://en.wikipedia.org/wiki/All_rights_reserved
objects: Sketcher::SketchObject×3, PartDesign::Pocket×2, PartDesign::CoordinateSystem×2, PartDesign::Pad×1, PartDesign::Body×1
note: 12 computed .brp shape members not serialized (recipe doc carries the construction recipe); baked Part::Feature solids carry a one-line shape summary decoded from their .brp

FEATURE [Sketcher::SketchObject] Sketch
  FullyConstrained = true
  MapMode = 5
  Placement = pos=(0,0,0) rot=(1,0,0;1.5708rad)
  Support = -> [XZ_Plane]
  sketch-geometry (1):
    g0: Circle CenterX=0 CenterY=0 CenterZ=0 NormalX=0 NormalY=0 NormalZ=1 AngleXU=0 Radius=12.5
  constraints (2):
    c: Coincident(g0,g-1)
    c: Diameter(g0) = 25
FEATURE [PartDesign::Pad] Pad
  Direction = (1,1,1)
  Length = 30
  Length2 = 100
  Placement = pos=(0,0,0) rot=(1,0,0;1.5708rad)
  Profile = -> Sketch
  Type = 0
FEATURE [Sketcher::SketchObject] Sketch001
  FullyConstrained = true
  MapMode = 5
  Placement = pos=(0,-30,6.6e-15) rot=(1,0,0;1.5708rad)
  Support = -> [Pad]
  sketch-geometry (1):
    g0: Circle CenterX=0 CenterY=0 CenterZ=0 NormalX=0 NormalY=0 NormalZ=1 AngleXU=0 Radius=5
  constraints (2):
    c: Coincident(g0,g-1)
    c: Diameter(g0) = 10
FEATURE [PartDesign::Pocket] Pocket
  BaseFeature = -> Pad
  Length = 10
  Length2 = 100
  Placement = pos=(0,0,0) rot=(1,0,0;1.5708rad)
  Profile = -> Sketch001
  Type = 0
FEATURE [Sketcher::SketchObject] Sketch002
  FullyConstrained = true
  MapMode = 5
  Placement = pos=(0,0,0) rot=(-1,0,0;1.5708rad)
  Support = -> [Pocket]
  sketch-geometry (1):
    g0: Circle CenterX=0 CenterY=0 CenterZ=0 NormalX=0 NormalY=0 NormalZ=1 AngleXU=0 Radius=4
  constraints (2):
    c: Coincident(g0,g-1)
    c: Diameter(g0) = 8
FEATURE [PartDesign::Pocket] Pocket001
  BaseFeature = -> Pocket
  Length = 10
  Length2 = 100
  Placement = pos=(0,0,0) rot=(1,0,0;1.5708rad)
  Profile = -> Sketch002
  Type = 0
FEATURE [PartDesign::CoordinateSystem] LCS_8MM
  AttacherType = Attacher::AttachEngine3D
  MapMode = 11
  Placement = pos=(0,-10,1.3e-14) rot=(0.57735,-0.57735,-0.57735;4.18879rad)
  Support = -> [Pocket001]
FEATURE [PartDesign::CoordinateSystem] LCS_10MM
  AttacherType = Attacher::AttachEngine3D
  MapMode = 11
  Placement = pos=(0,-20,1.1e-14) rot=(0.57735,-0.57735,0.57735;2.0944rad)
  Support = -> [Pocket001]
FEATURE [PartDesign::Body] Body
  Group = -> [Sketch,Pad,Sketch001,Pocket,Sketch002,Pocket001,LCS_8MM,LCS_10MM]
  Origin = -> Origin
  Tip = -> Pocket001
---- part nema_23.FCStd = doc fcstd_0c9470349177 ----
FCSTD DOCUMENT  (FreeCAD 0.19R)
Label: nema_23
License: All rights reserved
LicenseURL: http://en.wikipedia.org/wiki/All_rights_reserved
objects: Sketcher::SketchObject×4, PartDesign::Pad×4, PartDesign::CoordinateSystem×4, PartDesign::Body×1
note: 17 computed .brp shape members not serialized (recipe doc carries the construction recipe); baked Part::Feature solids carry a one-line shape summary decoded from their .brp

FEATURE [Sketcher::SketchObject] Sketch
  FullyConstrained = true
  MapMode = 5
  Placement = pos=(0,0,0) rot=(1,0,0;1.5708rad)
  Support = -> [XZ_Plane]
  sketch-geometry (12):
    g0: LineSegment StartX=-28 StartY=23.5 StartZ=0 EndX=-28 EndY=-23.5 EndZ=0
    g1: LineSegment StartX=28 StartY=23.5 StartZ=0 EndX=28 EndY=-23.5 EndZ=0
    g2: LineSegment StartX=-23.5 StartY=28 StartZ=0 EndX=23.5 EndY=28 EndZ=0
    g3: LineSegment StartX=-23.5 StartY=-28 StartZ=0 EndX=23.5 EndY=-28 EndZ=0
    g4: ArcOfCircle CenterX=-23.5 CenterY=-23.5 CenterZ=0 NormalX=0 NormalY=0 NormalZ=1 AngleXU=0 Radius=4.5 StartAngle=3.14159 EndAngle=4.71239
    g5: ArcOfCircle CenterX=-23.5 CenterY=23.5 CenterZ=0 NormalX=0 NormalY=0 NormalZ=1 AngleXU=0 Radius=4.5 StartAngle=1.5708 EndAngle=3.14159
    g6: ArcOfCircle CenterX=23.5 CenterY=23.5 CenterZ=0 NormalX=0 NormalY=0 NormalZ=1 AngleXU=0 Radius=4.5 StartAngle=6.28318 EndAngle=7.85398
    g7: ArcOfCircle CenterX=23.5 CenterY=-23.5 CenterZ=0 NormalX=0 NormalY=0 NormalZ=1 AngleXU=0 Radius=4.5 StartAngle=4.71239 EndAngle=6.28319
    g8: Circle CenterX=-23.5 CenterY=23.5 CenterZ=0 NormalX=0 NormalY=0 NormalZ=1 AngleXU=0 Radius=2.5
    g9: Circle CenterX=23.5 CenterY=23.5 CenterZ=0 NormalX=0 NormalY=0 NormalZ=1 AngleXU=0 Radius=2.5
    g10: Circle CenterX=-23.5 CenterY=-23.5 CenterZ=0 NormalX=0 NormalY=0 NormalZ=1 AngleXU=0 Radius=2.5
    g11: Circle CenterX=23.5 CenterY=-23.5 CenterZ=0 NormalX=0 NormalY=0 NormalZ=1 AngleXU=0 Radius=2.5
  constraints (33):
    c: Vertical(g0)
    c: Vertical(g1)
    c: Horizontal(g2)
    c: Coincident(g4,g0)
    c: Coincident(g4,g3)
    c: Coincident(g5,g2)
    c: Coincident(g6,g2)
    c: Coincident(g6,g1)
    c: Coincident(g7,g1)
    c: Coincident(g7,g3)
    c: Coincident(g5,g0)
    c: Equal(g9,g8)
    c: Equal(g8,g10)
    c: Equal(g10,g11)
    c: Diameter(g8) = 5
    c: Symmetric(g4,g7,g-2)
    c: Symmetric(g7,g6,g-1)
    c: Symmetric(g8,g9,g-2)
    c: Symmetric(g5,g6,g-2)
    c: Equal(g3,g0)
    c: Equal(g0,g2)
    c: Equal(g2,g1)
    c: DistanceX(g0,g1) = 56
    c: DistanceY(g3,g2) = 56
    c: Symmetric(g11,g9,g-1)
    c: Symmetric(g10,g11,g-2)
    c: DistanceX(g10,g11) = 47
    c: DistanceY(g11,g9) = 47
    c: Equal(g6,g5)
    c: Equal(g5,g4)
    c: Equal(g4,g7)
    c: Coincident(g7,g11)
    c: Radius(g5) = 4.5
FEATURE [PartDesign::Pad] Pad
  Direction = (1,1,1)
  Length = 5
  Length2 = 100
  Placement = pos=(0,0,0) rot=(1,0,0;1.5708rad)
  Profile = -> Sketch
  Type = 0
FEATURE [Sketcher::SketchObject] Sketch001
  FullyConstrained = true
  MapMode = 5
  Placement = pos=(0,-5,1.1e-15) rot=(1,0,0;1.5708rad)
  Support = -> [Pad]
  sketch-geometry (1):
    g0: Circle CenterX=0 CenterY=0 CenterZ=0 NormalX=0 NormalY=0 NormalZ=1 AngleXU=0 Radius=19.05
  constraints (2):
    c: Coincident(g0,g-1)
    c: Diameter(g0) = 38.1
FEATURE [PartDesign::Pad] Pad001
  BaseFeature = -> Pad
  Direction = (1,1,1)
  Length = 1.6
  Length2 = 100
  Placement = pos=(0,0,0) rot=(1,0,0;1.5708rad)
  Profile = -> Sketch001
  Type = 0
FEATURE [Sketcher::SketchObject] Sketch002
  FullyConstrained = true
  MapMode = 5
  Placement = pos=(0,-6.6,4.9e-15) rot=(1,0,0;1.5708rad)
  Support = -> [Pad001]
  sketch-geometry (1):
    g0: Circle CenterX=0 CenterY=0 CenterZ=0 NormalX=0 NormalY=0 NormalZ=1 AngleXU=0 Radius=4
  constraints (2):
    c: Coincident(g0,g-1)
    c: Diameter(g0) = 8
FEATURE [PartDesign::Pad] Pad002
  BaseFeature = -> Pad001
  Direction = (1,1,1)
  Length = 20.5
  Length2 = 100
  Placement = pos=(0,0,0) rot=(1,0,0;1.5708rad)
  Profile = -> Sketch002
  Type = 0
FEATURE [Sketcher::SketchObject] Sketch003
  ExternalGeometry = -> [Pad002]
  FullyConstrained = true
  MapMode = 5
  Placement = pos=(0,0,0) rot=(-1,0,0;1.5708rad)
  Support = -> [Pad002]
  sketch-geometry (8):
    g0: LineSegment StartX=-18.6419 StartY=28 StartZ=0 EndX=18.6419 EndY=28 EndZ=0
    g1: LineSegment StartX=28 StartY=18.6419 StartZ=0 EndX=28 EndY=-18.6419 EndZ=0
    g2: LineSegment StartX=-18.6419 StartY=-28 StartZ=0 EndX=18.6419 EndY=-28 EndZ=0
    g3: LineSegment StartX=-28 StartY=-18.6419 StartZ=0 EndX=-28 EndY=18.6419 EndZ=0
    g4: ArcOfCircle CenterX=-26.5 CenterY=-26.5 CenterZ=0 NormalX=0 NormalY=0 NormalZ=1 AngleXU=0 Radius=8 StartAngle=6.09457 EndAngle=8.0426
    g5: ArcOfCircle CenterX=26.5 CenterY=-26.5 CenterZ=0 NormalX=0 NormalY=0 NormalZ=1 AngleXU=0 Radius=8 StartAngle=1.38218 EndAngle=3.33021
    g6: ArcOfCircle CenterX=26.5 CenterY=26.5 CenterZ=0 NormalX=0 NormalY=0 NormalZ=1 AngleXU=0 Radius=8 StartAngle=2.95298 EndAngle=4.90101
    g7: ArcOfCircle CenterX=-26.5 CenterY=26.5 CenterZ=0 NormalX=0 NormalY=0 NormalZ=1 AngleXU=0 Radius=8 StartAngle=4.52377 EndAngle=6.4718
  constraints (24):
    c: PointOnObject(g2,g-6)
    c: PointOnObject(g1,g-3)
    c: PointOnObject(g0,g-4)
    c: PointOnObject(g3,g-5)
    c: Equal(g3,g1)
    c: Equal(g1,g0)
    c: Equal(g0,g2)
    c: Symmetric(g1,g1,g-1)
    c: Symmetric(g3,g3,g-1)
    c: Symmetric(g0,g0,g-2)
    c: Symmetric(g2,g2,g-2)
    c: Coincident(g4,g3)
    c: Coincident(g4,g2)
    c: Coincident(g5,g2)
    c: Coincident(g5,g1)
    c: Coincident(g6,g0)
    c: Coincident(g6,g1)
    c: Coincident(g7,g0)
    c: Coincident(g7,g3)
    c: Equal(g6,g7)
    c: Equal(g7,g5)
    c: Equal(g5,g4)
    c: DistanceX(g7,g6) = 53
    c: Radius(g6) = 8
FEATURE [PartDesign::Pad] Pad003
  BaseFeature = -> Pad002
  Direction = (1,1,1)
  Length = 78
  Length2 = 100
  Placement = pos=(0,0,0) rot=(1,0,0;1.5708rad)
  Profile = -> Sketch003
  Type = 0
FEATURE [PartDesign::CoordinateSystem] LCS_shaft
  AttacherType = Attacher::AttachEngine3D
  MapMode = 11
  Placement = pos=(0,-27.1,3.5e-14) rot=(0.57735,-0.57735,0.57735;2.0944rad)
  Support = -> [Pad003]
FEATURE [PartDesign::CoordinateSystem] LCS_m1
  AttacherType = Attacher::AttachEngine3D
  MapMode = 11
  Placement = pos=(-23.5,-5,23.5) rot=(0.57735,-0.57735,0.57735;2.0944rad)
  Support = -> [Pad003]
FEATURE [PartDesign::CoordinateSystem] LCS_m2
  AttacherType = Attacher::AttachEngine3D
  MapMode = 11
  Placement = pos=(23.5,-5,23.5) rot=(0.57735,-0.57735,0.57735;2.0944rad)
  Support = -> [Pad003]
FEATURE [PartDesign::CoordinateSystem] LCS_m3
  AttacherType = Attacher::AttachEngine3D
  MapMode = 11
  Placement = pos=(23.5,-5,-23.5) rot=(0.57735,-0.57735,0.57735;2.0944rad)
  Support = -> [Pad003]
FEATURE [PartDesign::Body] Body
  Group = -> [Sketch,Pad,Sketch001,Pad001,Sketch002,Pad002,Sketch003,Pad003,LCS_shaft,LCS_m1,LCS_m2,LCS_m3]
  Origin = -> Origin
  Tip = -> Pad003
---- part portal_column_left.FCStd = doc fcstd_3da35db866d3 ----
FCSTD DOCUMENT  (FreeCAD 0.19R)
Label: portal_column_left
License: All rights reserved
LicenseURL: http://en.wikipedia.org/wiki/All_rights_reserved
objects: PartDesign::CoordinateSystem×6, Sketcher::SketchObject×3, PartDesign::Pocket×2, PartDesign::Pad×1, PartDesign::Body×1
note: 16 computed .brp shape members not serialized (recipe doc carries the construction recipe); baked Part::Feature solids carry a one-line shape summary decoded from their .brp

FEATURE [Sketcher::SketchObject] Sketch
  FullyConstrained = true
  MapMode = 5
  Support = -> [XY_Plane]
  sketch-geometry (8):
    g0: LineSegment StartX=-30 StartY=30 StartZ=0 EndX=30 EndY=30 EndZ=0
    g1: LineSegment StartX=30 StartY=30 StartZ=0 EndX=30 EndY=-30 EndZ=0
    g2: LineSegment StartX=30 StartY=-30 StartZ=0 EndX=-30 EndY=-30 EndZ=0
    g3: LineSegment StartX=-30 StartY=-30 StartZ=0 EndX=-30 EndY=30 EndZ=0
    g4: LineSegment StartX=-27 StartY=27 StartZ=0 EndX=27 EndY=27 EndZ=0
    g5: LineSegment StartX=27 StartY=27 StartZ=0 EndX=27 EndY=-27 EndZ=0
    g6: LineSegment StartX=27 StartY=-27 StartZ=0 EndX=-27 EndY=-27 EndZ=0
    g7: LineSegment StartX=-27 StartY=-27 StartZ=0 EndX=-27 EndY=27 EndZ=0
  constraints (22):
    c: Coincident(g0,g1)
    c: Coincident(g1,g2)
    c: Coincident(g2,g3)
    c: Coincident(g3,g0)
    c: Horizontal(g2)
    c: Vertical(g1)
    c: Coincident(g4,g5)
    c: Coincident(g5,g6)
    c: Coincident(g6,g7)
    c: Coincident(g7,g4)
    c: Horizontal(g4)
    c: Horizontal(g6)
    c: Vertical(g5)
    c: Vertical(g7)
    c: Symmetric(g0,g0,g-2)
    c: Symmetric(g2,g0,g-1)
    c: DistanceY(g3,g3) = 60
    c: DistanceX(g0,g0) = 60
    c: DistanceX(g0,g4) = 3
    c: DistanceY(g4,g0) = 3
    c: DistanceY(g1,g5) = 3
    c: DistanceX(g5,g1) = 3
FEATURE [PartDesign::Pad] Pad
  Direction = (1,1,1)
  Length = 200
  Length2 = 100
  Profile = -> Sketch
  Type = 0
FEATURE [Sketcher::SketchObject] Sketch001
  FullyConstrained = true
  MapMode = 5
  Placement = pos=(0,-30,0) rot=(1,0,0;1.5708rad)
  Support = -> [Pad]
  sketch-geometry (4):
    g0: Circle CenterX=-20 CenterY=50 CenterZ=0 NormalX=0 NormalY=0 NormalZ=1 AngleXU=0 Radius=2.75
    g1: Circle CenterX=20 CenterY=50 CenterZ=0 NormalX=0 NormalY=0 NormalZ=1 AngleXU=0 Radius=2.75
    g2: Circle CenterX=-20 CenterY=10 CenterZ=0 NormalX=0 NormalY=0 NormalZ=1 AngleXU=0 Radius=2.75
    g3: Circle CenterX=20 CenterY=10 CenterZ=0 NormalX=0 NormalY=0 NormalZ=1 AngleXU=0 Radius=2.75
  constraints (10):
    c: Symmetric(g0,g1,g-2)
    c: Symmetric(g2,g3,g-2)
    c: Equal(g0,g1)
    c: Equal(g1,g2)
    c: Equal(g2,g3)
    c: Diameter(g1) = 5.5
    c: DistanceX(g0,g1) = 40
    c: DistanceX(g2,g3) = 40
    c: DistanceY(g2,g0) = 40
    c: DistanceY(g-1,g2) = 10
FEATURE [PartDesign::Pocket] Pocket
  BaseFeature = -> Pad
  Length = 3
  Length2 = 100
  Profile = -> Sketch001
  Type = 0
FEATURE [PartDesign::CoordinateSystem] LCS_h1
  AttacherType = Attacher::AttachEngine3D
  MapMode = 11
  Placement = pos=(-20,-30,10) rot=(0.57735,-0.57735,0.57735;2.0944rad)
  Support = -> [Pocket]
FEATURE [PartDesign::CoordinateSystem] LCS_h2
  AttacherType = Attacher::AttachEngine3D
  MapMode = 11
  Placement = pos=(20,-30,10) rot=(0.57735,-0.57735,0.57735;2.0944rad)
  Support = -> [Pocket]
FEATURE [Sketcher::SketchObject] Sketch002
  ExternalGeometry = -> [Pocket]
  FullyConstrained = true
  MapMode = 5
  Placement = pos=(30,0,0) rot=(0.57735,0.57735,0.57735;2.0944rad)
  Support = -> [Pocket]
  sketch-geometry (14):
    g0: Circle CenterX=-20 CenterY=190 CenterZ=0 NormalX=0 NormalY=0 NormalZ=1 AngleXU=0 Radius=2.75
    g1: Circle CenterX=20 CenterY=189.989 CenterZ=0 NormalX=0 NormalY=0 NormalZ=1 AngleXU=0 Radius=2.75
    g2: LineSegment StartX=-20 StartY=190 StartZ=0 EndX=20 EndY=189.989 EndZ=0
    g3: Circle CenterX=-20.0106 CenterY=150 CenterZ=0 NormalX=0 NormalY=0 NormalZ=1 AngleXU=0 Radius=2.75
    g4: LineSegment StartX=-20 StartY=190 StartZ=0 EndX=-20.0106 EndY=150 EndZ=0
    g5: Circle CenterX=19.9894 CenterY=149.989 CenterZ=0 NormalX=0 NormalY=0 NormalZ=1 AngleXU=0 Radius=2.75
    g6: LineSegment StartX=-20.0106 StartY=150 StartZ=0 EndX=19.9894 EndY=149.989 EndZ=0
    g7: Circle CenterX=-20 CenterY=110 CenterZ=0 NormalX=0 NormalY=0 NormalZ=1 AngleXU=0 Radius=2.75
    g8: Circle CenterX=20 CenterY=110 CenterZ=0 NormalX=0 NormalY=0 NormalZ=1 AngleXU=0 Radius=2.75
    g9: LineSegment StartX=-20 StartY=110 StartZ=0 EndX=20 EndY=110 EndZ=0
    g10: Circle CenterX=-20 CenterY=70 CenterZ=0 NormalX=0 NormalY=0 NormalZ=1 AngleXU=0 Radius=2.75
    g11: LineSegment StartX=-20 StartY=110 StartZ=0 EndX=-20 EndY=70 EndZ=0
    g12: Circle CenterX=20 CenterY=70 CenterZ=0 NormalX=0 NormalY=0 NormalZ=1 AngleXU=0 Radius=2.75
    g13: LineSegment StartX=-20 StartY=70 StartZ=0 EndX=20 EndY=70 EndZ=0
  constraints (36):
    c: Diameter(g0) = 5.5
    c: Diameter(g1) = 5.5
    c: Coincident(g0,g2)
    c: Coincident(g1,g2)
    c: Distance(g2) = 40
    c: Angle(g2) = -0.000265354
    c: Diameter(g3) = 5.5
    c: Coincident(g0,g4)
    c: Coincident(g3,g4)
    c: Equal(g4,g2)
    c: Perpendicular(g4,g2)
    c: Diameter(g5) = 5.5
    c: Coincident(g3,g6)
    c: Coincident(g5,g6)
    c: Equal(g2,g6)
    c: Parallel(g6,g2)
    c: DistanceY(g0,g-3) = 10
    c: DistanceX(g-3,g0) = 10
    c: Diameter(g7) = 5.5
    c: Diameter(g8) = 5.5
    c: Coincident(g7,g9)
    c: Coincident(g8,g9)
    c: Distance(g9) = 40
    c: Angle(g9) = 0
    c: Diameter(g10) = 5.5
    c: Coincident(g7,g11)
    c: Coincident(g10,g11)
    c: Equal(g11,g9)
    c: Perpendicular(g11,g9)
    c: Diameter(g12) = 5.5
    c: Coincident(g10,g13)
    c: Coincident(g12,g13)
    c: Equal(g9,g13)
    c: Parallel(g13,g9)
    c: DistanceX(g-3,g7) = 10
    c: DistanceY(g7,g3) = 40
FEATURE [PartDesign::Pocket] Pocket001
  BaseFeature = -> Pocket
  Length = 3
  Length2 = 100
  Profile = -> Sketch002
  Type = 0
FEATURE [PartDesign::CoordinateSystem] LCS_1
  AttacherType = Attacher::AttachEngine3D
  MapMode = 11
  Placement = pos=(30,19.9894,149.989) rot=(0.707107,0,0.707107;3.14159rad)
  Support = -> [Pocket001]
FEATURE [PartDesign::CoordinateSystem] LCS_2
  AttacherType = Attacher::AttachEngine3D
  MapMode = 11
  Placement = pos=(30,20,189.989) rot=(0.707107,0,0.707107;3.14159rad)
  Support = -> [Pocket001]
FEATURE [PartDesign::CoordinateSystem] LCS_3
  AttacherType = Attacher::AttachEngine3D
  MapMode = 11
  Placement = pos=(30,-20.0106,150) rot=(0.707107,0,0.707107;3.14159rad)
  Support = -> [Pocket001]
FEATURE [PartDesign::CoordinateSystem] LCS_4
  AttacherType = Attacher::AttachEngine3D
  MapMode = 11
  Placement = pos=(30,-20,190) rot=(0.707107,0,0.707107;3.14159rad)
  Support = -> [Pocket001]
FEATURE [PartDesign::Body] Body
  Group = -> [Sketch,Pad,Sketch001,Pocket,LCS_h1,LCS_h2,Sketch002,Pocket001,LCS_1,LCS_2,LCS_3,LCS_4]
  Origin = -> Origin
  Tip = -> Pocket001
---- part portal_column_right.FCStd = doc fcstd_e915a953ffc2 ----
FCSTD DOCUMENT  (FreeCAD 0.19R)
Label: portal_column_right
License: All rights reserved
LicenseURL: http://en.wikipedia.org/wiki/All_rights_reserved
objects: PartDesign::CoordinateSystem×6, Sketcher::SketchObject×3, PartDesign::Pocket×2, PartDesign::Pad×1, PartDesign::Body×1
note: 16 computed .brp shape members not serialized (recipe doc carries the construction recipe); baked Part::Feature solids carry a one-line shape summary decoded from their .brp

FEATURE [Sketcher::SketchObject] Sketch
  FullyConstrained = true
  MapMode = 5
  Support = -> [XY_Plane]
  sketch-geometry (8):
    g0: LineSegment StartX=-30 StartY=30 StartZ=0 EndX=30 EndY=30 EndZ=0
    g1: LineSegment StartX=30 StartY=30 StartZ=0 EndX=30 EndY=-30 EndZ=0
    g2: LineSegment StartX=30 StartY=-30 StartZ=0 EndX=-30 EndY=-30 EndZ=0
    g3: LineSegment StartX=-30 StartY=-30 StartZ=0 EndX=-30 EndY=30 EndZ=0
    g4: LineSegment StartX=-27 StartY=27 StartZ=0 EndX=27 EndY=27 EndZ=0
    g5: LineSegment StartX=27 StartY=27 StartZ=0 EndX=27 EndY=-27 EndZ=0
    g6: LineSegment StartX=27 StartY=-27 StartZ=0 EndX=-27 EndY=-27 EndZ=0
    g7: LineSegment StartX=-27 StartY=-27 StartZ=0 EndX=-27 EndY=27 EndZ=0
  constraints (22):
    c: Coincident(g0,g1)
    c: Coincident(g1,g2)
    c: Coincident(g2,g3)
    c: Coincident(g3,g0)
    c: Horizontal(g2)
    c: Vertical(g1)
    c: Coincident(g4,g5)
    c: Coincident(g5,g6)
    c: Coincident(g6,g7)
    c: Coincident(g7,g4)
    c: Horizontal(g4)
    c: Horizontal(g6)
    c: Vertical(g5)
    c: Vertical(g7)
    c: Symmetric(g0,g0,g-2)
    c: Symmetric(g2,g0,g-1)
    c: DistanceY(g3,g3) = 60
    c: DistanceX(g0,g0) = 60
    c: DistanceX(g0,g4) = 3
    c: DistanceY(g4,g0) = 3
    c: DistanceY(g1,g5) = 3
    c: DistanceX(g5,g1) = 3
FEATURE [PartDesign::Pad] Pad
  Direction = (1,1,1)
  Length = 200
  Length2 = 100
  Profile = -> Sketch
  Type = 0
FEATURE [Sketcher::SketchObject] Sketch001
  FullyConstrained = true
  MapMode = 5
  Placement = pos=(0,-30,0) rot=(1,0,0;1.5708rad)
  Support = -> [Pad]
  sketch-geometry (4):
    g0: Circle CenterX=-20 CenterY=50 CenterZ=0 NormalX=0 NormalY=0 NormalZ=1 AngleXU=0 Radius=2.75
    g1: Circle CenterX=20 CenterY=50 CenterZ=0 NormalX=0 NormalY=0 NormalZ=1 AngleXU=0 Radius=2.75
    g2: Circle CenterX=-20 CenterY=10 CenterZ=0 NormalX=0 NormalY=0 NormalZ=1 AngleXU=0 Radius=2.75
    g3: Circle CenterX=20 CenterY=10 CenterZ=0 NormalX=0 NormalY=0 NormalZ=1 AngleXU=0 Radius=2.75
  constraints (10):
    c: Symmetric(g0,g1,g-2)
    c: Symmetric(g2,g3,g-2)
    c: Equal(g0,g1)
    c: Equal(g1,g2)
    c: Equal(g2,g3)
    c: Diameter(g1) = 5.5
    c: DistanceX(g0,g1) = 40
    c: DistanceX(g2,g3) = 40
    c: DistanceY(g2,g0) = 40
    c: DistanceY(g-1,g2) = 10
FEATURE [PartDesign::Pocket] Pocket
  BaseFeature = -> Pad
  Length = 3
  Length2 = 100
  Profile = -> Sketch001
  Type = 0
FEATURE [PartDesign::CoordinateSystem] LCS_h1
  AttacherType = Attacher::AttachEngine3D
  MapMode = 11
  Placement = pos=(-20,-30,10) rot=(0.57735,-0.57735,0.57735;2.0944rad)
  Support = -> [Pocket]
FEATURE [PartDesign::CoordinateSystem] LCS_h2
  AttacherType = Attacher::AttachEngine3D
  MapMode = 11
  Placement = pos=(20,-30,10) rot=(0.57735,-0.57735,0.57735;2.0944rad)
  Support = -> [Pocket]
FEATURE [Sketcher::SketchObject] Sketch002
  ExternalGeometry = -> [Pocket]
  FullyConstrained = true
  MapMode = 5
  Placement = pos=(-30,0,0) rot=(0.57735,-0.57735,-0.57735;2.0944rad)
  Support = -> [Pocket]
  sketch-geometry (14):
    g0: Circle CenterX=-20 CenterY=190 CenterZ=0 NormalX=0 NormalY=0 NormalZ=1 AngleXU=0 Radius=2.75
    g1: Circle CenterX=20 CenterY=190 CenterZ=0 NormalX=0 NormalY=0 NormalZ=1 AngleXU=0 Radius=2.75
    g2: LineSegment StartX=-20 StartY=190 StartZ=0 EndX=20 EndY=190 EndZ=0
    g3: Circle CenterX=-20 CenterY=150 CenterZ=0 NormalX=0 NormalY=0 NormalZ=1 AngleXU=0 Radius=2.75
    g4: LineSegment StartX=-20 StartY=190 StartZ=0 EndX=-20 EndY=150 EndZ=0
    g5: Circle CenterX=-60 CenterY=150 CenterZ=0 NormalX=0 NormalY=0 NormalZ=1 AngleXU=0 Radius=2.75
    g6: LineSegment StartX=-20 StartY=150 StartZ=0 EndX=-60 EndY=150 EndZ=0
    g7: Circle CenterX=-20 CenterY=110 CenterZ=0 NormalX=0 NormalY=0 NormalZ=1 AngleXU=0 Radius=2.75
    g8: Circle CenterX=20 CenterY=110 CenterZ=0 NormalX=0 NormalY=0 NormalZ=1 AngleXU=0 Radius=2.75
    g9: LineSegment StartX=-20 StartY=110 StartZ=0 EndX=20 EndY=110 EndZ=0
    g10: Circle CenterX=-20 CenterY=70 CenterZ=0 NormalX=0 NormalY=0 NormalZ=1 AngleXU=0 Radius=2.75
    g11: LineSegment StartX=-20 StartY=110 StartZ=0 EndX=-20 EndY=70 EndZ=0
    g12: Circle CenterX=20 CenterY=70 CenterZ=0 NormalX=0 NormalY=0 NormalZ=1 AngleXU=0 Radius=2.75
    g13: LineSegment StartX=-20 StartY=70 StartZ=0 EndX=20 EndY=70 EndZ=0
  constraints (36):
    c: Diameter(g0) = 5.5
    c: Diameter(g1) = 5.5
    c: Coincident(g0,g2)
    c: Coincident(g1,g2)
    c: Distance(g2) = 40
    c: Angle(g2) = 0
    c: Diameter(g3) = 5.5
    c: Coincident(g0,g4)
    c: Coincident(g3,g4)
    c: Equal(g4,g2)
    c: Perpendicular(g4,g2)
    c: Diameter(g5) = 5.5
    c: Coincident(g3,g6)
    c: Coincident(g5,g6)
    c: Equal(g2,g6)
    c: Parallel(g6,g2)
    c: DistanceY(g1,g-3) = 10
    c: DistanceX(g1,g-3) = 10
    c: Diameter(g7) = 5.5
    c: DistanceX(g-3,g7) = 10
    c: DistanceY(g7,g3) = 40
    c: Diameter(g8) = 5.5
    c: Coincident(g7,g9)
    c: Coincident(g8,g9)
    c: Distance(g9) = 40
    c: Diameter(g10) = 5.5
    c: Coincident(g7,g11)
    c: Coincident(g10,g11)
    c: Equal(g11,g9)
    c: Perpendicular(g11,g9)
    c: Diameter(g12) = 5.5
    c: Coincident(g10,g13)
    c: Coincident(g12,g13)
    c: Equal(g9,g13)
    c: Parallel(g13,g9)
    c: Horizontal(g9)
FEATURE [PartDesign::Pocket] Pocket001
  BaseFeature = -> Pocket
  Length = 3
  Length2 = 100
  Profile = -> Sketch002
  Type = 0
FEATURE [PartDesign::CoordinateSystem] LCS_1
  AttacherType = Attacher::AttachEngine3D
  MapMode = 11
  Placement = pos=(-30,-20,190) rot=(0,-1,0;1.5708rad)
  Support = -> [Pocket001]
FEATURE [PartDesign::CoordinateSystem] LCS_2
  AttacherType = Attacher::AttachEngine3D
  MapMode = 11
  Placement = pos=(-30,20,150) rot=(0,-1,0;1.5708rad)
  Support = -> [Pocket001]
FEATURE [PartDesign::CoordinateSystem] LCS_3
  AttacherType = Attacher::AttachEngine3D
  MapMode = 11
  Placement = pos=(-30,20,190) rot=(0,-1,0;1.5708rad)
  Support = -> [Pocket001]
FEATURE [PartDesign::CoordinateSystem] LCS_4
  AttacherType = Attacher::AttachEngine3D
  MapMode = 11
  Placement = pos=(-30,-20,110) rot=(0,-1,0;1.5708rad)
  Support = -> [Pocket001]
FEATURE [PartDesign::Body] Body
  Group = -> [Sketch,Pad,Sketch001,Pocket,LCS_h1,LCS_h2,Sketch002,Pocket001,LCS_1,LCS_2,LCS_3,LCS_4]
  Origin = -> Origin
  Tip = -> Pocket001
---- part portal_support_tube.FCStd = doc fcstd_07ee1f6aef2b ----
FCSTD DOCUMENT  (FreeCAD 0.19R)
Label: portal_support_tube
License: All rights reserved
LicenseURL: http://en.wikipedia.org/wiki/All_rights_reserved
objects: PartDesign::CoordinateSystem×18, Sketcher::SketchObject×4, PartDesign::Pocket×3, PartDesign::Pad×1, PartDesign::Body×1
note: 31 computed .brp shape members not serialized (recipe doc carries the construction recipe); baked Part::Feature solids carry a one-line shape summary decoded from their .brp

FEATURE [Sketcher::SketchObject] Sketch
  FullyConstrained = true
  MapMode = 5
  Placement = pos=(0,0,0) rot=(1,0,0;1.5708rad)
  Support = -> [XZ_Plane]
  sketch-geometry (8):
    g0: LineSegment StartX=-30 StartY=30 StartZ=0 EndX=30 EndY=30 EndZ=0
    g1: LineSegment StartX=30 StartY=30 StartZ=0 EndX=30 EndY=-30 EndZ=0
    g2: LineSegment StartX=30 StartY=-30 StartZ=0 EndX=-30 EndY=-30 EndZ=0
    g3: LineSegment StartX=-30 StartY=-30 StartZ=0 EndX=-30 EndY=30 EndZ=0
    g4: LineSegment StartX=-27 StartY=27 StartZ=0 EndX=27 EndY=27 EndZ=0
    g5: LineSegment StartX=27 StartY=27 StartZ=0 EndX=27 EndY=-27 EndZ=0
    g6: LineSegment StartX=27 StartY=-27 StartZ=0 EndX=-27 EndY=-27 EndZ=0
    g7: LineSegment StartX=-27 StartY=-27 StartZ=0 EndX=-27 EndY=27 EndZ=0
  constraints (22):
    c: Coincident(g0,g1)
    c: Coincident(g1,g2)
    c: Coincident(g2,g3)
    c: Coincident(g3,g0)
    c: Horizontal(g0)
    c: Vertical(g3)
    c: Symmetric(g2,g1,g-2)
    c: Symmetric(g1,g0,g-1)
    c: DistanceX(g2,g2) = 60
    c: DistanceY(g1,g1) = 60
    c: Coincident(g4,g5)
    c: Coincident(g5,g6)
    c: Coincident(g6,g7)
    c: Coincident(g7,g4)
    c: Horizontal(g4)
    c: Horizontal(g6)
    c: Vertical(g5)
    c: Vertical(g7)
    c: DistanceY(g4,g0) = 3
    c: DistanceX(g4,g0) = 3
    c: DistanceY(g2,g6) = 3
    c: DistanceX(g2,g6) = 3
FEATURE [PartDesign::Pad] Pad
  Direction = (1,1,1)
  Length = 120
  Length2 = 100
  Placement = pos=(0,0,0) rot=(1,0,0;1.5708rad)
  Profile = -> Sketch
  Type = 0
FEATURE [Sketcher::SketchObject] Sketch001
  ExternalGeometry = -> [Pad]
  FullyConstrained = true
  MapMode = 5
  Placement = pos=(0,0,-30) rot=(1,0,0;3.14159rad)
  Support = -> [Pad]
  sketch-geometry (8):
    g0: Circle CenterX=-19 CenterY=108 CenterZ=0 NormalX=0 NormalY=0 NormalZ=1 AngleXU=0 Radius=2.75
    g1: Circle CenterX=-19 CenterY=78 CenterZ=0 NormalX=0 NormalY=0 NormalZ=1 AngleXU=0 Radius=2.75
    g2: Circle CenterX=19 CenterY=108 CenterZ=0 NormalX=0 NormalY=0 NormalZ=1 AngleXU=0 Radius=2.75
    g3: Circle CenterX=19 CenterY=78 CenterZ=0 NormalX=0 NormalY=0 NormalZ=1 AngleXU=0 Radius=2.75
    g4: Circle CenterX=-19 CenterY=42 CenterZ=0 NormalX=0 NormalY=0 NormalZ=1 AngleXU=0 Radius=2.75
    g5: Circle CenterX=-19 CenterY=12 CenterZ=0 NormalX=0 NormalY=0 NormalZ=1 AngleXU=0 Radius=2.75
    g6: Circle CenterX=19 CenterY=42 CenterZ=0 NormalX=0 NormalY=0 NormalZ=1 AngleXU=0 Radius=2.75
    g7: Circle CenterX=19 CenterY=12 CenterZ=0 NormalX=0 NormalY=0 NormalZ=1 AngleXU=0 Radius=2.75
  constraints (20):
    c: Equal(g0,g2)
    c: Equal(g2,g1)
    c: Equal(g1,g3)
    c: Equal(g3,g4)
    c: Equal(g4,g6)
    c: Equal(g6,g7)
    c: Equal(g7,g5)
    c: Symmetric(g0,g2,g-2)
    c: Symmetric(g1,g3,g-2)
    c: Symmetric(g4,g6,g-2)
    c: Symmetric(g5,g7,g-2)
    c: DistanceY(g3,g2) = 30
    c: DistanceX(g0,g2) = 38
    c: DistanceX(g1,g3) = 38
    c: DistanceX(g4,g6) = 38
    c: DistanceX(g5,g7) = 38
    c: DistanceY(g7,g6) = 30
    c: Diameter(g2) = 5.5
    c: DistanceY(g-1,g7) = 12
    c: DistanceY(g2,g-3) = 12
FEATURE [PartDesign::Pocket] Pocket
  BaseFeature = -> Pad
  Length = 3
  Length2 = 100
  Placement = pos=(0,0,0) rot=(1,0,0;1.5708rad)
  Profile = -> Sketch001
  Type = 0
FEATURE [PartDesign::CoordinateSystem] LCS_h1
  AttacherType = Attacher::AttachEngine3D
  MapMode = 11
  Placement = pos=(-19,-108,-30) rot=(0.707107,-0.707107,0;3.14159rad)
  Support = -> [Pocket]
FEATURE [PartDesign::CoordinateSystem] LCS_h2
  AttacherType = Attacher::AttachEngine3D
  MapMode = 11
  Placement = pos=(19,-108,-30) rot=(0.707107,-0.707107,0;3.14159rad)
  Support = -> [Pocket]
FEATURE [PartDesign::CoordinateSystem] LCS_h3
  AttacherType = Attacher::AttachEngine3D
  MapMode = 11
  Placement = pos=(-19,-78,-30) rot=(0.707107,-0.707107,0;3.14159rad)
  Support = -> [Pocket]
FEATURE [PartDesign::CoordinateSystem] LCS_h4
  AttacherType = Attacher::AttachEngine3D
  MapMode = 11
  Placement = pos=(19,-78,-30) rot=(0.707107,-0.707107,0;3.14159rad)
  Support = -> [Pocket]
FEATURE [PartDesign::CoordinateSystem] LCS_h5
  AttacherType = Attacher::AttachEngine3D
  MapMode = 11
  Placement = pos=(-19,-42,-30) rot=(0.707107,-0.707107,0;3.14159rad)
  Support = -> [Pocket]
FEATURE [PartDesign::CoordinateSystem] LCS_h6
  AttacherType = Attacher::AttachEngine3D
  MapMode = 11
  Placement = pos=(19,-42,-30) rot=(0.707107,-0.707107,0;3.14159rad)
  Support = -> [Pocket]
FEATURE [PartDesign::CoordinateSystem] LCS_h7
  AttacherType = Attacher::AttachEngine3D
  MapMode = 11
  Placement = pos=(-19,-12,-30) rot=(0.707107,-0.707107,0;3.14159rad)
  Support = -> [Pocket]
FEATURE [PartDesign::CoordinateSystem] LCS_h8
  AttacherType = Attacher::AttachEngine3D
  MapMode = 11
  Placement = pos=(19,-12,-30) rot=(0.707107,-0.707107,0;3.14159rad)
  Support = -> [Pocket]
FEATURE [Sketcher::SketchObject] Sketch002
  FullyConstrained = true
  MapMode = 5
  Placement = pos=(0,0,30) rot=(0,0,1;3.14159rad)
  Support = -> [Pocket]
  sketch-geometry (4):
    g0: Circle CenterX=-20 CenterY=46 CenterZ=0 NormalX=0 NormalY=0 NormalZ=1 AngleXU=0 Radius=2.75
    g1: Circle CenterX=-20 CenterY=22 CenterZ=0 NormalX=0 NormalY=0 NormalZ=1 AngleXU=0 Radius=2.75
    g2: Circle CenterX=20 CenterY=46 CenterZ=0 NormalX=0 NormalY=0 NormalZ=1 AngleXU=0 Radius=2.75
    g3: Circle CenterX=20 CenterY=22 CenterZ=0 NormalX=0 NormalY=0 NormalZ=1 AngleXU=0 Radius=2.75
  constraints (10):
    c: DistanceY(g-1,g1) = 22
    c: Equal(g1,g3)
    c: Equal(g3,g2)
    c: Equal(g2,g0)
    c: Diameter(g3) = 5.5
    c: Symmetric(g3,g1,g-2)
    c: Symmetric(g2,g0,g-2)
    c: DistanceY(g3,g2) = 24
    c: DistanceX(g0,g2) = 40
    c: DistanceX(g1,g3) = 40
FEATURE [PartDesign::Pocket] Pocket001
  BaseFeature = -> Pocket
  Length = 3
  Length2 = 100
  Placement = pos=(0,0,0) rot=(1,0,0;1.5708rad)
  Profile = -> Sketch002
  Type = 0
FEATURE [PartDesign::CoordinateSystem] LCS_m1
  AttacherType = Attacher::AttachEngine3D
  MapMode = 11
  Placement = pos=(-20,-46,30) rot=(0,0,-1;1.5708rad)
  Support = -> [Pocket001]
FEATURE [PartDesign::CoordinateSystem] LCS_m2
  AttacherType = Attacher::AttachEngine3D
  MapMode = 11
  Placement = pos=(20,-46,30) rot=(0,0,-1;1.5708rad)
  Support = -> [Pocket001]
FEATURE [PartDesign::CoordinateSystem] LCS_m3
  AttacherType = Attacher::AttachEngine3D
  MapMode = 11
  Placement = pos=(-20,-22,30) rot=(0,0,-1;1.5708rad)
  Support = -> [Pocket001]
FEATURE [PartDesign::CoordinateSystem] LCS_m4
  AttacherType = Attacher::AttachEngine3D
  MapMode = 11
  Placement = pos=(20,-22,30) rot=(0,0,-1;1.5708rad)
  Support = -> [Pocket001]
FEATURE [PartDesign::CoordinateSystem] LCS_mh1
  AttacherType = Attacher::AttachEngine3D
  MapMode = 11
  Placement = pos=(20,-22,27) rot=(0,0,-1;1.5708rad)
  Support = -> [Pocket001]
FEATURE [PartDesign::CoordinateSystem] LCS_mh2
  AttacherType = Attacher::AttachEngine3D
  MapMode = 11
  Placement = pos=(-20,-22,27) rot=(0,0,-1;1.5708rad)
  Support = -> [Pocket001]
FEATURE [PartDesign::CoordinateSystem] LCS_mh3
  AttacherType = Attacher::AttachEngine3D
  MapMode = 11
  Placement = pos=(20,-46,27) rot=(0,0,-1;1.5708rad)
  Support = -> [Pocket001]
FEATURE [PartDesign::CoordinateSystem] LCS_mh4
  AttacherType = Attacher::AttachEngine3D
  MapMode = 11
  Placement = pos=(-20,-46,27) rot=(0,0,-1;1.5708rad)
  Support = -> [Pocket001]
FEATURE [Sketcher::SketchObject] Sketch003
  ExternalGeometry = -> [Pocket001]
  FullyConstrained = true
  MapMode = 5
  Placement = pos=(-30,0,0) rot=(0.707107,0,-0.707107;3.14159rad)
  Support = -> [Pocket001]
  sketch-geometry (4):
    g0: Circle CenterX=-20 CenterY=110 CenterZ=0 NormalX=0 NormalY=0 NormalZ=1 AngleXU=0 Radius=3
    g1: Circle CenterX=20 CenterY=110 CenterZ=0 NormalX=0 NormalY=0 NormalZ=1 AngleXU=0 Radius=3
    g2: Circle CenterX=-20 CenterY=70 CenterZ=0 NormalX=0 NormalY=0 NormalZ=1 AngleXU=0 Radius=3
    g3: Circle CenterX=20 CenterY=70 CenterZ=0 NormalX=0 NormalY=0 NormalZ=1 AngleXU=0 Radius=3
  constraints (10):
    c: Equal(g2,g3)
    c: Equal(g3,g1)
    c: Equal(g1,g0)
    c: Diameter(g1) = 6
    c: Symmetric(g2,g3,g-2)
    c: Symmetric(g1,g0,g-2)
    c: DistanceX(g0,g1) = 40
    c: DistanceX(g2,g3) = 40
    c: DistanceY(g2,g0) = 40
    c: DistanceY(g1,g-4) = 10
FEATURE [PartDesign::Pocket] Pocket002
  BaseFeature = -> Pocket001
  Length = 3
  Length2 = 100
  Placement = pos=(0,0,0) rot=(1,0,0;1.5708rad)
  Profile = -> Sketch003
  Type = 0
FEATURE [PartDesign::CoordinateSystem] LCS_ch1
  AttacherType = Attacher::AttachEngine3D
  MapMode = 11
  Placement = pos=(-30,-70,-20) rot=(0.57735,-0.57735,-0.57735;2.0944rad)
  Support = -> [Pocket002]
FEATURE [PartDesign::CoordinateSystem] LCS_ch2
  AttacherType = Attacher::AttachEngine3D
  MapMode = 11
  Placement = pos=(-30,-110,-20) rot=(0.57735,-0.57735,-0.57735;2.0944rad)
  Support = -> [Pocket002]
FEATURE [PartDesign::Body] Body
  Group = -> [Sketch,Pad,Sketch001,Pocket,LCS_h1,LCS_h2,LCS_h3,LCS_h4,LCS_h5,LCS_h6,LCS_h7,LCS_h8,Sketch002,Pocket001,LCS_m1,LCS_m2,LCS_m3,LCS_m4,LCS_mh1,LCS_mh2,LCS_mh3,LCS_mh4,Sketch003,Pocket002,LCS_ch1,LCS_ch2]
  Origin = -> Origin
  Tip = -> Pocket002
---- part portal_support_tube_left.FCStd = doc fcstd_ca9381cce950 ----
FCSTD DOCUMENT  (FreeCAD 0.19R)
Label: portal_support_tube_left
License: All rights reserved
LicenseURL: http://en.wikipedia.org/wiki/All_rights_reserved
objects: PartDesign::CoordinateSystem×18, Sketcher::SketchObject×4, PartDesign::Pocket×3, PartDesign::Pad×1, PartDesign::Body×1
note: 31 computed .brp shape members not serialized (recipe doc carries the construction recipe); baked Part::Feature solids carry a one-line shape summary decoded from their .brp

FEATURE [Sketcher::SketchObject] Sketch
  FullyConstrained = true
  MapMode = 5
  Placement = pos=(0,0,0) rot=(1,0,0;1.5708rad)
  Support = -> [XZ_Plane]
  sketch-geometry (8):
    g0: LineSegment StartX=-30 StartY=30 StartZ=0 EndX=30 EndY=30 EndZ=0
    g1: LineSegment StartX=30 StartY=30 StartZ=0 EndX=30 EndY=-30 EndZ=0
    g2: LineSegment StartX=30 StartY=-30 StartZ=0 EndX=-30 EndY=-30 EndZ=0
    g3: LineSegment StartX=-30 StartY=-30 StartZ=0 EndX=-30 EndY=30 EndZ=0
    g4: LineSegment StartX=-27 StartY=27 StartZ=0 EndX=27 EndY=27 EndZ=0
    g5: LineSegment StartX=27 StartY=27 StartZ=0 EndX=27 EndY=-27 EndZ=0
    g6: LineSegment StartX=27 StartY=-27 StartZ=0 EndX=-27 EndY=-27 EndZ=0
    g7: LineSegment StartX=-27 StartY=-27 StartZ=0 EndX=-27 EndY=27 EndZ=0
  constraints (22):
    c: Coincident(g0,g1)
    c: Coincident(g1,g2)
    c: Coincident(g2,g3)
    c: Coincident(g3,g0)
    c: Horizontal(g0)
    c: Vertical(g3)
    c: Symmetric(g2,g1,g-2)
    c: Symmetric(g1,g0,g-1)
    c: DistanceX(g2,g2) = 60
    c: DistanceY(g1,g1) = 60
    c: Coincident(g4,g5)
    c: Coincident(g5,g6)
    c: Coincident(g6,g7)
    c: Coincident(g7,g4)
    c: Horizontal(g4)
    c: Horizontal(g6)
    c: Vertical(g5)
    c: Vertical(g7)
    c: DistanceY(g4,g0) = 3
    c: DistanceX(g4,g0) = 3
    c: DistanceY(g2,g6) = 3
    c: DistanceX(g2,g6) = 3
FEATURE [PartDesign::Pad] Pad
  Direction = (1,1,1)
  Length = 120
  Length2 = 100
  Placement = pos=(0,0,0) rot=(1,0,0;1.5708rad)
  Profile = -> Sketch
  Type = 0
FEATURE [Sketcher::SketchObject] Sketch001
  ExternalGeometry = -> [Pad]
  FullyConstrained = true
  MapMode = 5
  Placement = pos=(0,0,-30) rot=(1,0,0;3.14159rad)
  Support = -> [Pad]
  sketch-geometry (8):
    g0: Circle CenterX=-19 CenterY=108 CenterZ=0 NormalX=0 NormalY=0 NormalZ=1 AngleXU=0 Radius=2.75
    g1: Circle CenterX=-19 CenterY=78 CenterZ=0 NormalX=0 NormalY=0 NormalZ=1 AngleXU=0 Radius=2.75
    g2: Circle CenterX=19 CenterY=108 CenterZ=0 NormalX=0 NormalY=0 NormalZ=1 AngleXU=0 Radius=2.75
    g3: Circle CenterX=19 CenterY=78 CenterZ=0 NormalX=0 NormalY=0 NormalZ=1 AngleXU=0 Radius=2.75
    g4: Circle CenterX=-19 CenterY=42 CenterZ=0 NormalX=0 NormalY=0 NormalZ=1 AngleXU=0 Radius=2.75
    g5: Circle CenterX=-19 CenterY=12 CenterZ=0 NormalX=0 NormalY=0 NormalZ=1 AngleXU=0 Radius=2.75
    g6: Circle CenterX=19 CenterY=42 CenterZ=0 NormalX=0 NormalY=0 NormalZ=1 AngleXU=0 Radius=2.75
    g7: Circle CenterX=19 CenterY=12 CenterZ=0 NormalX=0 NormalY=0 NormalZ=1 AngleXU=0 Radius=2.75
  constraints (20):
    c: Equal(g0,g2)
    c: Equal(g2,g1)
    c: Equal(g1,g3)
    c: Equal(g3,g4)
    c: Equal(g4,g6)
    c: Equal(g6,g7)
    c: Equal(g7,g5)
    c: Symmetric(g0,g2,g-2)
    c: Symmetric(g1,g3,g-2)
    c: Symmetric(g4,g6,g-2)
    c: Symmetric(g5,g7,g-2)
    c: DistanceY(g3,g2) = 30
    c: DistanceX(g0,g2) = 38
    c: DistanceX(g1,g3) = 38
    c: DistanceX(g4,g6) = 38
    c: DistanceX(g5,g7) = 38
    c: DistanceY(g7,g6) = 30
    c: Diameter(g2) = 5.5
    c: DistanceY(g-1,g7) = 12
    c: DistanceY(g2,g-3) = 12
FEATURE [PartDesign::Pocket] Pocket
  BaseFeature = -> Pad
  Length = 3
  Length2 = 100
  Placement = pos=(0,0,0) rot=(1,0,0;1.5708rad)
  Profile = -> Sketch001
  Type = 0
FEATURE [PartDesign::CoordinateSystem] LCS_h1
  AttacherType = Attacher::AttachEngine3D
  MapMode = 11
  Placement = pos=(-19,-108,-30) rot=(0.707107,-0.707107,0;3.14159rad)
  Support = -> [Pocket]
FEATURE [PartDesign::CoordinateSystem] LCS_h2
  AttacherType = Attacher::AttachEngine3D
  MapMode = 11
  Placement = pos=(19,-108,-30) rot=(0.707107,-0.707107,0;3.14159rad)
  Support = -> [Pocket]
FEATURE [PartDesign::CoordinateSystem] LCS_h3
  AttacherType = Attacher::AttachEngine3D
  MapMode = 11
  Placement = pos=(-19,-78,-30) rot=(0.707107,-0.707107,0;3.14159rad)
  Support = -> [Pocket]
FEATURE [PartDesign::CoordinateSystem] LCS_h4
  AttacherType = Attacher::AttachEngine3D
  MapMode = 11
  Placement = pos=(19,-78,-30) rot=(0.707107,-0.707107,0;3.14159rad)
  Support = -> [Pocket]
FEATURE [PartDesign::CoordinateSystem] LCS_h5
  AttacherType = Attacher::AttachEngine3D
  MapMode = 11
  Placement = pos=(-19,-42,-30) rot=(0.707107,-0.707107,0;3.14159rad)
  Support = -> [Pocket]
FEATURE [PartDesign::CoordinateSystem] LCS_h6
  AttacherType = Attacher::AttachEngine3D
  MapMode = 11
  Placement = pos=(19,-42,-30) rot=(0.707107,-0.707107,0;3.14159rad)
  Support = -> [Pocket]
FEATURE [PartDesign::CoordinateSystem] LCS_h7
  AttacherType = Attacher::AttachEngine3D
  MapMode = 11
  Placement = pos=(-19,-12,-30) rot=(0.707107,-0.707107,0;3.14159rad)
  Support = -> [Pocket]
FEATURE [PartDesign::CoordinateSystem] LCS_h8
  AttacherType = Attacher::AttachEngine3D
  MapMode = 11
  Placement = pos=(19,-12,-30) rot=(0.707107,-0.707107,0;3.14159rad)
  Support = -> [Pocket]
FEATURE [Sketcher::SketchObject] Sketch002
  FullyConstrained = true
  MapMode = 5
  Placement = pos=(0,0,30) rot=(0,0,1;3.14159rad)
  Support = -> [Pocket]
  sketch-geometry (4):
    g0: Circle CenterX=-20 CenterY=46 CenterZ=0 NormalX=0 NormalY=0 NormalZ=1 AngleXU=0 Radius=2.75
    g1: Circle CenterX=-20 CenterY=22 CenterZ=0 NormalX=0 NormalY=0 NormalZ=1 AngleXU=0 Radius=2.75
    g2: Circle CenterX=20 CenterY=46 CenterZ=0 NormalX=0 NormalY=0 NormalZ=1 AngleXU=0 Radius=2.75
    g3: Circle CenterX=20 CenterY=22 CenterZ=0 NormalX=0 NormalY=0 NormalZ=1 AngleXU=0 Radius=2.75
  constraints (10):
    c: DistanceY(g-1,g1) = 22
    c: Equal(g1,g3)
    c: Equal(g3,g2)
    c: Equal(g2,g0)
    c: Diameter(g3) = 5.5
    c: Symmetric(g3,g1,g-2)
    c: Symmetric(g2,g0,g-2)
    c: DistanceY(g3,g2) = 24
    c: DistanceX(g0,g2) = 40
    c: DistanceX(g1,g3) = 40
FEATURE [PartDesign::Pocket] Pocket001
  BaseFeature = -> Pocket
  Length = 3
  Length2 = 100
  Placement = pos=(0,0,0) rot=(1,0,0;1.5708rad)
  Profile = -> Sketch002
  Type = 0
FEATURE [PartDesign::CoordinateSystem] LCS_m1
  AttacherType = Attacher::AttachEngine3D
  MapMode = 11
  Placement = pos=(-20,-46,30) rot=(0,0,-1;1.5708rad)
  Support = -> [Pocket001]
FEATURE [PartDesign::CoordinateSystem] LCS_m2
  AttacherType = Attacher::AttachEngine3D
  MapMode = 11
  Placement = pos=(20,-46,30) rot=(0,0,-1;1.5708rad)
  Support = -> [Pocket001]
FEATURE [PartDesign::CoordinateSystem] LCS_m3
  AttacherType = Attacher::AttachEngine3D
  MapMode = 11
  Placement = pos=(-20,-22,30) rot=(0,0,-1;1.5708rad)
  Support = -> [Pocket001]
FEATURE [PartDesign::CoordinateSystem] LCS_m4
  AttacherType = Attacher::AttachEngine3D
  MapMode = 11
  Placement = pos=(20,-22,30) rot=(0,0,-1;1.5708rad)
  Support = -> [Pocket001]
FEATURE [Sketcher::SketchObject] Sketch003
  ExternalGeometry = -> [Pocket001]
  FullyConstrained = true
  MapMode = 5
  Placement = pos=(30,0,0) rot=(0.707107,0,0.707107;3.14159rad)
  Support = -> [Pocket001]
  sketch-geometry (4):
    g0: Circle CenterX=-20 CenterY=110 CenterZ=0 NormalX=0 NormalY=0 NormalZ=1 AngleXU=0 Radius=3
    g1: Circle CenterX=20 CenterY=110 CenterZ=0 NormalX=0 NormalY=0 NormalZ=1 AngleXU=0 Radius=3
    g2: Circle CenterX=-20 CenterY=70 CenterZ=0 NormalX=0 NormalY=0 NormalZ=1 AngleXU=0 Radius=3
    g3: Circle CenterX=20 CenterY=70 CenterZ=0 NormalX=0 NormalY=0 NormalZ=1 AngleXU=0 Radius=3
  constraints (10):
    c: Equal(g2,g3)
    c: Equal(g3,g1)
    c: Equal(g1,g0)
    c: Diameter(g1) = 6
    c: Symmetric(g2,g3,g-2)
    c: Symmetric(g1,g0,g-2)
    c: DistanceX(g0,g1) = 40
    c: DistanceX(g2,g3) = 40
    c: DistanceY(g2,g0) = 40
    c: DistanceY(g0,g-3) = 10
FEATURE [PartDesign::Pocket] Pocket002
  BaseFeature = -> Pocket001
  Length = 3
  Length2 = 100
  Placement = pos=(0,0,0) rot=(1,0,0;1.5708rad)
  Profile = -> Sketch003
  Type = 0
FEATURE [PartDesign::CoordinateSystem] LCS_ch1
  AttacherType = Attacher::AttachEngine3D
  MapMode = 11
  Placement = pos=(20,-22,27) rot=(0,0,-1;1.5708rad)
  Support = -> [Pocket002]
FEATURE [PartDesign::CoordinateSystem] LCS_ch2
  AttacherType = Attacher::AttachEngine3D
  MapMode = 11
  Placement = pos=(-20,-22,27) rot=(0,0,-1;1.5708rad)
  Support = -> [Pocket002]
FEATURE [PartDesign::CoordinateSystem] LCS_1
  AttacherType = Attacher::AttachEngine3D
  MapMode = 11
  Placement = pos=(30,-110,20) rot=(0.57735,-0.57735,0.57735;4.18879rad)
  Support = -> [Pocket002]
FEATURE [PartDesign::CoordinateSystem] LCS_2
  AttacherType = Attacher::AttachEngine3D
  MapMode = 11
  Placement = pos=(30,-70,20) rot=(0.57735,-0.57735,0.57735;4.18879rad)
  Support = -> [Pocket002]
FEATURE [PartDesign::CoordinateSystem] LCS_3
  AttacherType = Attacher::AttachEngine3D
  MapMode = 11
  Placement = pos=(30,-110,-20) rot=(0.57735,-0.57735,0.57735;4.18879rad)
  Support = -> [Pocket002]
FEATURE [PartDesign::CoordinateSystem] LCS_4
  AttacherType = Attacher::AttachEngine3D
  MapMode = 11
  Placement = pos=(30,-70,-20) rot=(0.57735,-0.57735,0.57735;4.18879rad)
  Support = -> [Pocket002]
FEATURE [PartDesign::Body] Body
  Group = -> [Sketch,Pad,Sketch001,Pocket,LCS_h1,LCS_h2,LCS_h3,LCS_h4,LCS_h5,LCS_h6,LCS_h7,LCS_h8,Sketch002,Pocket001,LCS_m1,LCS_m2,LCS_m3,LCS_m4,Sketch003,Pocket002,LCS_ch1,LCS_ch2,LCS_1,LCS_2,LCS_3,LCS_4]
  Origin = -> Origin
  Tip = -> Pocket002
---- part portal_tube.FCStd = doc fcstd_c3809f9868d1 ----
FCSTD DOCUMENT  (FreeCAD 0.19R)
Label: portal_tube
License: All rights reserved
LicenseURL: http://en.wikipedia.org/wiki/All_rights_reserved
objects: PartDesign::CoordinateSystem×7, Sketcher::SketchObject×2, PartDesign::Pad×1, PartDesign::Pocket×1, PartDesign::Body×1
note: 14 computed .brp shape members not serialized (recipe doc carries the construction recipe); baked Part::Feature solids carry a one-line shape summary decoded from their .brp

FEATURE [Sketcher::SketchObject] Sketch
  FullyConstrained = true
  MapMode = 5
  Placement = pos=(0,0,0) rot=(1,0,0;1.5708rad)
  Support = -> [XZ_Plane]
  sketch-geometry (8):
    g0: LineSegment StartX=-27 StartY=27 StartZ=0 EndX=27 EndY=27 EndZ=0
    g1: LineSegment StartX=27 StartY=27 StartZ=0 EndX=27 EndY=-27 EndZ=0
    g2: LineSegment StartX=27 StartY=-27 StartZ=0 EndX=-27 EndY=-27 EndZ=0
    g3: LineSegment StartX=-27 StartY=-27 StartZ=0 EndX=-27 EndY=27 EndZ=0
    g4: LineSegment StartX=-30 StartY=30 StartZ=0 EndX=30 EndY=30 EndZ=0
    g5: LineSegment StartX=30 StartY=30 StartZ=0 EndX=30 EndY=-30 EndZ=0
    g6: LineSegment StartX=30 StartY=-30 StartZ=0 EndX=-30 EndY=-30 EndZ=0
    g7: LineSegment StartX=-30 StartY=-30 StartZ=0 EndX=-30 EndY=30 EndZ=0
  constraints (22):
    c: Coincident(g0,g1)
    c: Coincident(g1,g2)
    c: Coincident(g2,g3)
    c: Coincident(g3,g0)
    c: Horizontal(g0)
    c: Horizontal(g2)
    c: Vertical(g1)
    c: Vertical(g3)
    c: Coincident(g4,g5)
    c: Coincident(g5,g6)
    c: Coincident(g6,g7)
    c: Coincident(g7,g4)
    c: Horizontal(g6)
    c: Vertical(g5)
    c: DistanceY(g7,g7) = 60
    c: DistanceX(g4,g4) = 60
    c: Symmetric(g4,g4,g-2)
    c: Symmetric(g6,g4,g-1)
    c: DistanceX(g0,g4) = 3
    c: DistanceY(g0,g4) = 3
    c: DistanceX(g6,g2) = 3
    c: DistanceY(g6,g2) = 3
FEATURE [PartDesign::Pad] Pad
  Direction = (1,1,1)
  Length = 921
  Length2 = 100
  Placement = pos=(0,0,0) rot=(1,0,0;1.5708rad)
  Profile = -> Sketch
  Type = 0
FEATURE [Sketcher::SketchObject] Sketch002
  ExternalGeometry = -> [Pad]
  FullyConstrained = true
  MapMode = 5
  Placement = pos=(30,0,0) rot=(0.707107,0,0.707107;3.14159rad)
  Support = -> [Pad]
  sketch-geometry (14):
    g0: Circle CenterX=-20 CenterY=50 CenterZ=0 NormalX=0 NormalY=0 NormalZ=1 AngleXU=0 Radius=2.75
    g1: Circle CenterX=20 CenterY=50 CenterZ=0 NormalX=0 NormalY=0 NormalZ=1 AngleXU=0 Radius=2.75
    g2: LineSegment StartX=-20 StartY=50 StartZ=0 EndX=20 EndY=50 EndZ=0
    g3: Circle CenterX=-20 CenterY=10 CenterZ=0 NormalX=0 NormalY=0 NormalZ=1 AngleXU=0 Radius=2.75
    g4: LineSegment StartX=-20 StartY=50 StartZ=0 EndX=-20 EndY=10 EndZ=0
    g5: Circle CenterX=20 CenterY=10 CenterZ=0 NormalX=0 NormalY=0 NormalZ=1 AngleXU=0 Radius=2.75
    g6: LineSegment StartX=-20 StartY=10 StartZ=0 EndX=20 EndY=10 EndZ=0
    g7: Circle CenterX=-20 CenterY=903 CenterZ=0 NormalX=0 NormalY=0 NormalZ=1 AngleXU=0 Radius=2.75
    g8: Circle CenterX=20 CenterY=903 CenterZ=0 NormalX=0 NormalY=0 NormalZ=1 AngleXU=0 Radius=2.75
    g9: LineSegment StartX=-20 StartY=903 StartZ=0 EndX=20 EndY=903 EndZ=0
    g10: Circle CenterX=-20 CenterY=863 CenterZ=0 NormalX=0 NormalY=0 NormalZ=1 AngleXU=0 Radius=2.75
    g11: LineSegment StartX=-20 StartY=903 StartZ=0 EndX=-20 EndY=863 EndZ=0
    g12: Circle CenterX=20 CenterY=863 CenterZ=0 NormalX=0 NormalY=0 NormalZ=1 AngleXU=0 Radius=2.75
    g13: LineSegment StartX=-20 StartY=863 StartZ=0 EndX=20 EndY=863 EndZ=0
  constraints (36):
    c: Coincident(g0,g2)
    c: Coincident(g1,g2)
    c: Distance(g2) = 40
    c: Angle(g2) = 0
    c: Coincident(g0,g4)
    c: Coincident(g3,g4)
    c: Distance(g4) = 40
    c: Perpendicular(g4,g2)
    c: Coincident(g3,g6)
    c: Coincident(g5,g6)
    c: Equal(g2,g6)
    c: Parallel(g6,g2)
    c: DistanceY(g-1,g3) = 10
    c: DistanceX(g3,g-1) = 20
    c: Equal(g5,g3)
    c: Equal(g3,g0)
    c: Equal(g0,g1)
    c: Diameter(g1) = 5.5
    c: Coincident(g7,g9)
    c: Coincident(g8,g9)
    c: Distance(g9) = 40
    c: Angle(g9) = 0
    c: Coincident(g7,g11)
    c: Coincident(g10,g11)
    c: Equal(g11,g9)
    c: Perpendicular(g11,g9)
    c: Coincident(g10,g13)
    c: Coincident(g12,g13)
    c: Equal(g9,g13)
    c: Parallel(g13,g9)
    c: Equal(g12,g10)
    c: Equal(g10,g7)
    c: Equal(g7,g8)
    c: Diameter(g8) = 5.5
    c: DistanceY(g8,g-3) = 18
    c: DistanceX(g8,g-3) = 10
FEATURE [PartDesign::Pocket] Pocket
  BaseFeature = -> Pad
  Length = 3
  Length2 = 100
  Placement = pos=(0,0,0) rot=(1,0,0;1.5708rad)
  Profile = -> Sketch002
  Type = 0
FEATURE [PartDesign::CoordinateSystem] LCS_top_rail
  AttacherType = Attacher::AttachEngine3D
  AttachmentOffset = pos=(0,160,0) rot=(0,0,1;0rad)
  MapMode = 5
  Placement = pos=(0,-160,30) rot=(0,0,1;3.14159rad)
  Support = -> [Pocket]
FEATURE [PartDesign::CoordinateSystem] LCS_bottom_RAIL
  AttacherType = Attacher::AttachEngine3D
  AttachmentOffset = pos=(0,160,0) rot=(0,0,1;0rad)
  MapMode = 5
  Placement = pos=(0,-160,-30) rot=(1,0,0;3.14159rad)
  Support = -> [Pocket]
FEATURE [PartDesign::CoordinateSystem] LCS_BF
  AttacherType = Attacher::AttachEngine3D
  AttachmentOffset = pos=(0,130,0) rot=(0,0,1;0rad)
  MapMode = 5
  Placement = pos=(0,-130,-30) rot=(1,0,0;3.14159rad)
  Support = -> [Pocket]
FEATURE [PartDesign::CoordinateSystem] LCS_1
  AttacherType = Attacher::AttachEngine3D
  MapMode = 11
  Placement = pos=(30,-903,20) rot=(0.57735,-0.57735,0.57735;4.18879rad)
  Support = -> [Pocket]
FEATURE [PartDesign::CoordinateSystem] LCS_2
  AttacherType = Attacher::AttachEngine3D
  MapMode = 11
  Placement = pos=(30,-863,20) rot=(0.57735,-0.57735,0.57735;4.18879rad)
  Support = -> [Pocket]
FEATURE [PartDesign::CoordinateSystem] LCS_3
  AttacherType = Attacher::AttachEngine3D
  MapMode = 11
  Placement = pos=(30,-50,20) rot=(0.57735,-0.57735,0.57735;4.18879rad)
  Support = -> [Pocket]
FEATURE [PartDesign::CoordinateSystem] LCS_4
  AttacherType = Attacher::AttachEngine3D
  MapMode = 11
  Placement = pos=(30,-10,20) rot=(0.57735,-0.57735,0.57735;4.18879rad)
  Support = -> [Pocket]
FEATURE [PartDesign::Body] Body
  Group = -> [Sketch,Pad,LCS_top_rail,LCS_bottom_RAIL,LCS_BF,Sketch002,Pocket,LCS_1,LCS_2,LCS_3,LCS_4]
  Origin = -> Origin
  Tip = -> Pocket
---- part sfu1605_500.FCStd = doc fcstd_2b3214d4bf6e ----
FCSTD DOCUMENT  (FreeCAD 0.19R)
Label: sfu1605_500
License: All rights reserved
LicenseURL: http://en.wikipedia.org/wiki/All_rights_reserved
objects: Sketcher::SketchObject×4, PartDesign::Pad×4, PartDesign::CoordinateSystem×3, PartDesign::Body×1
note: 16 computed .brp shape members not serialized (recipe doc carries the construction recipe); baked Part::Feature solids carry a one-line shape summary decoded from their .brp

FEATURE [Sketcher::SketchObject] Sketch
  FullyConstrained = true
  MapMode = 5
  Placement = pos=(0,0,0) rot=(1,0,0;1.5708rad)
  Support = -> [XZ_Plane]
  sketch-geometry (1):
    g0: Circle CenterX=0 CenterY=0 CenterZ=0 NormalX=0 NormalY=0 NormalZ=1 AngleXU=0 Radius=5
  constraints (2):
    c: Coincident(g0,g-1)
    c: Diameter(g0) = 10
FEATURE [PartDesign::Pad] Pad
  Direction = (1,1,1)
  Length = 15
  Length2 = 100
  Placement = pos=(0,0,0) rot=(1,0,0;1.5708rad)
  Profile = -> Sketch
  Reversed = true
  Type = 0
FEATURE [Sketcher::SketchObject] Sketch001
  FullyConstrained = true
  MapMode = 5
  Placement = pos=(0,15,-3.3e-15) rot=(-1,0,0;1.5708rad)
  Support = -> [Pad]
  sketch-geometry (1):
    g0: Circle CenterX=0 CenterY=0 CenterZ=0 NormalX=0 NormalY=0 NormalZ=1 AngleXU=0 Radius=6
  constraints (2):
    c: Coincident(g0,g-1)
    c: Diameter(g0) = 12
FEATURE [PartDesign::Pad] Pad001
  BaseFeature = -> Pad
  Direction = (1,1,1)
  Length = 39
  Length2 = 100
  Placement = pos=(0,0,0) rot=(1,0,0;1.5708rad)
  Profile = -> Sketch001
  Type = 0
FEATURE [Sketcher::SketchObject] Sketch002
  FullyConstrained = true
  MapMode = 5
  Placement = pos=(0,54,-3.67e-14) rot=(-1,0,0;1.5708rad)
  Support = -> [Pad001]
  sketch-geometry (1):
    g0: Circle CenterX=0 CenterY=0 CenterZ=0 NormalX=0 NormalY=0 NormalZ=1 AngleXU=0 Radius=8
  constraints (2):
    c: Coincident(g0,g-1)
    c: Diameter(g0) = 16
FEATURE [PartDesign::Pad] Pad002
  BaseFeature = -> Pad001
  Direction = (1,1,1)
  Length = 435
  Length2 = 100
  Placement = pos=(0,0,0) rot=(1,0,0;1.5708rad)
  Profile = -> Sketch002
  Type = 0
FEATURE [Sketcher::SketchObject] Sketch003
  FullyConstrained = true
  MapMode = 5
  Placement = pos=(0,489,-5.037e-13) rot=(-1,0,0;1.5708rad)
  Support = -> [Pad002]
  sketch-geometry (1):
    g0: Circle CenterX=0 CenterY=0 CenterZ=0 NormalX=0 NormalY=0 NormalZ=1 AngleXU=0 Radius=5
  constraints (2):
    c: Coincident(g0,g-1)
    c: Diameter(g0) = 10
FEATURE [PartDesign::Pad] Pad003
  BaseFeature = -> Pad002
  Direction = (1,1,1)
  Length = 11
  Length2 = 100
  Placement = pos=(0,0,0) rot=(1,0,0;1.5708rad)
  Profile = -> Sketch003
  Type = 0
FEATURE [PartDesign::CoordinateSystem] LCS_SLAVE_SIDE
  AttacherType = Attacher::AttachEngine3D
  MapMode = 11
  Placement = pos=(0,489,-5.56e-13) rot=(0.57735,-0.57735,-0.57735;4.18879rad)
  Support = -> [Pad003]
FEATURE [PartDesign::CoordinateSystem] LCS_BK_MOUNT
  AttacherType = Attacher::AttachEngine3D
  MapMode = 11
  Placement = pos=(0,54,-4.7e-14) rot=(0.57735,-0.57735,-0.57735;4.18879rad)
  Support = -> [Pad003]
FEATURE [PartDesign::CoordinateSystem] LCS_COUPLING
  AttacherType = Attacher::AttachEngine3D
  MapMode = 11
  Placement = pos=(0,0,0) rot=(0.57735,-0.57735,0.57735;2.0944rad)
  Support = -> [Pad003]
FEATURE [PartDesign::Body] Body
  Group = -> [Sketch,Pad,Sketch001,Pad001,Sketch002,Pad002,Sketch003,Pad003,LCS_SLAVE_SIDE,LCS_BK_MOUNT,LCS_COUPLING]
  Origin = -> Origin
  Tip = -> Pad003
---- part sfu1605_700.FCStd = doc fcstd_ec3d668a4b57 ----
FCSTD DOCUMENT  (FreeCAD 0.19R)
Label: sfu1605_700
License: All rights reserved
LicenseURL: http://en.wikipedia.org/wiki/All_rights_reserved
objects: Sketcher::SketchObject×4, PartDesign::Pad×4, PartDesign::CoordinateSystem×3, PartDesign::Body×1
note: 16 computed .brp shape members not serialized (recipe doc carries the construction recipe); baked Part::Feature solids carry a one-line shape summary decoded from their .brp

FEATURE [Sketcher::SketchObject] Sketch
  FullyConstrained = true
  MapMode = 5
  Placement = pos=(0,0,0) rot=(1,0,0;1.5708rad)
  Support = -> [XZ_Plane]
  sketch-geometry (1):
    g0: Circle CenterX=0 CenterY=0 CenterZ=0 NormalX=0 NormalY=0 NormalZ=1 AngleXU=0 Radius=5
  constraints (2):
    c: Coincident(g0,g-1)
    c: Diameter(g0) = 10
FEATURE [PartDesign::Pad] Pad
  Direction = (1,1,1)
  Length = 15
  Length2 = 100
  Placement = pos=(0,0,0) rot=(1,0,0;1.5708rad)
  Profile = -> Sketch
  Reversed = true
  Type = 0
FEATURE [Sketcher::SketchObject] Sketch001
  FullyConstrained = true
  MapMode = 5
  Placement = pos=(0,15,-3.3e-15) rot=(-1,0,0;1.5708rad)
  Support = -> [Pad]
  sketch-geometry (1):
    g0: Circle CenterX=0 CenterY=0 CenterZ=0 NormalX=0 NormalY=0 NormalZ=1 AngleXU=0 Radius=6
  constraints (2):
    c: Coincident(g0,g-1)
    c: Diameter(g0) = 12
FEATURE [PartDesign::Pad] Pad001
  BaseFeature = -> Pad
  Direction = (1,1,1)
  Length = 39
  Length2 = 100
  Placement = pos=(0,0,0) rot=(1,0,0;1.5708rad)
  Profile = -> Sketch001
  Type = 0
FEATURE [Sketcher::SketchObject] Sketch002
  FullyConstrained = true
  MapMode = 5
  Placement = pos=(0,54,-3.67e-14) rot=(-1,0,0;1.5708rad)
  Support = -> [Pad001]
  sketch-geometry (1):
    g0: Circle CenterX=0 CenterY=0 CenterZ=0 NormalX=0 NormalY=0 NormalZ=1 AngleXU=0 Radius=8
  constraints (2):
    c: Coincident(g0,g-1)
    c: Diameter(g0) = 16
FEATURE [PartDesign::Pad] Pad002
  BaseFeature = -> Pad001
  Direction = (1,1,1)
  Length = 635
  Length2 = 100
  Placement = pos=(0,0,0) rot=(1,0,0;1.5708rad)
  Profile = -> Sketch002
  Type = 0
FEATURE [Sketcher::SketchObject] Sketch003
  FullyConstrained = true
  MapMode = 5
  Placement = pos=(0,689,-7.097e-13) rot=(-1,0,0;1.5708rad)
  Support = -> [Pad002]
  sketch-geometry (1):
    g0: Circle CenterX=0 CenterY=0 CenterZ=0 NormalX=0 NormalY=0 NormalZ=1 AngleXU=0 Radius=5
  constraints (2):
    c: Coincident(g0,g-1)
    c: Diameter(g0) = 10
FEATURE [PartDesign::Pad] Pad003
  BaseFeature = -> Pad002
  Direction = (1,1,1)
  Length = 11
  Length2 = 100
  Placement = pos=(0,0,0) rot=(1,0,0;1.5708rad)
  Profile = -> Sketch003
  Type = 0
FEATURE [PartDesign::CoordinateSystem] LCS_m1
  AttacherType = Attacher::AttachEngine3D
  MapMode = 11
  Placement = pos=(0,689,-1.013e-12) rot=(0.57735,-0.57735,-0.57735;4.18879rad)
  Support = -> [Pad003]
FEATURE [PartDesign::CoordinateSystem] LCS_m2
  AttacherType = Attacher::AttachEngine3D
  MapMode = 11
  Placement = pos=(0,54,-4.7e-14) rot=(0.57735,-0.57735,-0.57735;4.18879rad)
  Support = -> [Pad003]
FEATURE [PartDesign::CoordinateSystem] LCS_m3
  AttacherType = Attacher::AttachEngine3D
  MapMode = 11
  Placement = pos=(0,0,0) rot=(0.57735,-0.57735,0.57735;2.0944rad)
  Support = -> [Pad003]
FEATURE [PartDesign::Body] Body
  Group = -> [Sketch,Pad,Sketch001,Pad001,Sketch002,Pad002,Sketch003,Pad003,LCS_m1,LCS_m2,LCS_m3]
  Origin = -> Origin
  Tip = -> Pad003
---- part spacer.FCStd = doc fcstd_b3e4c191ed72 ----
FCSTD DOCUMENT  (FreeCAD 0.19R)
Label: spacer
License: All rights reserved
LicenseURL: http://en.wikipedia.org/wiki/All_rights_reserved
objects: PartDesign::CoordinateSystem×6, Sketcher::SketchObject×3, PartDesign::Pocket×2, PartDesign::Pad×1, PartDesign::Body×1
note: 16 computed .brp shape members not serialized (recipe doc carries the construction recipe); baked Part::Feature solids carry a one-line shape summary decoded from their .brp

FEATURE [Sketcher::SketchObject] Sketch
  FullyConstrained = true
  MapMode = 5
  Support = -> [XY_Plane]
  sketch-geometry (8):
    g0: LineSegment StartX=-30 StartY=30 StartZ=0 EndX=30 EndY=30 EndZ=0
    g1: LineSegment StartX=30 StartY=30 StartZ=0 EndX=30 EndY=-30 EndZ=0
    g2: LineSegment StartX=30 StartY=-30 StartZ=0 EndX=-30 EndY=-30 EndZ=0
    g3: LineSegment StartX=-30 StartY=-30 StartZ=0 EndX=-30 EndY=30 EndZ=0
    g4: LineSegment StartX=-27 StartY=27 StartZ=0 EndX=27 EndY=27 EndZ=0
    g5: LineSegment StartX=27 StartY=27 StartZ=0 EndX=27 EndY=-27 EndZ=0
    g6: LineSegment StartX=27 StartY=-27 StartZ=0 EndX=-27 EndY=-27 EndZ=0
    g7: LineSegment StartX=-27 StartY=-27 StartZ=0 EndX=-27 EndY=27 EndZ=0
  constraints (22):
    c: Coincident(g0,g1)
    c: Coincident(g1,g2)
    c: Coincident(g2,g3)
    c: Coincident(g3,g0)
    c: Horizontal(g0)
    c: Vertical(g1)
    c: Coincident(g4,g5)
    c: Coincident(g5,g6)
    c: Coincident(g6,g7)
    c: Coincident(g7,g4)
    c: Horizontal(g4)
    c: Horizontal(g6)
    c: Vertical(g5)
    c: Vertical(g7)
    c: DistanceX(g0,g0) = 60
    c: DistanceY(g1,g1) = 60
    c: DistanceY(g1,g5) = 3
    c: DistanceX(g5,g1) = 3
    c: DistanceX(g0,g4) = 3
    c: DistanceY(g4,g0) = 3
    c: Symmetric(g2,g1,g-2)
    c: Symmetric(g0,g2,g-1)
FEATURE [PartDesign::Pad] Pad
  Direction = (1,1,1)
  Length = 140
  Length2 = 100
  Profile = -> Sketch
  Type = 0
FEATURE [Sketcher::SketchObject] Sketch001
  FullyConstrained = true
  MapMode = 5
  Placement = pos=(30,0,0) rot=(0.57735,0.57735,0.57735;2.0944rad)
  Support = -> [Pad]
  sketch-geometry (15):
    g0: Circle CenterX=-20 CenterY=130 CenterZ=0 NormalX=0 NormalY=0 NormalZ=1 AngleXU=0 Radius=2.75
    g1: Circle CenterX=20 CenterY=130 CenterZ=0 NormalX=0 NormalY=0 NormalZ=1 AngleXU=0 Radius=2.75
    g2: LineSegment StartX=-20 StartY=130 StartZ=0 EndX=20 EndY=130 EndZ=0
    g3: Circle CenterX=-20 CenterY=90 CenterZ=0 NormalX=0 NormalY=0 NormalZ=1 AngleXU=0 Radius=2.75
    g4: LineSegment StartX=-20 StartY=130 StartZ=0 EndX=-20 EndY=90 EndZ=0
    g5: Circle CenterX=20 CenterY=90 CenterZ=0 NormalX=0 NormalY=0 NormalZ=1 AngleXU=0 Radius=2.75
    g6: LineSegment StartX=-20 StartY=90 StartZ=0 EndX=20 EndY=90 EndZ=0
    g7: Circle CenterX=-20 CenterY=50 CenterZ=0 NormalX=0 NormalY=0 NormalZ=1 AngleXU=0 Radius=2.75
    g8: LineSegment StartX=-20 StartY=90 StartZ=0 EndX=-20 EndY=50 EndZ=0
    g9: Circle CenterX=20 CenterY=50 CenterZ=0 NormalX=0 NormalY=0 NormalZ=1 AngleXU=0 Radius=2.75
    g10: LineSegment StartX=-20 StartY=50 StartZ=0 EndX=20 EndY=50 EndZ=0
    g11: Circle CenterX=-20 CenterY=10 CenterZ=0 NormalX=0 NormalY=0 NormalZ=1 AngleXU=0 Radius=2.75
    g12: LineSegment StartX=-20 StartY=50 StartZ=0 EndX=-20 EndY=10 EndZ=0
    g13: Circle CenterX=20 CenterY=10 CenterZ=0 NormalX=0 NormalY=0 NormalZ=1 AngleXU=0 Radius=2.75
    g14: LineSegment StartX=-20 StartY=10 StartZ=0 EndX=20 EndY=10 EndZ=0
  constraints (38):
    c: Coincident(g0,g2)
    c: Coincident(g1,g2)
    c: Distance(g2) = 40
    c: Angle(g2) = 0
    c: Coincident(g0,g4)
    c: Coincident(g3,g4)
    c: Equal(g4,g2)
    c: Perpendicular(g4,g2)
    c: Coincident(g3,g6)
    c: Coincident(g5,g6)
    c: Equal(g2,g6)
    c: Parallel(g6,g2)
    c: Coincident(g3,g8)
    c: Coincident(g7,g8)
    c: Equal(g4,g8)
    c: Perpendicular(g8,g2)
    c: Coincident(g7,g10)
    c: Coincident(g9,g10)
    c: Equal(g2,g10)
    c: Parallel(g10,g2)
    c: Coincident(g7,g12)
    c: Coincident(g11,g12)
    c: Equal(g4,g12)
    c: Perpendicular(g12,g2)
    c: Coincident(g11,g14)
    c: Coincident(g13,g14)
    c: Equal(g2,g14)
    c: Parallel(g14,g2)
    c: DistanceX(g11,g-1) = 20
    c: DistanceY(g-1,g11) = 10
    c: Diameter(g0) = 5.5
    c: Equal(g0,g1)
    c: Equal(g1,g3)
    c: Equal(g3,g5)
    c: Equal(g5,g11)
    c: Equal(g11,g7)
    c: Equal(g7,g9)
    c: Equal(g9,g13)
FEATURE [PartDesign::Pocket] Pocket
  BaseFeature = -> Pad
  Length = 3
  Length2 = 100
  Profile = -> Sketch001
  Type = 0
FEATURE [Sketcher::SketchObject] Sketch002
  ExternalGeometry = -> [Pocket]
  FullyConstrained = true
  MapMode = 5
  Placement = pos=(-30,0,0) rot=(0.57735,-0.57735,-0.57735;2.0944rad)
  Support = -> [Pocket]
  sketch-geometry (7):
    g0: Circle CenterX=-20 CenterY=130 CenterZ=0 NormalX=0 NormalY=0 NormalZ=1 AngleXU=0 Radius=2.75
    g1: Circle CenterX=20 CenterY=130 CenterZ=0 NormalX=0 NormalY=0 NormalZ=1 AngleXU=0 Radius=2.75
    g2: LineSegment StartX=-20 StartY=130 StartZ=0 EndX=20 EndY=130 EndZ=0
    g3: Circle CenterX=-20 CenterY=90 CenterZ=0 NormalX=0 NormalY=0 NormalZ=1 AngleXU=0 Radius=2.75
    g4: LineSegment StartX=-20 StartY=130 StartZ=0 EndX=-20 EndY=90 EndZ=0
    g5: Circle CenterX=20 CenterY=90 CenterZ=0 NormalX=0 NormalY=0 NormalZ=1 AngleXU=0 Radius=2.75
    g6: LineSegment StartX=-20 StartY=90 StartZ=0 EndX=20 EndY=90 EndZ=0
  constraints (18):
    c: Diameter(g0) = 5.5
    c: Diameter(g1) = 5.5
    c: Coincident(g0,g2)
    c: Coincident(g1,g2)
    c: Distance(g2) = 40
    c: Angle(g2) = -3.97568e-07
    c: Diameter(g3) = 5.5
    c: Coincident(g0,g4)
    c: Coincident(g3,g4)
    c: Equal(g4,g2)
    c: Perpendicular(g4,g2)
    c: Diameter(g5) = 5.5
    c: Coincident(g3,g6)
    c: Coincident(g5,g6)
    c: Equal(g2,g6)
    c: Parallel(g6,g2)
    c: DistanceX(g-3,g0) = 10
    c: DistanceY(g0,g-3) = 10
FEATURE [PartDesign::Pocket] Pocket001
  BaseFeature = -> Pocket
  Length = 3
  Length2 = 100
  Profile = -> Sketch002
  Type = 0
FEATURE [PartDesign::CoordinateSystem] LCS_1
  AttacherType = Attacher::AttachEngine3D
  MapMode = 11
  Placement = pos=(30,-20,130) rot=(0.707107,0,0.707107;3.14159rad)
  Support = -> [Pocket001]
FEATURE [PartDesign::CoordinateSystem] LCS_2
  AttacherType = Attacher::AttachEngine3D
  MapMode = 11
  Placement = pos=(30,20,130) rot=(0.707107,0,0.707107;3.14159rad)
  Support = -> [Pocket001]
FEATURE [PartDesign::CoordinateSystem] LCS_3
  AttacherType = Attacher::AttachEngine3D
  MapMode = 11
  Placement = pos=(-30,-20,130) rot=(0,-1,0;1.5708rad)
  Support = -> [Pocket001]
FEATURE [PartDesign::CoordinateSystem] LCS_4
  AttacherType = Attacher::AttachEngine3D
  MapMode = 11
  Placement = pos=(-30,20,130) rot=(0,-1,0;1.5708rad)
  Support = -> [Pocket001]
FEATURE [PartDesign::CoordinateSystem] LCS_5
  AttacherType = Attacher::AttachEngine3D
  MapMode = 11
  Placement = pos=(-30,-20,90) rot=(0,-1,0;1.5708rad)
  Support = -> [Pocket001]
FEATURE [PartDesign::CoordinateSystem] LCS_6
  AttacherType = Attacher::AttachEngine3D
  MapMode = 11
  Placement = pos=(-30,20,90) rot=(0,-1,0;1.5708rad)
  Support = -> [Pocket001]
FEATURE [PartDesign::Body] Body
  Group = -> [Sketch,Pad,Sketch001,Pocket,Sketch002,Pocket001,LCS_1,LCS_2,LCS_3,LCS_4,LCS_5,LCS_6]
  Origin = -> Origin
  Tip = -> Pocket001
---- part spindle.FCStd = doc fcstd_7dd9ab4c4f55 ----
FCSTD DOCUMENT  (FreeCAD 0.19R)
Label: spindle
License: All rights reserved
LicenseURL: http://en.wikipedia.org/wiki/All_rights_reserved
objects: Sketcher::SketchObject×6, PartDesign::Pad×6, PartDesign::CoordinateSystem×1, PartDesign::Body×1
note: 20 computed .brp shape members not serialized (recipe doc carries the construction recipe); baked Part::Feature solids carry a one-line shape summary decoded from their .brp

FEATURE [Sketcher::SketchObject] Sketch
  FullyConstrained = true
  MapMode = 5
  Support = -> [XY_Plane]
  sketch-geometry (1):
    g0: Circle CenterX=0 CenterY=0 CenterZ=0 NormalX=0 NormalY=0 NormalZ=1 AngleXU=0 Radius=26
  constraints (2):
    c: Coincident(g0,g-1)
    c: Diameter(g0) = 52
FEATURE [PartDesign::Pad] Pad
  Direction = (1,1,1)
  Length = 120
  Length2 = 100
  Profile = -> Sketch
  Type = 0
FEATURE [Sketcher::SketchObject] Sketch001
  FullyConstrained = true
  MapMode = 5
  Placement = pos=(0,0,120) rot=(0,0,1;0rad)
  Support = -> [Pad]
  sketch-geometry (1):
    g0: Circle CenterX=0 CenterY=0 CenterZ=0 NormalX=0 NormalY=0 NormalZ=1 AngleXU=0 Radius=8
  constraints (2):
    c: Coincident(g0,g-1)
    c: Diameter(g0) = 16
FEATURE [PartDesign::Pad] Pad001
  BaseFeature = -> Pad
  Direction = (1,1,1)
  Length = 5
  Length2 = 100
  Profile = -> Sketch001
  Type = 0
FEATURE [Sketcher::SketchObject] Sketch002
  FullyConstrained = true
  MapMode = 5
  Placement = pos=(0,0,125) rot=(0,0,1;0rad)
  Support = -> [Pad001]
  sketch-geometry (1):
    g0: Circle CenterX=0 CenterY=0 CenterZ=0 NormalX=0 NormalY=0 NormalZ=1 AngleXU=0 Radius=28.5
  constraints (2):
    c: Coincident(g0,g-1)
    c: Diameter(g0) = 57
FEATURE [PartDesign::Pad] Pad002
  BaseFeature = -> Pad001
  Direction = (1,1,1)
  Length = 25
  Length2 = 100
  Profile = -> Sketch002
  Type = 0
FEATURE [Sketcher::SketchObject] Sketch003
  FullyConstrained = true
  MapMode = 5
  Placement = pos=(0,0,0) rot=(1,0,0;3.14159rad)
  Support = -> [Pad002]
  sketch-geometry (1):
    g0: Circle CenterX=0 CenterY=0 CenterZ=0 NormalX=0 NormalY=0 NormalZ=1 AngleXU=0 Radius=13
  constraints (2):
    c: Coincident(g0,g-1)
    c: Diameter(g0) = 26
FEATURE [PartDesign::Pad] Pad003
  BaseFeature = -> Pad002
  Direction = (1,1,1)
  Length = 6
  Length2 = 100
  Profile = -> Sketch003
  Type = 0
FEATURE [Sketcher::SketchObject] Sketch004
  FullyConstrained = true
  MapMode = 5
  Placement = pos=(0,0,-6) rot=(1,0,0;3.14159rad)
  Support = -> [Pad003]
  sketch-geometry (1):
    g0: Circle CenterX=0 CenterY=0 CenterZ=0 NormalX=0 NormalY=0 NormalZ=1 AngleXU=0 Radius=8
  constraints (2):
    c: Coincident(g0,g-1)
    c: Diameter(g0) = 16
FEATURE [PartDesign::Pad] Pad004
  BaseFeature = -> Pad003
  Direction = (1,1,1)
  Length = 28
  Length2 = 100
  Profile = -> Sketch004
  Type = 0
FEATURE [Sketcher::SketchObject] Sketch005
  FullyConstrained = true
  MapMode = 5
  Placement = pos=(0,0,-34) rot=(1,0,0;3.14159rad)
  Support = -> [Pad004]
  sketch-geometry (1):
    g0: Circle CenterX=0 CenterY=0 CenterZ=0 NormalX=0 NormalY=0 NormalZ=1 AngleXU=0 Radius=9.5
  constraints (2):
    c: Coincident(g0,g-1)
    c: Diameter(g0) = 19
FEATURE [PartDesign::Pad] Pad005
  BaseFeature = -> Pad004
  Direction = (1,1,1)
  Length = 12
  Length2 = 100
  Profile = -> Sketch005
  Type = 0
FEATURE [PartDesign::CoordinateSystem] LCS_mount
  AttacherType = Attacher::AttachEngine3D
  AttachmentOffset = pos=(0,0,-8) rot=(0,0,1;0rad)
  MapMode = 11
  Placement = pos=(0,0,112) rot=(0,0,1;1.5708rad)
  Support = -> [Pad005]
FEATURE [PartDesign::Body] Body
  Group = -> [Sketch,Pad,Sketch001,Pad001,Sketch002,Pad002,Sketch003,Pad003,Sketch004,Pad004,Sketch005,Pad005,LCS_mount]
  Origin = -> Origin
  Tip = -> Pad005
---- part spindle_holder.FCStd = doc fcstd_80ee83ccd882 ----
FCSTD DOCUMENT  (FreeCAD 0.19R)
Label: spindle_holder
License: All rights reserved
LicenseURL: http://en.wikipedia.org/wiki/All_rights_reserved
objects: PartDesign::CoordinateSystem×4, Sketcher::SketchObject×2, PartDesign::Pad×1, PartDesign::Pocket×1, PartDesign::Body×1
note: 11 computed .brp shape members not serialized (recipe doc carries the construction recipe); baked Part::Feature solids carry a one-line shape summary decoded from their .brp

FEATURE [Sketcher::SketchObject] Sketch
  FullyConstrained = true
  MapMode = 5
  Support = -> [XY_Plane]
  sketch-geometry (13):
    g0: LineSegment StartX=-45 StartY=0 StartZ=0 EndX=45 EndY=2e-16 EndZ=0
    g1: LineSegment StartX=-45 StartY=0 StartZ=0 EndX=-45 EndY=17 EndZ=0
    g2: LineSegment StartX=45 StartY=2e-16 StartZ=0 EndX=45 EndY=17 EndZ=0
    g3: LineSegment StartX=-45 StartY=17 StartZ=0 EndX=-42.5 EndY=22 EndZ=0
    g4: LineSegment StartX=45 StartY=17 StartZ=0 EndX=42.5 EndY=22 EndZ=0
    g5: LineSegment StartX=-42.5 StartY=22 StartZ=0 EndX=-42.5 EndY=54 EndZ=0
    g6: LineSegment StartX=42.5 StartY=22 StartZ=0 EndX=42.5 EndY=54 EndZ=0
    g7: LineSegment StartX=-42.5 StartY=54 StartZ=0 EndX=-27.5 EndY=54 EndZ=0
    g8: LineSegment StartX=-27.5 StartY=54 StartZ=0 EndX=-13.5 EndY=68 EndZ=0
    g9: LineSegment StartX=-13.5 StartY=68 StartZ=0 EndX=13.5 EndY=68 EndZ=0
    g10: LineSegment StartX=13.5 StartY=68 StartZ=0 EndX=27.5 EndY=54 EndZ=0
    g11: LineSegment StartX=27.5 StartY=54 StartZ=0 EndX=42.5 EndY=54 EndZ=0
    g12: Circle CenterX=0 CenterY=34 CenterZ=0 NormalX=0 NormalY=0 NormalZ=1 AngleXU=0 Radius=26
  constraints (35):
    c: PointOnObject(g0,g-1)
    c: Coincident(g1,g0)
    c: Coincident(g2,g0)
    c: Vertical(g2)
    c: Vertical(g1)
    c: Coincident(g3,g1)
    c: Coincident(g4,g2)
    c: Coincident(g5,g3)
    c: Vertical(g5)
    c: Coincident(g6,g4)
    c: Vertical(g6)
    c: Coincident(g7,g5)
    c: Horizontal(g7)
    c: Coincident(g8,g7)
    c: Coincident(g9,g8)
    c: Coincident(g10,g9)
    c: Coincident(g11,g10)
    c: Coincident(g6,g11)
    c: PointOnObject(g12,g-2)
    c: Diameter(g12) = 52
    c: DistanceY(g-1,g12) = 34
    c: DistanceX(g0,g0) = 90
    c: DistanceX(g5,g6) = 85
    c: Symmetric(g5,g6,g-2)
    c: Symmetric(g0,g0,g-2)
    c: DistanceX(g7,g10) = 55
    c: DistanceX(g9,g9) = 27
    c: Symmetric(g7,g10,g-2)
    c: Symmetric(g9,g8,g-2)
    c: DistanceY(g0,g5) = 54
    c: DistanceY(g0,g8) = 68
    c: Equal(g2,g1)
    c: DistanceY(g2,g2) = 17
    c: DistanceY(g6,g6) = 32
    c: Equal(g6,g5)
FEATURE [PartDesign::Pad] Pad
  Direction = (1,1,1)
  Length = 40
  Length2 = 100
  Profile = -> Sketch
  Type = 0
FEATURE [Sketcher::SketchObject] Sketch001
  FullyConstrained = true
  MapMode = 5
  Placement = pos=(0,0,0) rot=(1,0,0;1.5708rad)
  Support = -> [Pad]
  sketch-geometry (4):
    g0: Circle CenterX=-35 CenterY=30 CenterZ=0 NormalX=0 NormalY=0 NormalZ=1 AngleXU=0 Radius=3.25
    g1: Circle CenterX=-35 CenterY=10 CenterZ=0 NormalX=0 NormalY=0 NormalZ=1 AngleXU=0 Radius=3.25
    g2: Circle CenterX=35 CenterY=10 CenterZ=0 NormalX=0 NormalY=0 NormalZ=1 AngleXU=0 Radius=3.25
    g3: Circle CenterX=35 CenterY=30 CenterZ=0 NormalX=0 NormalY=0 NormalZ=1 AngleXU=0 Radius=3.25
  constraints (10):
    c: Symmetric(g3,g0,g-2)
    c: Symmetric(g2,g1,g-2)
    c: Equal(g3,g0)
    c: Equal(g0,g1)
    c: Diameter(g3) = 6.5
    c: Equal(g2,g1)
    c: DistanceX(g1,g2) = 70
    c: DistanceX(g0,g3) = 70
    c: DistanceY(g1,g0) = 20
    c: DistanceY(g-1,g1) = 10
FEATURE [PartDesign::Pocket] Pocket
  BaseFeature = -> Pad
  Length = 5
  Length2 = 100
  Profile = -> Sketch001
  Type = 1
FEATURE [PartDesign::CoordinateSystem] LCS_m1
  AttacherType = Attacher::AttachEngine3D
  MapMode = 11
  Placement = pos=(-35,0,30) rot=(0.57735,-0.57735,0.57735;2.0944rad)
  Support = -> [Pocket]
FEATURE [PartDesign::CoordinateSystem] LCS_h2
  AttacherType = Attacher::AttachEngine3D
  MapMode = 11
  Placement = pos=(35,0,30) rot=(0.57735,-0.57735,0.57735;2.0944rad)
  Support = -> [Pocket]
FEATURE [PartDesign::CoordinateSystem] LCS_motor_mount
  AttacherType = Attacher::AttachEngine3D
  MapMode = 11
  Placement = pos=(0,34,40) rot=(0,0,1;1.5708rad)
  Support = -> [Pocket]
FEATURE [PartDesign::CoordinateSystem] LCS_motor_mount1
  AttacherType = Attacher::AttachEngine3D
  MapMode = 11
  Placement = pos=(0,34,0) rot=(0,0,1;1.5708rad)
  Support = -> [Pocket]
FEATURE [PartDesign::Body] Body
  Group = -> [Sketch,Pad,Sketch001,Pocket,LCS_m1,LCS_h2,LCS_motor_mount,LCS_motor_mount1]
  Origin = -> Origin
  Tip = -> Pocket
---- part stpm_bracket.FCStd = doc fcstd_1201a4f63194 ----
FCSTD DOCUMENT  (FreeCAD 0.19R)
Label: stpm_bracket
License: All rights reserved
LicenseURL: http://en.wikipedia.org/wiki/All_rights_reserved
objects: Sketcher::SketchObject×3, PartDesign::Pocket×2, PartDesign::CoordinateSystem×2, PartDesign::Pad×1, PartDesign::Body×1
note: 12 computed .brp shape members not serialized (recipe doc carries the construction recipe); baked Part::Feature solids carry a one-line shape summary decoded from their .brp

FEATURE [Sketcher::SketchObject] Sketch
  FullyConstrained = true
  MapMode = 5
  Placement = pos=(0,0,0) rot=(1,0,0;1.5708rad)
  Support = -> [XZ_Plane]
  sketch-geometry (6):
    g0: LineSegment StartX=0 StartY=0 StartZ=0 EndX=0 EndY=68 EndZ=0
    g1: LineSegment StartX=0 StartY=68 StartZ=0 EndX=3 EndY=68 EndZ=0
    g2: LineSegment StartX=3 StartY=68 StartZ=0 EndX=3 EndY=3 EndZ=0
    g3: LineSegment StartX=3 StartY=3 StartZ=0 EndX=68 EndY=3 EndZ=0
    g4: LineSegment StartX=68 StartY=3 StartZ=0 EndX=68 EndY=0 EndZ=0
    g5: LineSegment StartX=68 StartY=0 StartZ=0 EndX=0 EndY=0 EndZ=0
  constraints (17):
    c: Coincident(g-1,g0)
    c: Vertical(g0)
    c: Coincident(g0,g1)
    c: Horizontal(g1)
    c: Coincident(g1,g2)
    c: Vertical(g2)
    c: Coincident(g2,g3)
    c: Horizontal(g3)
    c: Coincident(g3,g4)
    c: Vertical(g4)
    c: Coincident(g4,g5)
    c: Coincident(g5,g0)
    c: Horizontal(g5)
    c: DistanceY(g0,g0) = 68
    c: DistanceX(g5,g5) = 68
    c: DistanceY(g4,g3) = 3
    c: DistanceX(g0,g1) = 3
FEATURE [PartDesign::Pad] Pad
  Direction = (1,1,1)
  Length = 65
  Length2 = 100
  Placement = pos=(0,0,0) rot=(1,0,0;1.5708rad)
  Profile = -> Sketch
  Type = 0
FEATURE [Sketcher::SketchObject] Sketch001
  ExternalGeometry = -> [Pad]
  FullyConstrained = true
  MapMode = 5
  Placement = pos=(0,0,0) rot=(0.707107,0,-0.707107;3.14159rad)
  Support = -> [Pad]
  sketch-geometry (15):
    g0: Circle CenterX=-39 CenterY=32.5 CenterZ=0 NormalX=0 NormalY=0 NormalZ=1 AngleXU=0 Radius=19.05
    g1: Circle CenterX=-62.55 CenterY=56.05 CenterZ=0 NormalX=0 NormalY=0 NormalZ=1 AngleXU=0 Radius=2.5
    g2: Circle CenterX=-62.55 CenterY=8.95 CenterZ=0 NormalX=0 NormalY=0 NormalZ=1 AngleXU=0 Radius=2.5
    g3: Circle CenterX=-15.45 CenterY=8.95 CenterZ=0 NormalX=0 NormalY=0 NormalZ=1 AngleXU=0 Radius=2.5
    g4: LineSegment StartX=-62.55 StartY=56.05 StartZ=0 EndX=-15.45 EndY=56.05 EndZ=0
    g5: LineSegment StartX=-15.45 StartY=56.05 StartZ=0 EndX=-15.45 EndY=8.95 EndZ=0
    g6: LineSegment StartX=-15.45 StartY=8.95 StartZ=0 EndX=-62.55 EndY=8.95 EndZ=0
    g7: LineSegment StartX=-62.55 StartY=8.95 StartZ=0 EndX=-62.55 EndY=56.05 EndZ=0
    g8: Circle CenterX=-15.45 CenterY=56.05 CenterZ=0 NormalX=0 NormalY=0 NormalZ=1 AngleXU=0 Radius=2.5
    g9: LineSegment StartX=-62.55 StartY=0 StartZ=0 EndX=-68 EndY=-4.53e-14 EndZ=0
    g10: LineSegment StartX=-68 StartY=-4.53e-14 StartZ=0 EndX=-68 EndY=5.45 EndZ=0
    g11: LineSegment StartX=-68 StartY=5.45 StartZ=0 EndX=-62.55 EndY=0 EndZ=0
    g12: LineSegment StartX=-68 StartY=59.55 StartZ=0 EndX=-68 EndY=65 EndZ=0
    g13: LineSegment StartX=-68 StartY=65 StartZ=0 EndX=-62.55 EndY=65 EndZ=0
    g14: LineSegment StartX=-62.55 StartY=65 StartZ=0 EndX=-68 EndY=59.55 EndZ=0
  constraints (39):
    c: Equal(g1,g2)
    c: Diameter(g3) = 5
    c: Horizontal(g4)
    c: Horizontal(g6)
    c: Vertical(g5)
    c: Vertical(g7)
    c: DistanceX(g6,g6) = 47.1
    c: Diameter(g0) = 38.1
    c: Equal(g8,g1)
    c: Equal(g3,g8)
    c: Coincident(g7,g1)
    c: Coincident(g4,g1)
    c: Coincident(g7,g2)
    c: Coincident(g6,g2)
    c: Coincident(g3,g6)
    c: Coincident(g5,g3)
    c: Coincident(g8,g5)
    c: Coincident(g4,g8)
    c: Equal(g5,g6)
    c: DistanceY(g-1,g0) = 32.5
    c: DistanceX(g-3,g0) = 29
    c: DistanceX(g2,g0) = 23.55
    c: DistanceY(g3,g0) = 23.55
    c: PointOnObject(g9,g-1)
    c: Coincident(g9,g-3)
    c: Coincident(g9,g10)
    c: PointOnObject(g10,g-3)
    c: Coincident(g10,g11)
    c: Coincident(g11,g9)
    c: PointOnObject(g12,g-3)
    c: Coincident(g12,g-3)
    c: Coincident(g12,g13)
    c: Horizontal(g13)
    c: Coincident(g13,g14)
    c: Coincident(g14,g12)
    c: Equal(g12,g13)
    c: Equal(g13,g10)
    c: Equal(g10,g9)
    c: DistanceY(g10,g10) = 5.45
FEATURE [PartDesign::Pocket] Pocket
  BaseFeature = -> Pad
  Length = 3
  Length2 = 100
  Placement = pos=(0,0,0) rot=(1,0,0;1.5708rad)
  Profile = -> Sketch001
  Type = 0
FEATURE [Sketcher::SketchObject] Sketch002
  ExternalGeometry = -> [Pocket]
  FullyConstrained = true
  MapMode = 5
  Placement = pos=(0,0,0) rot=(1,0,0;3.14159rad)
  Support = -> [Pocket]
  sketch-geometry (14):
    g0: LineSegment StartX=62.55 StartY=65 StartZ=0 EndX=68 EndY=65 EndZ=0
    g1: LineSegment StartX=68 StartY=65 StartZ=0 EndX=68 EndY=59.55 EndZ=0
    g2: LineSegment StartX=68 StartY=59.55 StartZ=0 EndX=62.55 EndY=65 EndZ=0
    g3: LineSegment StartX=62.55 StartY=0 StartZ=0 EndX=68 EndY=0 EndZ=0
    g4: LineSegment StartX=68 StartY=0 StartZ=0 EndX=68 EndY=5.45 EndZ=0
    g5: LineSegment StartX=68 StartY=5.45 StartZ=0 EndX=62.55 EndY=0 EndZ=0
    g6: ArcOfCircle CenterX=16.15 CenterY=52.45 CenterZ=0 NormalX=0 NormalY=0 NormalZ=1 AngleXU=0 Radius=2.15 StartAngle=1.5708 EndAngle=4.71239
    g7: ArcOfCircle CenterX=57.85 CenterY=52.45 CenterZ=0 NormalX=0 NormalY=0 NormalZ=1 AngleXU=0 Radius=2.15 StartAngle=4.71239 EndAngle=7.85398
    g8: LineSegment StartX=16.15 StartY=50.3 StartZ=0 EndX=57.85 EndY=50.3 EndZ=0
    g9: LineSegment StartX=16.15 StartY=54.6 StartZ=0 EndX=57.85 EndY=54.6 EndZ=0
    g10: ArcOfCircle CenterX=16.15 CenterY=12.45 CenterZ=0 NormalX=0 NormalY=0 NormalZ=1 AngleXU=0 Radius=2.15 StartAngle=1.5708 EndAngle=4.71239
    g11: ArcOfCircle CenterX=57.85 CenterY=12.45 CenterZ=0 NormalX=0 NormalY=0 NormalZ=1 AngleXU=0 Radius=2.15 StartAngle=4.71239 EndAngle=7.85398
    g12: LineSegment StartX=16.15 StartY=10.3 StartZ=0 EndX=57.85 EndY=10.3 EndZ=0
    g13: LineSegment StartX=16.15 StartY=14.6 StartZ=0 EndX=57.85 EndY=14.6 EndZ=0
  constraints (36):
    c: PointOnObject(g0,g-4)
    c: Coincident(g0,g-4)
    c: Coincident(g0,g1)
    c: PointOnObject(g1,g-3)
    c: Coincident(g1,g2)
    c: Coincident(g2,g0)
    c: PointOnObject(g3,g-1)
    c: Coincident(g3,g-3)
    c: Coincident(g3,g4)
    c: PointOnObject(g4,g-3)
    c: Coincident(g4,g5)
    c: Coincident(g5,g3)
    c: Equal(g1,g0)
    c: Equal(g0,g4)
    c: Equal(g4,g3)
    c: DistanceY(g4,g4) = 5.45
    c: Tangent(g6,g9) = 1.5708
    c: Tangent(g6,g8) = -1.5708
    c: Tangent(g8,g7) = -1.5708
    c: Tangent(g9,g7) = 1.5708
    c: Horizontal(g8)
    c: Equal(g6,g7)
    c: Tangent(g10,g13) = 1.5708
    c: Tangent(g10,g12) = -1.5708
    c: Tangent(g12,g11) = -1.5708
    c: Tangent(g13,g11) = 1.5708
    c: Horizontal(g12)
    c: Equal(g10,g11)
    c: Equal(g13,g8)
    c: Equal(g11,g7)
    c: DistanceY(g6,g6) = 4.3
    c: DistanceY(g-1,g10) = 10.3
    c: DistanceY(g10,g6) = 35.7
    c: DistanceX(g6,g7) = 41.7
    c: DistanceX(g7,g0) = 10.15
    c: DistanceX(g11,g3) = 10.15
FEATURE [PartDesign::Pocket] Pocket001
  BaseFeature = -> Pocket
  Length = 3
  Length2 = 100
  Placement = pos=(0,0,0) rot=(1,0,0;1.5708rad)
  Profile = -> Sketch002
  Type = 0
FEATURE [PartDesign::CoordinateSystem] LCS_h1
  AttacherType = Attacher::AttachEngine3D
  MapMode = 11
  Placement = pos=(3,-56.05,62.55) rot=(0.57735,-0.57735,-0.57735;2.0944rad)
  Support = -> [Pocket001]
FEATURE [PartDesign::CoordinateSystem] LCS_h2
  AttacherType = Attacher::AttachEngine3D
  MapMode = 11
  Placement = pos=(3,-8.95,62.55) rot=(0.57735,-0.57735,-0.57735;2.0944rad)
  Support = -> [Pocket001]
FEATURE [PartDesign::Body] Body
  Group = -> [Sketch,Pad,Sketch001,Pocket,Sketch002,Pocket001,LCS_h1,LCS_h2]
  Origin = -> Origin
  Tip = -> Pocket001
---- part x_rail.FCStd = doc fcstd_8a7c126ee12f ----
FCSTD DOCUMENT  (FreeCAD 0.19R)
Label: x_rail
License: All rights reserved
LicenseURL: http://en.wikipedia.org/wiki/All_rights_reserved
objects: PartDesign::CoordinateSystem×2, Sketcher::SketchObject×1, PartDesign::Pad×1, PartDesign::Body×1
note: 6 computed .brp shape members not serialized (recipe doc carries the construction recipe); baked Part::Feature solids carry a one-line shape summary decoded from their .brp

FEATURE [Sketcher::SketchObject] Sketch
  FullyConstrained = true
  MapMode = 5
  Placement = pos=(0,0,0) rot=(1,0,0;1.5708rad)
  Support = -> [XZ_Plane]
  sketch-geometry (14):
    g0: LineSegment StartX=-7.5 StartY=0 StartZ=0 EndX=7.5 EndY=0 EndZ=0
    g1: LineSegment StartX=-7.5 StartY=0 StartZ=0 EndX=-7.5 EndY=2.7 EndZ=0
    g2: LineSegment StartX=7.5 StartY=0 StartZ=0 EndX=7.5 EndY=2.7 EndZ=0
    g3: LineSegment StartX=-7.5 StartY=2.7 StartZ=0 EndX=-5 EndY=5.2 EndZ=0
    g4: LineSegment StartX=-5 StartY=5.2 StartZ=0 EndX=-5 EndY=7.2 EndZ=0
    g5: LineSegment StartX=-5 StartY=7.2 StartZ=0 EndX=-7.5 EndY=9.7 EndZ=0
    g6: LineSegment StartX=-7.5 StartY=9.7 StartZ=0 EndX=-7.5 EndY=12.5 EndZ=0
    g7: LineSegment StartX=-7.5 StartY=12.5 StartZ=0 EndX=-5 EndY=15 EndZ=0
    g8: LineSegment StartX=-5 StartY=15 StartZ=0 EndX=5 EndY=15 EndZ=0
    g9: LineSegment StartX=5 StartY=15 StartZ=0 EndX=7.5 EndY=12.5 EndZ=0
    g10: LineSegment StartX=7.5 StartY=12.5 StartZ=0 EndX=7.5 EndY=9.7 EndZ=0
    g11: LineSegment StartX=7.5 StartY=9.7 StartZ=0 EndX=5 EndY=7.2 EndZ=0
    g12: LineSegment StartX=5 StartY=7.2 StartZ=0 EndX=5 EndY=5.2 EndZ=0
    g13: LineSegment StartX=7.5 StartY=2.7 StartZ=0 EndX=5 EndY=5.2 EndZ=0
  constraints (36):
    c: PointOnObject(g0,g-1)
    c: Coincident(g1,g0)
    c: Vertical(g1)
    c: Coincident(g2,g0)
    c: Vertical(g2)
    c: Coincident(g3,g1)
    c: Coincident(g4,g3)
    c: Vertical(g4)
    c: Coincident(g5,g4)
    c: Coincident(g6,g5)
    c: Coincident(g7,g6)
    c: Coincident(g8,g7)
    c: Coincident(g9,g8)
    c: Coincident(g10,g9)
    c: Coincident(g11,g10)
    c: Coincident(g12,g11)
    c: Coincident(g13,g2)
    c: Coincident(g13,g12)
    c: Symmetric(g0,g0,g-2)
    c: DistanceX(g0,g0) = 15
    c: DistanceY(g0,g8) = 15
    c: DistanceX(g8,g8) = 10
    c: Symmetric(g7,g8,g-2)
    c: Vertical(g6)
    c: Symmetric(g9,g6,g-2)
    c: Symmetric(g5,g10,g-2)
    c: Symmetric(g4,g11,g-2)
    c: Symmetric(g12,g3,g-2)
    c: DistanceX(g8,g9) = 2.5
    c: DistanceY(g9,g8) = 2.5
    c: DistanceY(g11,g10) = 2.5
    c: DistanceY(g13,g13) = 2.5
    c: DistanceY(g12,g12) = 2
    c: DistanceY(g10,g10) = 2.8
    c: DistanceX(g11,g11) = 2.5
    c: Equal(g2,g1)
FEATURE [PartDesign::Pad] Pad
  Direction = (1,1,1)
  Length = 400
  Length2 = 100
  Placement = pos=(0,0,0) rot=(1,0,0;1.5708rad)
  Profile = -> Sketch
  Type = 0
FEATURE [PartDesign::CoordinateSystem] LCS_mount
  AttacherType = Attacher::AttachEngine3D
  AttachmentOffset = pos=(0,30,0) rot=(0,0,1;0rad)
  MapMode = 5
  Placement = pos=(0,-30,1.32e-14) rot=(1,0,0;3.14159rad)
  Support = -> [Pad]
FEATURE [PartDesign::CoordinateSystem] LCS_CARET_MOUNT
  AttacherType = Attacher::AttachEngine3D
  AttachmentOffset = pos=(0,100,0) rot=(0,0,1;0rad)
  MapMode = 5
  Placement = pos=(0,-100,15) rot=(0,0,1;3.14159rad)
  Support = -> [Pad]
FEATURE [PartDesign::Body] Body
  Group = -> [Sketch,Pad,LCS_mount,LCS_CARET_MOUNT]
  Origin = -> Origin
  Tip = -> Pad
---- part x_tube.FCStd = doc fcstd_a42875da1418 ----
FCSTD DOCUMENT  (FreeCAD 0.19R)
Label: x_tube
License: All rights reserved
LicenseURL: http://en.wikipedia.org/wiki/All_rights_reserved
objects: PartDesign::CoordinateSystem×4, Sketcher::SketchObject×2, PartDesign::Pad×1, PartDesign::Pocket×1, PartDesign::Fillet×1, PartDesign::Body×1
note: 13 computed .brp shape members not serialized (recipe doc carries the construction recipe); baked Part::Feature solids carry a one-line shape summary decoded from their .brp

FEATURE [Sketcher::SketchObject] Sketch
  FullyConstrained = true
  MapMode = 5
  Placement = pos=(0,0,0) rot=(1,0,0;1.5708rad)
  Support = -> [XZ_Plane]
  sketch-geometry (8):
    g0: LineSegment StartX=-27 StartY=27 StartZ=0 EndX=27 EndY=27 EndZ=0
    g1: LineSegment StartX=27 StartY=27 StartZ=0 EndX=27 EndY=-27 EndZ=0
    g2: LineSegment StartX=27 StartY=-27 StartZ=0 EndX=-27 EndY=-27 EndZ=0
    g3: LineSegment StartX=-27 StartY=-27 StartZ=0 EndX=-27 EndY=27 EndZ=0
    g4: LineSegment StartX=-30 StartY=30 StartZ=0 EndX=30 EndY=30 EndZ=0
    g5: LineSegment StartX=30 StartY=30 StartZ=0 EndX=30 EndY=-30 EndZ=0
    g6: LineSegment StartX=30 StartY=-30 StartZ=0 EndX=-30 EndY=-30 EndZ=0
    g7: LineSegment StartX=-30 StartY=-30 StartZ=0 EndX=-30 EndY=30 EndZ=0
  constraints (22):
    c: Coincident(g0,g1)
    c: Coincident(g1,g2)
    c: Coincident(g2,g3)
    c: Coincident(g3,g0)
    c: Horizontal(g0)
    c: Horizontal(g2)
    c: Vertical(g1)
    c: Vertical(g3)
    c: Coincident(g4,g5)
    c: Coincident(g5,g6)
    c: Coincident(g6,g7)
    c: Coincident(g7,g4)
    c: Horizontal(g6)
    c: Vertical(g5)
    c: DistanceY(g7,g7) = 60
    c: DistanceX(g4,g4) = 60
    c: Symmetric(g4,g4,g-2)
    c: Symmetric(g6,g4,g-1)
    c: DistanceX(g0,g4) = 3
    c: DistanceY(g0,g4) = 3
    c: DistanceX(g6,g2) = 3
    c: DistanceY(g6,g2) = 3
FEATURE [PartDesign::Pad] Pad
  Direction = (1,1,1)
  Length = 610
  Length2 = 100
  Placement = pos=(0,0,0) rot=(1,0,0;1.5708rad)
  Profile = -> Sketch
  Type = 0
FEATURE [Sketcher::SketchObject] Sketch001
  ExternalGeometry = -> [Pad]
  FullyConstrained = true
  MapMode = 5
  Placement = pos=(0,0,30) rot=(0,0,1;3.14159rad)
  Support = -> [Pad]
  sketch-geometry (2):
    g0: Circle CenterX=0 CenterY=30 CenterZ=0 NormalX=0 NormalY=0 NormalZ=1 AngleXU=0 Radius=4.25
    g1: Circle CenterX=0 CenterY=580 CenterZ=0 NormalX=0 NormalY=0 NormalZ=1 AngleXU=0 Radius=4.25
  constraints (6):
    c: PointOnObject(g0,g-2)
    c: DistanceY(g-3,g0) = 30
    c: PointOnObject(g1,g-2)
    c: DistanceY(g1,g-4) = 30
    c: Equal(g1,g0)
    c: Diameter(g0) = 8.5
FEATURE [PartDesign::Pocket] Pocket
  BaseFeature = -> Pad
  Length = 3
  Length2 = 100
  Placement = pos=(0,0,0) rot=(1,0,0;1.5708rad)
  Profile = -> Sketch001
  Type = 0
FEATURE [PartDesign::CoordinateSystem] LCS_hole1
  AttacherType = Attacher::AttachEngine3D
  MapMode = 11
  Placement = pos=(0,-580,30) rot=(0,0,-1;1.5708rad)
  Support = -> [Pocket]
FEATURE [PartDesign::CoordinateSystem] LCS_hole2
  AttacherType = Attacher::AttachEngine3D
  MapMode = 11
  Placement = pos=(0,-30,30) rot=(0,0,-1;1.5708rad)
  Support = -> [Pocket]
FEATURE [PartDesign::CoordinateSystem] LCS_rail_mount
  AttacherType = Attacher::AttachEngine3D
  AttachmentOffset = pos=(0,70,0) rot=(0,0,1;0rad)
  MapMode = 5
  Placement = pos=(0,-70,-30) rot=(1,0,0;3.14159rad)
  Support = -> [Pocket]
FEATURE [PartDesign::CoordinateSystem] LCS_BF_MOUNT
  AttacherType = Attacher::AttachEngine3D
  AttachmentOffset = pos=(0,15,0) rot=(0,0,1;0rad)
  MapMode = 5
  Placement = pos=(0,-15,-30) rot=(1,0,0;3.14159rad)
  Support = -> [Pocket]
FEATURE [PartDesign::Fillet] Fillet
  Base = -> Pocket [Edge4,Edge22,Edge1,Edge7]
  BaseFeature = -> Pocket
  Placement = pos=(0,0,0) rot=(1,0,0;1.5708rad)
  Radius = 3
  SupportTransform = false
FEATURE [PartDesign::Body] Body
  Group = -> [Sketch,Pad,Sketch001,Pocket,LCS_hole1,LCS_hole2,LCS_rail_mount,LCS_BF_MOUNT,Fillet]
  Origin = -> Origin
  Tip = -> Fillet
---- part y_rail.FCStd = doc fcstd_a861a2b649ac ----
FCSTD DOCUMENT  (FreeCAD 0.19R)
Label: y_rail
License: All rights reserved
LicenseURL: http://en.wikipedia.org/wiki/All_rights_reserved
objects: PartDesign::CoordinateSystem×2, Sketcher::SketchObject×1, PartDesign::Pad×1, PartDesign::Body×1
note: 6 computed .brp shape members not serialized (recipe doc carries the construction recipe); baked Part::Feature solids carry a one-line shape summary decoded from their .brp

FEATURE [Sketcher::SketchObject] Sketch
  FullyConstrained = true
  MapMode = 5
  Placement = pos=(0,0,0) rot=(1,0,0;1.5708rad)
  Support = -> [XZ_Plane]
  sketch-geometry (14):
    g0: LineSegment StartX=-7.5 StartY=0 StartZ=0 EndX=7.5 EndY=0 EndZ=0
    g1: LineSegment StartX=-7.5 StartY=0 StartZ=0 EndX=-7.5 EndY=2.7 EndZ=0
    g2: LineSegment StartX=7.5 StartY=0 StartZ=0 EndX=7.5 EndY=2.7 EndZ=0
    g3: LineSegment StartX=-7.5 StartY=2.7 StartZ=0 EndX=-5 EndY=5.2 EndZ=0
    g4: LineSegment StartX=-5 StartY=5.2 StartZ=0 EndX=-5 EndY=7.2 EndZ=0
    g5: LineSegment StartX=-5 StartY=7.2 StartZ=0 EndX=-7.5 EndY=9.7 EndZ=0
    g6: LineSegment StartX=-7.5 StartY=9.7 StartZ=0 EndX=-7.5 EndY=12.5 EndZ=0
    g7: LineSegment StartX=-7.5 StartY=12.5 StartZ=0 EndX=-5 EndY=15 EndZ=0
    g8: LineSegment StartX=-5 StartY=15 StartZ=0 EndX=5 EndY=15 EndZ=0
    g9: LineSegment StartX=5 StartY=15 StartZ=0 EndX=7.5 EndY=12.5 EndZ=0
    g10: LineSegment StartX=7.5 StartY=12.5 StartZ=0 EndX=7.5 EndY=9.7 EndZ=0
    g11: LineSegment StartX=7.5 StartY=9.7 StartZ=0 EndX=5 EndY=7.2 EndZ=0
    g12: LineSegment StartX=5 StartY=7.2 StartZ=0 EndX=5 EndY=5.2 EndZ=0
    g13: LineSegment StartX=7.5 StartY=2.7 StartZ=0 EndX=5 EndY=5.2 EndZ=0
  constraints (36):
    c: PointOnObject(g0,g-1)
    c: Coincident(g1,g0)
    c: Vertical(g1)
    c: Coincident(g2,g0)
    c: Vertical(g2)
    c: Coincident(g3,g1)
    c: Coincident(g4,g3)
    c: Vertical(g4)
    c: Coincident(g5,g4)
    c: Coincident(g6,g5)
    c: Coincident(g7,g6)
    c: Coincident(g8,g7)
    c: Coincident(g9,g8)
    c: Coincident(g10,g9)
    c: Coincident(g11,g10)
    c: Coincident(g12,g11)
    c: Coincident(g13,g2)
    c: Coincident(g13,g12)
    c: Symmetric(g0,g0,g-2)
    c: DistanceX(g0,g0) = 15
    c: DistanceY(g0,g8) = 15
    c: DistanceX(g8,g8) = 10
    c: Symmetric(g7,g8,g-2)
    c: Vertical(g6)
    c: Symmetric(g9,g6,g-2)
    c: Symmetric(g5,g10,g-2)
    c: Symmetric(g4,g11,g-2)
    c: Symmetric(g12,g3,g-2)
    c: DistanceX(g8,g9) = 2.5
    c: DistanceY(g9,g8) = 2.5
    c: DistanceY(g11,g10) = 2.5
    c: DistanceY(g13,g13) = 2.5
    c: DistanceY(g12,g12) = 2
    c: DistanceY(g10,g10) = 2.8
    c: DistanceX(g11,g11) = 2.5
    c: Equal(g2,g1)
FEATURE [PartDesign::Pad] Pad
  Direction = (1,1,1)
  Length = 580
  Length2 = 100
  Placement = pos=(0,0,0) rot=(1,0,0;1.5708rad)
  Profile = -> Sketch
  Type = 0
FEATURE [PartDesign::CoordinateSystem] LCS_mount
  AttacherType = Attacher::AttachEngine3D
  MapMode = 5
  Placement = pos=(0,0,0) rot=(1,0,0;3.14159rad)
  Support = -> [Pad]
FEATURE [PartDesign::CoordinateSystem] LCS_caret_mount
  AttacherType = Attacher::AttachEngine3D
  AttachmentOffset = pos=(0,100,0) rot=(0,0,1;0rad)
  MapMode = 5
  Placement = pos=(0,-100,15) rot=(0,0,1;3.14159rad)
  Support = -> [Pad]
FEATURE [PartDesign::Body] Body
  Group = -> [Sketch,Pad,LCS_mount,LCS_caret_mount]
  Origin = -> Origin
  Tip = -> Pad
---- part y_tube.FCStd = doc fcstd_5cee01ceeb5b ----
FCSTD DOCUMENT  (FreeCAD 0.19R)
Label: y_tube
License: All rights reserved
LicenseURL: http://en.wikipedia.org/wiki/All_rights_reserved
objects: Sketcher::SketchObject×2, PartDesign::CoordinateSystem×2, PartDesign::Pad×1, PartDesign::Pocket×1, PartDesign::Fillet×1, PartDesign::Body×1
note: 11 computed .brp shape members not serialized (recipe doc carries the construction recipe); baked Part::Feature solids carry a one-line shape summary decoded from their .brp

FEATURE [Sketcher::SketchObject] Sketch
  FullyConstrained = true
  MapMode = 5
  Placement = pos=(0,0,0) rot=(1,0,0;1.5708rad)
  Support = -> [XZ_Plane]
  sketch-geometry (8):
    g0: LineSegment StartX=-27 StartY=27 StartZ=0 EndX=27 EndY=27 EndZ=0
    g1: LineSegment StartX=27 StartY=27 StartZ=0 EndX=27 EndY=-27 EndZ=0
    g2: LineSegment StartX=27 StartY=-27 StartZ=0 EndX=-27 EndY=-27 EndZ=0
    g3: LineSegment StartX=-27 StartY=-27 StartZ=0 EndX=-27 EndY=27 EndZ=0
    g4: LineSegment StartX=-30 StartY=30 StartZ=0 EndX=30 EndY=30 EndZ=0
    g5: LineSegment StartX=30 StartY=30 StartZ=0 EndX=30 EndY=-30 EndZ=0
    g6: LineSegment StartX=30 StartY=-30 StartZ=0 EndX=-30 EndY=-30 EndZ=0
    g7: LineSegment StartX=-30 StartY=-30 StartZ=0 EndX=-30 EndY=30 EndZ=0
  constraints (22):
    c: Coincident(g0,g1)
    c: Coincident(g1,g2)
    c: Coincident(g2,g3)
    c: Coincident(g3,g0)
    c: Horizontal(g0)
    c: Horizontal(g2)
    c: Vertical(g1)
    c: Vertical(g3)
    c: Coincident(g4,g5)
    c: Coincident(g5,g6)
    c: Coincident(g6,g7)
    c: Coincident(g7,g4)
    c: Horizontal(g6)
    c: Vertical(g5)
    c: DistanceY(g7,g7) = 60
    c: DistanceX(g4,g4) = 60
    c: Symmetric(g4,g4,g-2)
    c: Symmetric(g6,g4,g-1)
    c: DistanceX(g0,g4) = 3
    c: DistanceY(g0,g4) = 3
    c: DistanceX(g6,g2) = 3
    c: DistanceY(g6,g2) = 3
FEATURE [PartDesign::Pad] Pad
  Direction = (1,1,1)
  Length = 793
  Length2 = 100
  Placement = pos=(0,0,0) rot=(1,0,0;1.5708rad)
  Profile = -> Sketch
  Type = 0
FEATURE [Sketcher::SketchObject] Sketch001
  ExternalGeometry = -> [Pad]
  FullyConstrained = true
  MapMode = 5
  Placement = pos=(0,0,30) rot=(0,0,1;3.14159rad)
  Support = -> [Pad]
  sketch-geometry (2):
    g0: Circle CenterX=0 CenterY=763 CenterZ=0 NormalX=0 NormalY=0 NormalZ=1 AngleXU=0 Radius=4.25
    g1: Circle CenterX=0 CenterY=30 CenterZ=0 NormalX=0 NormalY=0 NormalZ=1 AngleXU=0 Radius=4.25
  constraints (6):
    c: PointOnObject(g0,g-2)
    c: PointOnObject(g1,g-2)
    c: Equal(g1,g0)
    c: Diameter(g0) = 8.5
    c: DistanceY(g0,g-4) = 30
    c: DistanceY(g-3,g1) = 30
FEATURE [PartDesign::Pocket] Pocket
  BaseFeature = -> Pad
  Length = 3
  Length2 = 100
  Placement = pos=(0,0,0) rot=(1,0,0;1.5708rad)
  Profile = -> Sketch001
  Type = 0
FEATURE [PartDesign::CoordinateSystem] LCS_hole1
  AttacherType = Attacher::AttachEngine3D
  MapMode = 11
  Placement = pos=(0,-763,30) rot=(0,0,-1;1.5708rad)
  Support = -> [Pocket]
FEATURE [PartDesign::CoordinateSystem] LCS_hole2
  AttacherType = Attacher::AttachEngine3D
  MapMode = 11
  Placement = pos=(0,-30,30) rot=(0,0,-1;1.5708rad)
  Support = -> [Pocket]
FEATURE [PartDesign::Fillet] Fillet
  Base = -> Pad [Edge2,Edge5,Edge1,Edge8]
  BaseFeature = -> Pad
  Placement = pos=(0,0,0) rot=(1,0,0;1.5708rad)
  Radius = 3
  SupportTransform = false
FEATURE [PartDesign::Body] Body
  Group = -> [Sketch,Pad,Sketch001,Pocket,LCS_hole1,LCS_hole2,Fillet]
  Origin = -> Origin
  Tip = -> Fillet
---- part zbracket.FCStd = doc fcstd_24de39b7a98b ----
FCSTD DOCUMENT  (FreeCAD 0.19R)
Label: zbracket
License: All rights reserved
LicenseURL: http://en.wikipedia.org/wiki/All_rights_reserved
objects: PartDesign::CoordinateSystem×9, Sketcher::SketchObject×4, PartDesign::Pocket×3, PartDesign::Pad×1, PartDesign::Body×1
note: 22 computed .brp shape members not serialized (recipe doc carries the construction recipe); baked Part::Feature solids carry a one-line shape summary decoded from their .brp

FEATURE [Sketcher::SketchObject] Sketch
  FullyConstrained = true
  MapMode = 5
  Support = -> [XY_Plane]
  sketch-geometry (14):
    g0: LineSegment StartX=0 StartY=0 StartZ=0 EndX=-161 EndY=0 EndZ=0
    g1: LineSegment StartX=0 StartY=0 StartZ=0 EndX=0 EndY=89 EndZ=0
    g2: LineSegment StartX=-3 StartY=3 StartZ=0 EndX=-111 EndY=3 EndZ=0
    g3: LineSegment StartX=0 StartY=89 StartZ=0 EndX=-15 EndY=89 EndZ=0
    g4: LineSegment StartX=-111 StartY=3 StartZ=0 EndX=-111 EndY=89 EndZ=0
    g5: LineSegment StartX=-111 StartY=89 StartZ=0 EndX=-161 EndY=89 EndZ=0
    g6: LineSegment StartX=-161 StartY=0 StartZ=0 EndX=-161 EndY=89 EndZ=0
    g7: LineSegment StartX=-158 StartY=86 StartZ=0 EndX=-114 EndY=86 EndZ=0
    g8: LineSegment StartX=-114 StartY=86 StartZ=0 EndX=-114 EndY=3 EndZ=0
    g9: LineSegment StartX=-114 StartY=3 StartZ=0 EndX=-158 EndY=3 EndZ=0
    g10: LineSegment StartX=-158 StartY=3 StartZ=0 EndX=-158 EndY=86 EndZ=0
    g11: LineSegment StartX=-15 StartY=89 StartZ=0 EndX=-15 EndY=86 EndZ=0
    g12: LineSegment StartX=-15 StartY=86 StartZ=0 EndX=-3 EndY=86 EndZ=0
    g13: LineSegment StartX=-3 StartY=86 StartZ=0 EndX=-3 EndY=3 EndZ=0
  constraints (41):
    c: Coincident(g0,g-1)
    c: PointOnObject(g0,g-1)
    c: Coincident(g1,g0)
    c: PointOnObject(g1,g-2)
    c: Horizontal(g2)
    c: DistanceY(g1,g1) = 89
    c: Coincident(g3,g1)
    c: Horizontal(g3)
    c: DistanceX(g3,g3) = 15
    c: DistanceX(g2,g2) = 108
    c: Coincident(g4,g2)
    c: Vertical(g4)
    c: Coincident(g5,g4)
    c: Horizontal(g5)
    c: Coincident(g6,g0)
    c: Vertical(g6)
    c: Coincident(g5,g6)
    c: Equal(g1,g6)
    c: DistanceX(g5,g5) = 50
    c: DistanceY(g0,g2) = 3
    c: Coincident(g7,g8)
    c: Coincident(g8,g9)
    c: Coincident(g9,g10)
    c: Coincident(g10,g7)
    c: Horizontal(g7)
    c: Horizontal(g9)
    c: Vertical(g8)
    c: Vertical(g10)
    c: DistanceY(g0,g9) = 3
    c: DistanceY(g7,g4) = 3
    c: DistanceX(g7,g4) = 3
    c: DistanceX(g0,g9) = 3
    c: Coincident(g11,g3)
    c: Vertical(g11)
    c: Coincident(g12,g11)
    c: Horizontal(g12)
    c: Coincident(g13,g12)
    c: Coincident(g13,g2)
    c: Vertical(g13)
    c: DistanceX(g12,g1) = 3
    c: DistanceY(g11,g11) = 3
FEATURE [PartDesign::Pad] Pad
  Direction = (1,1,1)
  Length = 120
  Length2 = 100
  Profile = -> Sketch
  Type = 0
FEATURE [Sketcher::SketchObject] Sketch001
  ExternalGeometry = -> [Pad]
  FullyConstrained = true
  MapMode = 5
  Placement = pos=(0,0,0) rot=(0.57735,0.57735,0.57735;2.0944rad)
  Support = -> [Pad]
  sketch-geometry (4):
    g0: Circle CenterX=27 CenterY=42 CenterZ=0 NormalX=0 NormalY=0 NormalZ=1 AngleXU=0 Radius=2.75
    g1: Circle CenterX=65 CenterY=42 CenterZ=0 NormalX=0 NormalY=0 NormalZ=1 AngleXU=0 Radius=2.75
    g2: Circle CenterX=27 CenterY=12 CenterZ=0 NormalX=0 NormalY=0 NormalZ=1 AngleXU=0 Radius=2.75
    g3: Circle CenterX=65 CenterY=12 CenterZ=0 NormalX=0 NormalY=0 NormalZ=1 AngleXU=0 Radius=2.75
  constraints (12):
    c: Equal(g0,g1)
    c: Equal(g1,g3)
    c: Equal(g3,g2)
    c: Diameter(g1) = 5.5
    c: DistanceY(g2,g0) = 30
    c: DistanceY(g3,g1) = 30
    c: DistanceX(g0,g1) = 38
    c: DistanceX(g2,g3) = 38
    c: DistanceY(g-4,g3) = 12
    c: DistanceY(g-4,g2) = 12
    c: DistanceX(g-1,g2) = 27
    c: DistanceX(g-1,g0) = 27
FEATURE [PartDesign::Pocket] Pocket
  BaseFeature = -> Pad
  Length = 3
  Length2 = 100
  Profile = -> Sketch001
  Type = 0
FEATURE [PartDesign::CoordinateSystem] LCS_h1
  AttacherType = Attacher::AttachEngine3D
  MapMode = 11
  Placement = pos=(-3,65,42) rot=(0.707107,0,0.707107;3.14159rad)
  Support = -> [Pocket]
FEATURE [PartDesign::CoordinateSystem] LCS_h2
  AttacherType = Attacher::AttachEngine3D
  MapMode = 11
  Placement = pos=(-3,65,12) rot=(0.707107,0,0.707107;3.14159rad)
  Support = -> [Pocket]
FEATURE [Sketcher::SketchObject] Sketch002
  ExternalGeometry = -> [Pocket]
  FullyConstrained = true
  MapMode = 5
  Placement = pos=(0,0,0) rot=(1,0,0;1.5708rad)
  Support = -> [Pocket]
  sketch-geometry (8):
    g0: Circle CenterX=-40 CenterY=85 CenterZ=0 NormalX=0 NormalY=0 NormalZ=1 AngleXU=0 Radius=4.25
    g1: Circle CenterX=-15 CenterY=85 CenterZ=0 NormalX=0 NormalY=0 NormalZ=1 AngleXU=0 Radius=4.25
    g2: Circle CenterX=-40 CenterY=35 CenterZ=0 NormalX=0 NormalY=0 NormalZ=1 AngleXU=0 Radius=4.25
    g3: Circle CenterX=-15 CenterY=35 CenterZ=0 NormalX=0 NormalY=0 NormalZ=1 AngleXU=0 Radius=4.25
    g4: Circle CenterX=-99 CenterY=85 CenterZ=0 NormalX=0 NormalY=0 NormalZ=1 AngleXU=0 Radius=4.25
    g5: Circle CenterX=-74 CenterY=85 CenterZ=0 NormalX=0 NormalY=0 NormalZ=1 AngleXU=0 Radius=4.25
    g6: Circle CenterX=-99 CenterY=35 CenterZ=0 NormalX=0 NormalY=0 NormalZ=1 AngleXU=0 Radius=4.25
    g7: Circle CenterX=-74 CenterY=35 CenterZ=0 NormalX=0 NormalY=0 NormalZ=1 AngleXU=0 Radius=4.25
  constraints (24):
    c: Equal(g3,g1)
    c: Equal(g1,g0)
    c: Equal(g0,g2)
    c: DistanceY(g2,g0) = 50
    c: DistanceY(g3,g1) = 50
    c: DistanceY(g-1,g3) = 35
    c: DistanceY(g-1,g2) = 35
    c: DistanceX(g3,g-1) = 15
    c: DistanceX(g2,g3) = 25
    c: DistanceX(g0,g1) = 25
    c: DistanceX(g1,g-1) = 15
    c: Equal(g7,g5)
    c: Equal(g5,g4)
    c: Equal(g4,g6)
    c: Equal(g1,g5) = 9
    c: DistanceY(g6,g4) = 50
    c: DistanceY(g7,g5) = 50
    c: DistanceX(g6,g7) = 25
    c: DistanceX(g4,g5) = 25
    c: Diameter(g5) = 8.5
    c: DistanceX(g-3,g6) = 15
    c: DistanceX(g-3,g4) = 15
    c: DistanceY(g-3,g6) = 35
    c: DistanceY(g-3,g7) = 35
FEATURE [PartDesign::Pocket] Pocket001
  BaseFeature = -> Pocket
  Length = 3
  Length2 = 100
  Profile = -> Sketch002
  Type = 0
FEATURE [PartDesign::CoordinateSystem] LCS_ho1
  AttacherType = Attacher::AttachEngine3D
  MapMode = 11
  Placement = pos=(0,65,42) rot=(0.707107,0,0.707107;3.14159rad)
  Support = -> [Pocket001]
FEATURE [PartDesign::CoordinateSystem] LCS_ho2
  AttacherType = Attacher::AttachEngine3D
  MapMode = 11
  Placement = pos=(0,65,12) rot=(0.707107,0,0.707107;3.14159rad)
  Support = -> [Pocket001]
FEATURE [PartDesign::CoordinateSystem] LCS_1
  AttacherType = Attacher::AttachEngine3D
  MapMode = 11
  Placement = pos=(-15,0,85) rot=(0.57735,-0.57735,0.57735;2.0944rad)
  Support = -> [Pocket001]
FEATURE [Sketcher::SketchObject] Sketch003
  ExternalGeometry = -> [Pocket001]
  FullyConstrained = true
  MapMode = 5
  Placement = pos=(-161,0,0) rot=(0.57735,-0.57735,-0.57735;2.0944rad)
  Support = -> [Pocket001]
  sketch-geometry (4):
    g0: Circle CenterX=-66 CenterY=47 CenterZ=0 NormalX=0 NormalY=0 NormalZ=1 AngleXU=0 Radius=2.75
    g1: Circle CenterX=-26 CenterY=47 CenterZ=0 NormalX=0 NormalY=0 NormalZ=1 AngleXU=0 Radius=2.75
    g2: Circle CenterX=-66 CenterY=23 CenterZ=0 NormalX=0 NormalY=0 NormalZ=1 AngleXU=0 Radius=2.75
    g3: Circle CenterX=-26 CenterY=23 CenterZ=0 NormalX=0 NormalY=0 NormalZ=1 AngleXU=0 Radius=2.75
  constraints (12):
    c: Equal(g2,g3)
    c: Equal(g3,g1)
    c: Equal(g1,g0)
    c: Diameter(g1) = 5.5
    c: DistanceY(g3,g1) = 24
    c: DistanceX(g0,g1) = 40
    c: DistanceY(g2,g0) = 24
    c: DistanceX(g2,g3) = 40
    c: DistanceY(g-1,g3) = 23
    c: DistanceY(g-1,g2) = 23
    c: DistanceX(g3,g-1) = 26
    c: DistanceX(g1,g-1) = 26
FEATURE [PartDesign::Pocket] Pocket002
  BaseFeature = -> Pocket001
  Length = 3
  Length2 = 100
  Profile = -> Sketch003
  Type = 0
FEATURE [PartDesign::CoordinateSystem] LCS_DSG16_MOUNT1
  AttacherType = Attacher::AttachEngine3D
  MapMode = 11
  Placement = pos=(-158,66,23) rot=(0,-1,0;1.5708rad)
  Support = -> [Pocket002]
FEATURE [PartDesign::CoordinateSystem] LCS_DSG16_MOUNT2
  AttacherType = Attacher::AttachEngine3D
  MapMode = 11
  Placement = pos=(-158,26,23) rot=(0,-1,0;1.5708rad)
  Support = -> [Pocket002]
FEATURE [PartDesign::CoordinateSystem] LCS_DSG16_MOUNT3
  AttacherType = Attacher::AttachEngine3D
  MapMode = 11
  Placement = pos=(-158,66,47) rot=(0,-1,0;1.5708rad)
  Support = -> [Pocket002]
FEATURE [PartDesign::CoordinateSystem] LCS_DSG16_MOUNT4
  AttacherType = Attacher::AttachEngine3D
  MapMode = 11
  Placement = pos=(-158,26,47) rot=(0,-1,0;1.5708rad)
  Support = -> [Pocket002]
FEATURE [PartDesign::Body] Body
  Group = -> [Sketch,Pad,Sketch001,Pocket,LCS_h1,LCS_h2,Sketch002,Pocket001,LCS_ho1,LCS_ho2,LCS_1,Sketch003,Pocket002,LCS_DSG16_MOUNT1,LCS_DSG16_MOUNT2,LCS_DSG16_MOUNT3,LCS_DSG16_MOUNT4]
  Origin = -> Origin
  Tip = -> Pocket002
